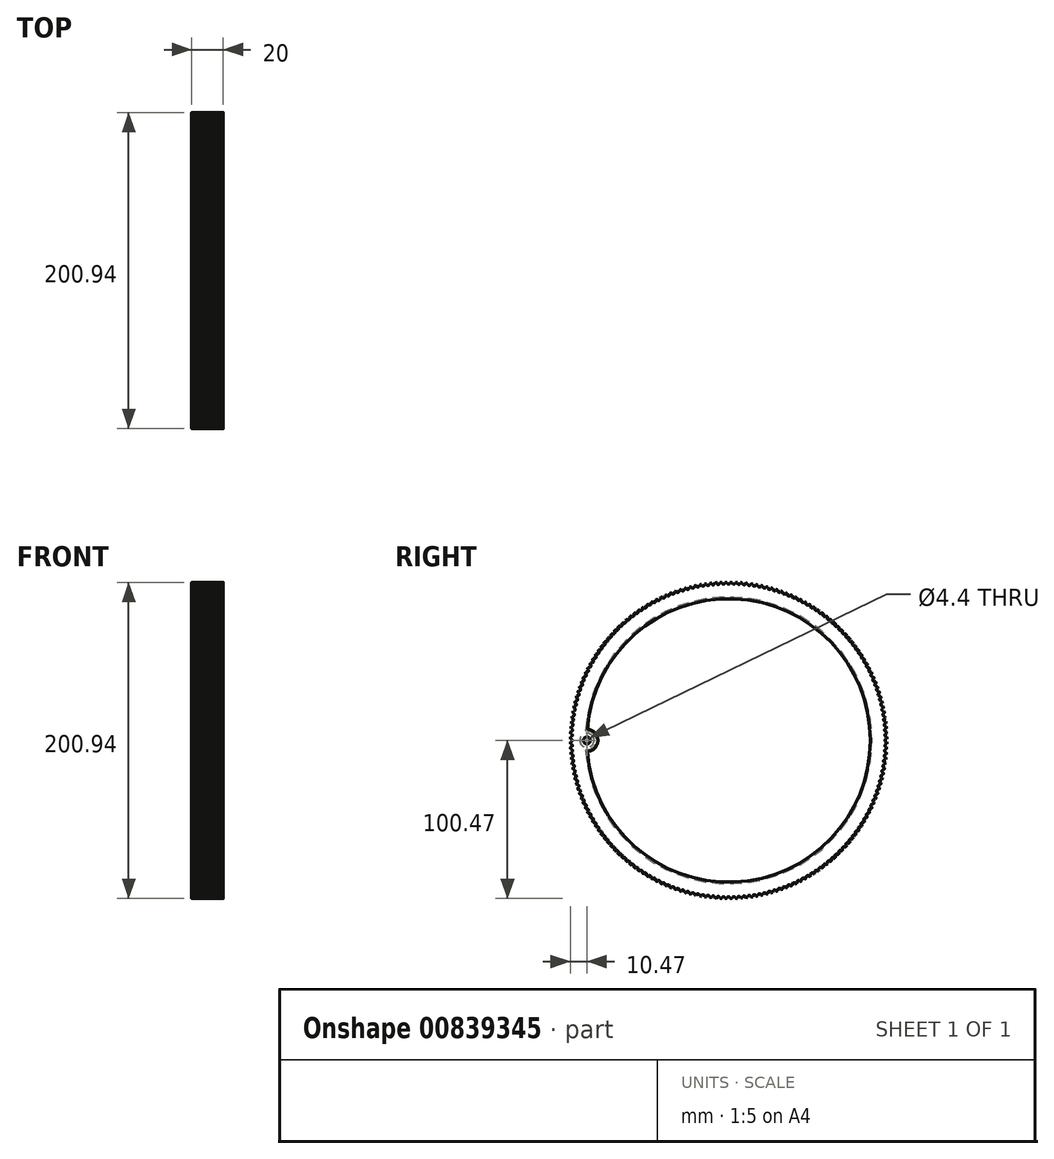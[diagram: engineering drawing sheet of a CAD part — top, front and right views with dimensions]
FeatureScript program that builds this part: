
annotation { "Feature Type Name" : "Feature", "Feature Type Description" : "" }
export const myFeature = defineFeature(function(context is Context, id is Id, definition is map)
    precondition{}
    {
        {
            var Q0;
            Q0=qCreatedBy(makeId("Right.planeOp"),FACE);
            var sketch = newSketch(context, id + "F0", { "sketchPlane" : qUnion([Q0])});
            skCircle(sketch, "E0", {"center": v(0, 0) * mm, "radius": 90 * mm});
            skLineSegment(sketch, "E1", {"start": v(0, 0) * mm, "end": v(0, 100.53) * mm, "construction": true});
            skPoint(sketch, "E2.center", {"position": v(0, 61.04) * mm});
            skLineSegment(sketch, "E2.anchor1", {"start": v(0, 61.04) * mm, "end": v(0, 81.8) * mm, "construction": true});
            skLineSegment(sketch, "E3.trimOffspring", {"start": v(0, 10.5) * mm, "end": v(0, 81.8) * mm, "construction": true});
            skLineSegment(sketch, "E4", {"start": v(-1.05, 100.47) * mm, "end": v(-1, 100.18) * mm});
            skArc(sketch, "E5", {"start": v(0.01, 99.33) * mm, "mid": v(0, 99.33) * mm, "end": v(-0.01, 99.33) * mm});
            skArc(sketch, "E6.filletArc", {"start": v(-1, 100.18) * mm, "mid": v(-0.67, 99.57) * mm, "end": v(-0.01, 99.33) * mm});
            skLineSegment(sketch, "E7.MirrorCS", {"start": v(1.05, 100.47) * mm, "end": v(1, 100.18) * mm});
            skArc(sketch, "E8.MirrorCS", {"start": v(1, 100.18) * mm, "mid": v(0.67, 99.57) * mm, "end": v(0.01, 99.33) * mm});
            skPoint(sketch, "E9.orphan", {"position": v(-12.8, 89.08) * mm});
            skPoint(sketch, "E10.orphan", {"position": v(12.8, 89.08) * mm});
            skLineSegment(sketch, "E11", {"start": v(0.02, 100.33) * mm, "end": v(1, 100.18) * mm, "construction": true});
            skLineSegment(sketch, "E12", {"start": v(-0.02, 100.33) * mm, "end": v(-1, 100.18) * mm, "construction": true});
            skLineSegment(sketch, "E13", {"start": v(-1.05, 100.47) * mm, "end": v(0, 100.53) * mm, "construction": true});
            skLineSegment(sketch, "E14", {"start": v(1.05, 100.47) * mm, "end": v(0, 100.53) * mm, "construction": true});
            skCircle(sketch, "E15", {"center": v(0, 0) * mm, "radius": 100.48 * mm});
            skArc(sketch, "E16.1.0", {"start": v(-4.28, 100.1) * mm, "mid": v(-3.93, 99.5) * mm, "end": v(-3.26, 99.27) * mm});
            skArc(sketch, "E16.1.1", {"start": v(-3.24, 99.27) * mm, "mid": v(-3.25, 99.27) * mm, "end": v(-3.26, 99.27) * mm});
            skArc(sketch, "E16.1.2", {"start": v(-2.27, 100.16) * mm, "mid": v(-2.59, 99.54) * mm, "end": v(-3.24, 99.27) * mm});
            skLineSegment(sketch, "E16.1.3", {"start": v(-2.24, 100.46) * mm, "end": v(-2.27, 100.16) * mm});
            skLineSegment(sketch, "E16.1.4", {"start": v(-4.33, 100.39) * mm, "end": v(-4.28, 100.1) * mm});
            skArc(sketch, "E16.2.0", {"start": v(-7.56, 99.9) * mm, "mid": v(-7.18, 99.31) * mm, "end": v(-6.51, 99.11) * mm});
            skArc(sketch, "E16.2.1", {"start": v(-6.48, 99.12) * mm, "mid": v(-6.5, 99.11) * mm, "end": v(-6.51, 99.11) * mm});
            skArc(sketch, "E16.2.2", {"start": v(-5.55, 100.04) * mm, "mid": v(-5.84, 99.4) * mm, "end": v(-6.48, 99.12) * mm});
            skLineSegment(sketch, "E16.2.3", {"start": v(-5.53, 100.33) * mm, "end": v(-5.55, 100.04) * mm});
            skLineSegment(sketch, "E16.2.4", {"start": v(-7.62, 100.2) * mm, "end": v(-7.56, 99.9) * mm});
            skArc(sketch, "E16.3.0", {"start": v(-10.82, 99.6) * mm, "mid": v(-10.43, 99.03) * mm, "end": v(-9.75, 98.85) * mm});
            skArc(sketch, "E16.3.1", {"start": v(-9.72, 98.85) * mm, "mid": v(-9.74, 98.85) * mm, "end": v(-9.75, 98.85) * mm});
            skArc(sketch, "E16.3.2", {"start": v(-8.82, 99.8) * mm, "mid": v(-9.1, 99.16) * mm, "end": v(-9.72, 98.85) * mm});
            skLineSegment(sketch, "E16.3.3", {"start": v(-8.8, 100.1) * mm, "end": v(-8.82, 99.8) * mm});
            skLineSegment(sketch, "E16.3.4", {"start": v(-10.9, 99.89) * mm, "end": v(-10.82, 99.6) * mm});
            skArc(sketch, "E16.4.0", {"start": v(-14.07, 99.2) * mm, "mid": v(-13.66, 98.63) * mm, "end": v(-12.98, 98.48) * mm});
            skArc(sketch, "E16.4.1", {"start": v(-12.95, 98.48) * mm, "mid": v(-12.96, 98.48) * mm, "end": v(-12.98, 98.48) * mm});
            skArc(sketch, "E16.4.2", {"start": v(-12.08, 99.46) * mm, "mid": v(-12.33, 98.8) * mm, "end": v(-12.95, 98.48) * mm});
            skLineSegment(sketch, "E16.4.3", {"start": v(-12.08, 99.75) * mm, "end": v(-12.08, 99.46) * mm});
            skLineSegment(sketch, "E16.4.4", {"start": v(-14.15, 99.48) * mm, "end": v(-14.07, 99.2) * mm});
            skArc(sketch, "E16.5.0", {"start": v(-17.31, 98.68) * mm, "mid": v(-16.88, 98.13) * mm, "end": v(-16.2, 98) * mm});
            skArc(sketch, "E16.5.1", {"start": v(-16.17, 98) * mm, "mid": v(-16.18, 98) * mm, "end": v(-16.2, 98) * mm});
            skArc(sketch, "E16.5.2", {"start": v(-15.33, 99.01) * mm, "mid": v(-15.56, 98.35) * mm, "end": v(-16.17, 98) * mm});
            skLineSegment(sketch, "E16.5.3", {"start": v(-15.33, 99.3) * mm, "end": v(-15.33, 99.01) * mm});
            skLineSegment(sketch, "E16.5.4", {"start": v(-17.4, 98.96) * mm, "end": v(-17.31, 98.68) * mm});
            skArc(sketch, "E16.6.0", {"start": v(-20.53, 98.06) * mm, "mid": v(-20.08, 97.53) * mm, "end": v(-19.4, 97.42) * mm});
            skArc(sketch, "E16.6.1", {"start": v(-19.36, 97.42) * mm, "mid": v(-19.38, 97.42) * mm, "end": v(-19.4, 97.42) * mm});
            skArc(sketch, "E16.6.2", {"start": v(-18.56, 98.46) * mm, "mid": v(-18.77, 97.79) * mm, "end": v(-19.36, 97.42) * mm});
            skLineSegment(sketch, "E16.6.3", {"start": v(-18.57, 98.75) * mm, "end": v(-18.56, 98.46) * mm});
            skLineSegment(sketch, "E16.6.4", {"start": v(-20.63, 98.34) * mm, "end": v(-20.53, 98.06) * mm});
            skArc(sketch, "E16.7.0", {"start": v(-23.73, 97.34) * mm, "mid": v(-23.26, 96.82) * mm, "end": v(-22.57, 96.73) * mm});
            skArc(sketch, "E16.7.1", {"start": v(-22.54, 96.74) * mm, "mid": v(-22.55, 96.73) * mm, "end": v(-22.57, 96.73) * mm});
            skArc(sketch, "E16.7.2", {"start": v(-21.77, 97.8) * mm, "mid": v(-21.96, 97.12) * mm, "end": v(-22.54, 96.74) * mm});
            skLineSegment(sketch, "E16.7.3", {"start": v(-21.8, 98.09) * mm, "end": v(-21.77, 97.8) * mm});
            skLineSegment(sketch, "E16.7.4", {"start": v(-23.84, 97.61) * mm, "end": v(-23.73, 97.34) * mm});
            skArc(sketch, "E16.8.0", {"start": v(-26.9, 96.51) * mm, "mid": v(-26.42, 96) * mm, "end": v(-25.72, 95.94) * mm});
            skArc(sketch, "E16.8.1", {"start": v(-25.7, 95.95) * mm, "mid": v(-25.7, 95.94) * mm, "end": v(-25.72, 95.94) * mm});
            skArc(sketch, "E16.8.2", {"start": v(-24.96, 97.03) * mm, "mid": v(-25.12, 96.35) * mm, "end": v(-25.7, 95.95) * mm});
            skLineSegment(sketch, "E16.8.3", {"start": v(-25, 97.32) * mm, "end": v(-24.96, 97.03) * mm});
            skLineSegment(sketch, "E16.8.4", {"start": v(-27.02, 96.78) * mm, "end": v(-26.9, 96.51) * mm});
            skArc(sketch, "E16.9.0", {"start": v(-30.04, 95.58) * mm, "mid": v(-29.55, 95.09) * mm, "end": v(-28.85, 95.05) * mm});
            skArc(sketch, "E16.9.1", {"start": v(-28.82, 95.05) * mm, "mid": v(-28.83, 95.05) * mm, "end": v(-28.85, 95.05) * mm});
            skArc(sketch, "E16.9.2", {"start": v(-28.12, 96.16) * mm, "mid": v(-28.26, 95.48) * mm, "end": v(-28.82, 95.05) * mm});
            skLineSegment(sketch, "E16.9.3", {"start": v(-28.16, 96.45) * mm, "end": v(-28.12, 96.16) * mm});
            skLineSegment(sketch, "E16.9.4", {"start": v(-30.17, 95.84) * mm, "end": v(-30.04, 95.58) * mm});
            skArc(sketch, "E16.10.0", {"start": v(-33.16, 94.54) * mm, "mid": v(-32.64, 94.07) * mm, "end": v(-31.94, 94.05) * mm});
            skArc(sketch, "E16.10.1", {"start": v(-31.91, 94.06) * mm, "mid": v(-31.93, 94.06) * mm, "end": v(-31.94, 94.05) * mm});
            skArc(sketch, "E16.10.2", {"start": v(-31.25, 95.2) * mm, "mid": v(-31.37, 94.5) * mm, "end": v(-31.91, 94.06) * mm});
            skLineSegment(sketch, "E16.10.3", {"start": v(-31.3, 95.48) * mm, "end": v(-31.25, 95.2) * mm});
            skLineSegment(sketch, "E16.10.4", {"start": v(-33.29, 94.8) * mm, "end": v(-33.16, 94.54) * mm});
            skArc(sketch, "E16.11.0", {"start": v(-36.23, 93.4) * mm, "mid": v(-35.7, 92.95) * mm, "end": v(-35, 92.96) * mm});
            skArc(sketch, "E16.11.1", {"start": v(-34.97, 92.97) * mm, "mid": v(-34.99, 92.96) * mm, "end": v(-35, 92.96) * mm});
            skArc(sketch, "E16.11.2", {"start": v(-34.35, 94.12) * mm, "mid": v(-34.45, 93.42) * mm, "end": v(-34.97, 92.97) * mm});
            skLineSegment(sketch, "E16.11.3", {"start": v(-34.41, 94.4) * mm, "end": v(-34.35, 94.12) * mm});
            skLineSegment(sketch, "E16.11.4", {"start": v(-36.37, 93.67) * mm, "end": v(-36.23, 93.4) * mm});
            skArc(sketch, "E16.12.0", {"start": v(-39.27, 92.17) * mm, "mid": v(-38.72, 91.73) * mm, "end": v(-38.02, 91.76) * mm});
            skArc(sketch, "E16.12.1", {"start": v(-38, 91.77) * mm, "mid": v(-38.01, 91.77) * mm, "end": v(-38.02, 91.76) * mm});
            skArc(sketch, "E16.12.2", {"start": v(-37.4, 92.94) * mm, "mid": v(-37.48, 92.25) * mm, "end": v(-38, 91.77) * mm});
            skLineSegment(sketch, "E16.12.3", {"start": v(-37.48, 93.23) * mm, "end": v(-37.4, 92.94) * mm});
            skLineSegment(sketch, "E16.12.4", {"start": v(-39.42, 92.43) * mm, "end": v(-39.27, 92.17) * mm});
            skArc(sketch, "E16.13.0", {"start": v(-42.26, 90.84) * mm, "mid": v(-41.7, 90.42) * mm, "end": v(-41, 90.47) * mm});
            skArc(sketch, "E16.13.1", {"start": v(-40.98, 90.48) * mm, "mid": v(-41, 90.47) * mm, "end": v(-41, 90.47) * mm});
            skArc(sketch, "E16.13.2", {"start": v(-40.43, 91.67) * mm, "mid": v(-40.48, 90.97) * mm, "end": v(-40.98, 90.48) * mm});
            skLineSegment(sketch, "E16.13.3", {"start": v(-40.51, 91.95) * mm, "end": v(-40.43, 91.67) * mm});
            skLineSegment(sketch, "E16.13.4", {"start": v(-42.42, 91.09) * mm, "end": v(-42.26, 90.84) * mm});
            skArc(sketch, "E16.14.0", {"start": v(-45.21, 89.4) * mm, "mid": v(-44.64, 89) * mm, "end": v(-43.94, 89.08) * mm});
            skArc(sketch, "E16.14.1", {"start": v(-43.92, 89.09) * mm, "mid": v(-43.93, 89.08) * mm, "end": v(-43.94, 89.08) * mm});
            skArc(sketch, "E16.14.2", {"start": v(-43.4, 90.3) * mm, "mid": v(-43.44, 89.6) * mm, "end": v(-43.92, 89.09) * mm});
            skLineSegment(sketch, "E16.14.3", {"start": v(-43.5, 90.58) * mm, "end": v(-43.4, 90.3) * mm});
            skLineSegment(sketch, "E16.14.4", {"start": v(-45.38, 89.65) * mm, "end": v(-45.21, 89.4) * mm});
            skArc(sketch, "E16.15.0", {"start": v(-48.11, 87.88) * mm, "mid": v(-47.53, 87.5) * mm, "end": v(-46.84, 87.6) * mm});
            skArc(sketch, "E16.15.1", {"start": v(-46.8, 87.6) * mm, "mid": v(-46.82, 87.6) * mm, "end": v(-46.84, 87.6) * mm});
            skArc(sketch, "E16.15.2", {"start": v(-46.34, 88.83) * mm, "mid": v(-46.35, 88.13) * mm, "end": v(-46.8, 87.6) * mm});
            skLineSegment(sketch, "E16.15.3", {"start": v(-46.44, 89.1) * mm, "end": v(-46.34, 88.83) * mm});
            skLineSegment(sketch, "E16.15.4", {"start": v(-48.29, 88.12) * mm, "end": v(-48.11, 87.88) * mm});
            skArc(sketch, "E16.16.0", {"start": v(-50.96, 86.26) * mm, "mid": v(-50.37, 85.9) * mm, "end": v(-49.68, 86.01) * mm});
            skArc(sketch, "E16.16.1", {"start": v(-49.65, 86.03) * mm, "mid": v(-49.66, 86.02) * mm, "end": v(-49.68, 86.01) * mm});
            skArc(sketch, "E16.16.2", {"start": v(-49.22, 87.27) * mm, "mid": v(-49.2, 86.57) * mm, "end": v(-49.65, 86.03) * mm});
            skLineSegment(sketch, "E16.16.3", {"start": v(-49.33, 87.54) * mm, "end": v(-49.22, 87.27) * mm});
            skLineSegment(sketch, "E16.16.4", {"start": v(-51.14, 86.49) * mm, "end": v(-50.96, 86.26) * mm});
            skArc(sketch, "E16.17.0", {"start": v(-53.76, 84.55) * mm, "mid": v(-53.15, 84.2) * mm, "end": v(-52.46, 84.34) * mm});
            skArc(sketch, "E16.17.1", {"start": v(-52.44, 84.36) * mm, "mid": v(-52.45, 84.35) * mm, "end": v(-52.46, 84.34) * mm});
            skArc(sketch, "E16.17.2", {"start": v(-52.05, 85.6) * mm, "mid": v(-52.01, 84.9) * mm, "end": v(-52.44, 84.36) * mm});
            skLineSegment(sketch, "E16.17.3", {"start": v(-52.17, 85.88) * mm, "end": v(-52.05, 85.6) * mm});
            skLineSegment(sketch, "E16.17.4", {"start": v(-53.95, 84.77) * mm, "end": v(-53.76, 84.55) * mm});
            skArc(sketch, "E16.18.0", {"start": v(-56.5, 82.74) * mm, "mid": v(-55.88, 82.42) * mm, "end": v(-55.2, 82.58) * mm});
            skArc(sketch, "E16.18.1", {"start": v(-55.17, 82.6) * mm, "mid": v(-55.18, 82.59) * mm, "end": v(-55.2, 82.58) * mm});
            skArc(sketch, "E16.18.2", {"start": v(-54.82, 83.86) * mm, "mid": v(-54.76, 83.16) * mm, "end": v(-55.17, 82.6) * mm});
            skLineSegment(sketch, "E16.18.3", {"start": v(-54.95, 84.12) * mm, "end": v(-54.82, 83.86) * mm});
            skLineSegment(sketch, "E16.18.4", {"start": v(-56.7, 82.96) * mm, "end": v(-56.5, 82.74) * mm});
            skArc(sketch, "E16.19.0", {"start": v(-59.17, 80.85) * mm, "mid": v(-58.54, 80.55) * mm, "end": v(-57.87, 80.73) * mm});
            skArc(sketch, "E16.19.1", {"start": v(-57.84, 80.75) * mm, "mid": v(-57.86, 80.74) * mm, "end": v(-57.87, 80.73) * mm});
            skArc(sketch, "E16.19.2", {"start": v(-57.54, 82.02) * mm, "mid": v(-57.45, 81.33) * mm, "end": v(-57.84, 80.75) * mm});
            skLineSegment(sketch, "E16.19.3", {"start": v(-57.67, 82.28) * mm, "end": v(-57.54, 82.02) * mm});
            skLineSegment(sketch, "E16.19.4", {"start": v(-59.38, 81.06) * mm, "end": v(-59.17, 80.85) * mm});
            skArc(sketch, "E16.20.0", {"start": v(-61.79, 78.87) * mm, "mid": v(-61.15, 78.59) * mm, "end": v(-60.48, 78.8) * mm});
            skArc(sketch, "E16.20.1", {"start": v(-60.45, 78.81) * mm, "mid": v(-60.47, 78.8) * mm, "end": v(-60.48, 78.8) * mm});
            skArc(sketch, "E16.20.2", {"start": v(-60.2, 80.1) * mm, "mid": v(-60.08, 79.4) * mm, "end": v(-60.45, 78.81) * mm});
            skLineSegment(sketch, "E16.20.3", {"start": v(-60.33, 80.35) * mm, "end": v(-60.2, 80.1) * mm});
            skLineSegment(sketch, "E16.20.4", {"start": v(-62, 79.07) * mm, "end": v(-61.79, 78.87) * mm});
            skArc(sketch, "E16.21.0", {"start": v(-64.33, 76.8) * mm, "mid": v(-63.69, 76.54) * mm, "end": v(-63.02, 76.77) * mm});
            skArc(sketch, "E16.21.1", {"start": v(-63, 76.79) * mm, "mid": v(-63.01, 76.78) * mm, "end": v(-63.02, 76.77) * mm});
            skArc(sketch, "E16.21.2", {"start": v(-62.78, 78.08) * mm, "mid": v(-62.65, 77.4) * mm, "end": v(-63, 76.79) * mm});
            skLineSegment(sketch, "E16.21.3", {"start": v(-62.93, 78.33) * mm, "end": v(-62.78, 78.08) * mm});
            skLineSegment(sketch, "E16.21.4", {"start": v(-64.55, 77) * mm, "end": v(-64.33, 76.8) * mm});
            skArc(sketch, "E16.22.0", {"start": v(-66.81, 74.66) * mm, "mid": v(-66.16, 74.42) * mm, "end": v(-65.5, 74.67) * mm});
            skArc(sketch, "E16.22.1", {"start": v(-65.48, 74.69) * mm, "mid": v(-65.5, 74.68) * mm, "end": v(-65.5, 74.67) * mm});
            skArc(sketch, "E16.22.2", {"start": v(-65.3, 75.99) * mm, "mid": v(-65.15, 75.3) * mm, "end": v(-65.48, 74.69) * mm});
            skLineSegment(sketch, "E16.22.3", {"start": v(-65.46, 76.23) * mm, "end": v(-65.3, 75.99) * mm});
            skLineSegment(sketch, "E16.22.4", {"start": v(-67.04, 74.85) * mm, "end": v(-66.81, 74.66) * mm});
            skArc(sketch, "E16.23.0", {"start": v(-69.22, 72.43) * mm, "mid": v(-68.55, 72.21) * mm, "end": v(-67.9, 72.49) * mm});
            skArc(sketch, "E16.23.1", {"start": v(-67.89, 72.5) * mm, "mid": v(-67.9, 72.5) * mm, "end": v(-67.9, 72.49) * mm});
            skArc(sketch, "E16.23.2", {"start": v(-67.75, 73.8) * mm, "mid": v(-67.58, 73.13) * mm, "end": v(-67.89, 72.5) * mm});
            skLineSegment(sketch, "E16.23.3", {"start": v(-67.92, 74.05) * mm, "end": v(-67.75, 73.8) * mm});
            skLineSegment(sketch, "E16.23.4", {"start": v(-69.45, 72.62) * mm, "end": v(-69.22, 72.43) * mm});
            skArc(sketch, "E16.24.0", {"start": v(-71.55, 70.13) * mm, "mid": v(-70.88, 69.93) * mm, "end": v(-70.24, 70.22) * mm});
            skArc(sketch, "E16.24.1", {"start": v(-70.22, 70.24) * mm, "mid": v(-70.23, 70.23) * mm, "end": v(-70.24, 70.22) * mm});
            skArc(sketch, "E16.24.2", {"start": v(-70.13, 71.55) * mm, "mid": v(-69.93, 70.88) * mm, "end": v(-70.22, 70.24) * mm});
            skLineSegment(sketch, "E16.24.3", {"start": v(-70.3, 71.79) * mm, "end": v(-70.13, 71.55) * mm});
            skLineSegment(sketch, "E16.24.4", {"start": v(-71.79, 70.3) * mm, "end": v(-71.55, 70.13) * mm});
            skArc(sketch, "E16.25.0", {"start": v(-73.8, 67.75) * mm, "mid": v(-73.13, 67.58) * mm, "end": v(-72.5, 67.89) * mm});
            skArc(sketch, "E16.25.1", {"start": v(-72.49, 67.9) * mm, "mid": v(-72.5, 67.9) * mm, "end": v(-72.5, 67.89) * mm});
            skArc(sketch, "E16.25.2", {"start": v(-72.43, 69.22) * mm, "mid": v(-72.21, 68.55) * mm, "end": v(-72.49, 67.9) * mm});
            skLineSegment(sketch, "E16.25.3", {"start": v(-72.62, 69.45) * mm, "end": v(-72.43, 69.22) * mm});
            skLineSegment(sketch, "E16.25.4", {"start": v(-74.05, 67.92) * mm, "end": v(-73.8, 67.75) * mm});
            skArc(sketch, "E16.26.0", {"start": v(-75.99, 65.3) * mm, "mid": v(-75.3, 65.15) * mm, "end": v(-74.69, 65.48) * mm});
            skArc(sketch, "E16.26.1", {"start": v(-74.67, 65.5) * mm, "mid": v(-74.68, 65.5) * mm, "end": v(-74.69, 65.48) * mm});
            skArc(sketch, "E16.26.2", {"start": v(-74.66, 66.81) * mm, "mid": v(-74.42, 66.16) * mm, "end": v(-74.67, 65.5) * mm});
            skLineSegment(sketch, "E16.26.3", {"start": v(-74.85, 67.04) * mm, "end": v(-74.66, 66.81) * mm});
            skLineSegment(sketch, "E16.26.4", {"start": v(-76.23, 65.46) * mm, "end": v(-75.99, 65.3) * mm});
            skArc(sketch, "E16.27.0", {"start": v(-78.08, 62.78) * mm, "mid": v(-77.4, 62.65) * mm, "end": v(-76.79, 63) * mm});
            skArc(sketch, "E16.27.1", {"start": v(-76.77, 63.02) * mm, "mid": v(-76.78, 63.01) * mm, "end": v(-76.79, 63) * mm});
            skArc(sketch, "E16.27.2", {"start": v(-76.8, 64.33) * mm, "mid": v(-76.54, 63.69) * mm, "end": v(-76.77, 63.02) * mm});
            skLineSegment(sketch, "E16.27.3", {"start": v(-77, 64.55) * mm, "end": v(-76.8, 64.33) * mm});
            skLineSegment(sketch, "E16.27.4", {"start": v(-78.33, 62.93) * mm, "end": v(-78.08, 62.78) * mm});
            skArc(sketch, "E16.28.0", {"start": v(-80.1, 60.2) * mm, "mid": v(-79.4, 60.08) * mm, "end": v(-78.81, 60.45) * mm});
            skArc(sketch, "E16.28.1", {"start": v(-78.8, 60.48) * mm, "mid": v(-78.8, 60.47) * mm, "end": v(-78.81, 60.45) * mm});
            skArc(sketch, "E16.28.2", {"start": v(-78.87, 61.79) * mm, "mid": v(-78.59, 61.15) * mm, "end": v(-78.8, 60.48) * mm});
            skLineSegment(sketch, "E16.28.3", {"start": v(-79.07, 62) * mm, "end": v(-78.87, 61.79) * mm});
            skLineSegment(sketch, "E16.28.4", {"start": v(-80.35, 60.33) * mm, "end": v(-80.1, 60.2) * mm});
            skArc(sketch, "E16.29.0", {"start": v(-82.02, 57.54) * mm, "mid": v(-81.33, 57.45) * mm, "end": v(-80.75, 57.84) * mm});
            skArc(sketch, "E16.29.1", {"start": v(-80.73, 57.87) * mm, "mid": v(-80.74, 57.86) * mm, "end": v(-80.75, 57.84) * mm});
            skArc(sketch, "E16.29.2", {"start": v(-80.85, 59.17) * mm, "mid": v(-80.55, 58.54) * mm, "end": v(-80.73, 57.87) * mm});
            skLineSegment(sketch, "E16.29.3", {"start": v(-81.06, 59.38) * mm, "end": v(-80.85, 59.17) * mm});
            skLineSegment(sketch, "E16.29.4", {"start": v(-82.28, 57.67) * mm, "end": v(-82.02, 57.54) * mm});
            skArc(sketch, "E16.30.0", {"start": v(-83.86, 54.82) * mm, "mid": v(-83.16, 54.76) * mm, "end": v(-82.6, 55.17) * mm});
            skArc(sketch, "E16.30.1", {"start": v(-82.58, 55.2) * mm, "mid": v(-82.59, 55.18) * mm, "end": v(-82.6, 55.17) * mm});
            skArc(sketch, "E16.30.2", {"start": v(-82.74, 56.5) * mm, "mid": v(-82.42, 55.88) * mm, "end": v(-82.58, 55.2) * mm});
            skLineSegment(sketch, "E16.30.3", {"start": v(-82.96, 56.7) * mm, "end": v(-82.74, 56.5) * mm});
            skLineSegment(sketch, "E16.30.4", {"start": v(-84.12, 54.95) * mm, "end": v(-83.86, 54.82) * mm});
            skArc(sketch, "E16.31.0", {"start": v(-85.6, 52.05) * mm, "mid": v(-84.9, 52.01) * mm, "end": v(-84.36, 52.44) * mm});
            skArc(sketch, "E16.31.1", {"start": v(-84.34, 52.46) * mm, "mid": v(-84.35, 52.45) * mm, "end": v(-84.36, 52.44) * mm});
            skArc(sketch, "E16.31.2", {"start": v(-84.55, 53.76) * mm, "mid": v(-84.2, 53.15) * mm, "end": v(-84.34, 52.46) * mm});
            skLineSegment(sketch, "E16.31.3", {"start": v(-84.77, 53.95) * mm, "end": v(-84.55, 53.76) * mm});
            skLineSegment(sketch, "E16.31.4", {"start": v(-85.88, 52.17) * mm, "end": v(-85.6, 52.05) * mm});
            skArc(sketch, "E16.32.0", {"start": v(-87.27, 49.22) * mm, "mid": v(-86.57, 49.2) * mm, "end": v(-86.03, 49.65) * mm});
            skArc(sketch, "E16.32.1", {"start": v(-86.01, 49.68) * mm, "mid": v(-86.02, 49.66) * mm, "end": v(-86.03, 49.65) * mm});
            skArc(sketch, "E16.32.2", {"start": v(-86.26, 50.96) * mm, "mid": v(-85.9, 50.37) * mm, "end": v(-86.01, 49.68) * mm});
            skLineSegment(sketch, "E16.32.3", {"start": v(-86.49, 51.14) * mm, "end": v(-86.26, 50.96) * mm});
            skLineSegment(sketch, "E16.32.4", {"start": v(-87.54, 49.33) * mm, "end": v(-87.27, 49.22) * mm});
            skArc(sketch, "E16.33.0", {"start": v(-88.83, 46.34) * mm, "mid": v(-88.13, 46.35) * mm, "end": v(-87.6, 46.8) * mm});
            skArc(sketch, "E16.33.1", {"start": v(-87.6, 46.84) * mm, "mid": v(-87.6, 46.82) * mm, "end": v(-87.6, 46.8) * mm});
            skArc(sketch, "E16.33.2", {"start": v(-87.88, 48.11) * mm, "mid": v(-87.5, 47.53) * mm, "end": v(-87.6, 46.84) * mm});
            skLineSegment(sketch, "E16.33.3", {"start": v(-88.12, 48.29) * mm, "end": v(-87.88, 48.11) * mm});
            skLineSegment(sketch, "E16.33.4", {"start": v(-89.1, 46.44) * mm, "end": v(-88.83, 46.34) * mm});
            skArc(sketch, "E16.34.0", {"start": v(-90.3, 43.4) * mm, "mid": v(-89.6, 43.44) * mm, "end": v(-89.09, 43.92) * mm});
            skArc(sketch, "E16.34.1", {"start": v(-89.08, 43.94) * mm, "mid": v(-89.08, 43.93) * mm, "end": v(-89.09, 43.92) * mm});
            skArc(sketch, "E16.34.2", {"start": v(-89.4, 45.21) * mm, "mid": v(-89, 44.64) * mm, "end": v(-89.08, 43.94) * mm});
            skLineSegment(sketch, "E16.34.3", {"start": v(-89.65, 45.38) * mm, "end": v(-89.4, 45.21) * mm});
            skLineSegment(sketch, "E16.34.4", {"start": v(-90.58, 43.5) * mm, "end": v(-90.3, 43.4) * mm});
            skArc(sketch, "E16.35.0", {"start": v(-91.67, 40.43) * mm, "mid": v(-90.97, 40.48) * mm, "end": v(-90.48, 40.98) * mm});
            skArc(sketch, "E16.35.1", {"start": v(-90.47, 41) * mm, "mid": v(-90.47, 41) * mm, "end": v(-90.48, 40.98) * mm});
            skArc(sketch, "E16.35.2", {"start": v(-90.84, 42.26) * mm, "mid": v(-90.42, 41.7) * mm, "end": v(-90.47, 41) * mm});
            skLineSegment(sketch, "E16.35.3", {"start": v(-91.09, 42.42) * mm, "end": v(-90.84, 42.26) * mm});
            skLineSegment(sketch, "E16.35.4", {"start": v(-91.95, 40.51) * mm, "end": v(-91.67, 40.43) * mm});
            skArc(sketch, "E16.36.0", {"start": v(-92.94, 37.4) * mm, "mid": v(-92.25, 37.48) * mm, "end": v(-91.77, 38) * mm});
            skArc(sketch, "E16.36.1", {"start": v(-91.76, 38.02) * mm, "mid": v(-91.77, 38.01) * mm, "end": v(-91.77, 38) * mm});
            skArc(sketch, "E16.36.2", {"start": v(-92.17, 39.27) * mm, "mid": v(-91.73, 38.72) * mm, "end": v(-91.76, 38.02) * mm});
            skLineSegment(sketch, "E16.36.3", {"start": v(-92.43, 39.42) * mm, "end": v(-92.17, 39.27) * mm});
            skLineSegment(sketch, "E16.36.4", {"start": v(-93.23, 37.48) * mm, "end": v(-92.94, 37.4) * mm});
            skArc(sketch, "E16.37.0", {"start": v(-94.12, 34.35) * mm, "mid": v(-93.42, 34.45) * mm, "end": v(-92.97, 34.97) * mm});
            skArc(sketch, "E16.37.1", {"start": v(-92.96, 35) * mm, "mid": v(-92.96, 34.99) * mm, "end": v(-92.97, 34.97) * mm});
            skArc(sketch, "E16.37.2", {"start": v(-93.4, 36.23) * mm, "mid": v(-92.95, 35.7) * mm, "end": v(-92.96, 35) * mm});
            skLineSegment(sketch, "E16.37.3", {"start": v(-93.67, 36.37) * mm, "end": v(-93.4, 36.23) * mm});
            skLineSegment(sketch, "E16.37.4", {"start": v(-94.4, 34.41) * mm, "end": v(-94.12, 34.35) * mm});
            skArc(sketch, "E16.38.0", {"start": v(-95.2, 31.25) * mm, "mid": v(-94.5, 31.37) * mm, "end": v(-94.06, 31.91) * mm});
            skArc(sketch, "E16.38.1", {"start": v(-94.05, 31.94) * mm, "mid": v(-94.06, 31.93) * mm, "end": v(-94.06, 31.91) * mm});
            skArc(sketch, "E16.38.2", {"start": v(-94.54, 33.16) * mm, "mid": v(-94.07, 32.64) * mm, "end": v(-94.05, 31.94) * mm});
            skLineSegment(sketch, "E16.38.3", {"start": v(-94.8, 33.29) * mm, "end": v(-94.54, 33.16) * mm});
            skLineSegment(sketch, "E16.38.4", {"start": v(-95.48, 31.3) * mm, "end": v(-95.2, 31.25) * mm});
            skArc(sketch, "E16.39.0", {"start": v(-96.16, 28.12) * mm, "mid": v(-95.48, 28.26) * mm, "end": v(-95.05, 28.82) * mm});
            skArc(sketch, "E16.39.1", {"start": v(-95.05, 28.85) * mm, "mid": v(-95.05, 28.83) * mm, "end": v(-95.05, 28.82) * mm});
            skArc(sketch, "E16.39.2", {"start": v(-95.58, 30.04) * mm, "mid": v(-95.09, 29.55) * mm, "end": v(-95.05, 28.85) * mm});
            skLineSegment(sketch, "E16.39.3", {"start": v(-95.84, 30.17) * mm, "end": v(-95.58, 30.04) * mm});
            skLineSegment(sketch, "E16.39.4", {"start": v(-96.45, 28.16) * mm, "end": v(-96.16, 28.12) * mm});
            skArc(sketch, "E16.40.0", {"start": v(-97.03, 24.96) * mm, "mid": v(-96.35, 25.12) * mm, "end": v(-95.95, 25.7) * mm});
            skArc(sketch, "E16.40.1", {"start": v(-95.94, 25.72) * mm, "mid": v(-95.94, 25.7) * mm, "end": v(-95.95, 25.7) * mm});
            skArc(sketch, "E16.40.2", {"start": v(-96.51, 26.9) * mm, "mid": v(-96, 26.42) * mm, "end": v(-95.94, 25.72) * mm});
            skLineSegment(sketch, "E16.40.3", {"start": v(-96.78, 27.02) * mm, "end": v(-96.51, 26.9) * mm});
            skLineSegment(sketch, "E16.40.4", {"start": v(-97.32, 25) * mm, "end": v(-97.03, 24.96) * mm});
            skArc(sketch, "E16.41.0", {"start": v(-97.8, 21.77) * mm, "mid": v(-97.12, 21.96) * mm, "end": v(-96.74, 22.54) * mm});
            skArc(sketch, "E16.41.1", {"start": v(-96.73, 22.57) * mm, "mid": v(-96.73, 22.55) * mm, "end": v(-96.74, 22.54) * mm});
            skArc(sketch, "E16.41.2", {"start": v(-97.34, 23.73) * mm, "mid": v(-96.82, 23.26) * mm, "end": v(-96.73, 22.57) * mm});
            skLineSegment(sketch, "E16.41.3", {"start": v(-97.61, 23.84) * mm, "end": v(-97.34, 23.73) * mm});
            skLineSegment(sketch, "E16.41.4", {"start": v(-98.09, 21.8) * mm, "end": v(-97.8, 21.77) * mm});
            skArc(sketch, "E16.42.0", {"start": v(-98.46, 18.56) * mm, "mid": v(-97.79, 18.77) * mm, "end": v(-97.42, 19.36) * mm});
            skArc(sketch, "E16.42.1", {"start": v(-97.42, 19.4) * mm, "mid": v(-97.42, 19.38) * mm, "end": v(-97.42, 19.36) * mm});
            skArc(sketch, "E16.42.2", {"start": v(-98.06, 20.53) * mm, "mid": v(-97.53, 20.08) * mm, "end": v(-97.42, 19.4) * mm});
            skLineSegment(sketch, "E16.42.3", {"start": v(-98.34, 20.63) * mm, "end": v(-98.06, 20.53) * mm});
            skLineSegment(sketch, "E16.42.4", {"start": v(-98.75, 18.57) * mm, "end": v(-98.46, 18.56) * mm});
            skArc(sketch, "E16.43.0", {"start": v(-99.01, 15.33) * mm, "mid": v(-98.35, 15.56) * mm, "end": v(-98, 16.17) * mm});
            skArc(sketch, "E16.43.1", {"start": v(-98, 16.2) * mm, "mid": v(-98, 16.18) * mm, "end": v(-98, 16.17) * mm});
            skArc(sketch, "E16.43.2", {"start": v(-98.68, 17.31) * mm, "mid": v(-98.13, 16.88) * mm, "end": v(-98, 16.2) * mm});
            skLineSegment(sketch, "E16.43.3", {"start": v(-98.96, 17.4) * mm, "end": v(-98.68, 17.31) * mm});
            skLineSegment(sketch, "E16.43.4", {"start": v(-99.3, 15.33) * mm, "end": v(-99.01, 15.33) * mm});
            skArc(sketch, "E16.44.0", {"start": v(-99.46, 12.08) * mm, "mid": v(-98.8, 12.33) * mm, "end": v(-98.48, 12.95) * mm});
            skArc(sketch, "E16.44.1", {"start": v(-98.48, 12.98) * mm, "mid": v(-98.48, 12.96) * mm, "end": v(-98.48, 12.95) * mm});
            skArc(sketch, "E16.44.2", {"start": v(-99.2, 14.07) * mm, "mid": v(-98.63, 13.66) * mm, "end": v(-98.48, 12.98) * mm});
            skLineSegment(sketch, "E16.44.3", {"start": v(-99.48, 14.15) * mm, "end": v(-99.2, 14.07) * mm});
            skLineSegment(sketch, "E16.44.4", {"start": v(-99.75, 12.08) * mm, "end": v(-99.46, 12.08) * mm});
            skArc(sketch, "E16.45.0", {"start": v(-99.8, 8.82) * mm, "mid": v(-99.16, 9.1) * mm, "end": v(-98.85, 9.72) * mm});
            skArc(sketch, "E16.45.1", {"start": v(-98.85, 9.75) * mm, "mid": v(-98.85, 9.74) * mm, "end": v(-98.85, 9.72) * mm});
            skArc(sketch, "E16.45.2", {"start": v(-99.6, 10.82) * mm, "mid": v(-99.03, 10.43) * mm, "end": v(-98.85, 9.75) * mm});
            skLineSegment(sketch, "E16.45.3", {"start": v(-99.89, 10.9) * mm, "end": v(-99.6, 10.82) * mm});
            skLineSegment(sketch, "E16.45.4", {"start": v(-100.1, 8.8) * mm, "end": v(-99.8, 8.82) * mm});
            skArc(sketch, "E16.46.0", {"start": v(-100.04, 5.55) * mm, "mid": v(-99.4, 5.84) * mm, "end": v(-99.12, 6.48) * mm});
            skArc(sketch, "E16.46.1", {"start": v(-99.11, 6.51) * mm, "mid": v(-99.11, 6.5) * mm, "end": v(-99.12, 6.48) * mm});
            skArc(sketch, "E16.46.2", {"start": v(-99.9, 7.56) * mm, "mid": v(-99.31, 7.18) * mm, "end": v(-99.11, 6.51) * mm});
            skLineSegment(sketch, "E16.46.3", {"start": v(-100.2, 7.62) * mm, "end": v(-99.9, 7.56) * mm});
            skLineSegment(sketch, "E16.46.4", {"start": v(-100.33, 5.53) * mm, "end": v(-100.04, 5.55) * mm});
            skArc(sketch, "E16.47.0", {"start": v(-100.16, 2.27) * mm, "mid": v(-99.54, 2.59) * mm, "end": v(-99.27, 3.24) * mm});
            skArc(sketch, "E16.47.1", {"start": v(-99.27, 3.26) * mm, "mid": v(-99.27, 3.25) * mm, "end": v(-99.27, 3.24) * mm});
            skArc(sketch, "E16.47.2", {"start": v(-100.1, 4.28) * mm, "mid": v(-99.5, 3.93) * mm, "end": v(-99.27, 3.26) * mm});
            skLineSegment(sketch, "E16.47.3", {"start": v(-100.39, 4.33) * mm, "end": v(-100.1, 4.28) * mm});
            skLineSegment(sketch, "E16.47.4", {"start": v(-100.46, 2.24) * mm, "end": v(-100.16, 2.27) * mm});
            skArc(sketch, "E16.48.0", {"start": v(-100.18, -1) * mm, "mid": v(-99.57, -0.67) * mm, "end": v(-99.33, -0.01) * mm});
            skArc(sketch, "E16.48.1", {"start": v(-99.33, 0.01) * mm, "mid": v(-99.33, 0) * mm, "end": v(-99.33, -0.01) * mm});
            skArc(sketch, "E16.48.2", {"start": v(-100.18, 1) * mm, "mid": v(-99.57, 0.67) * mm, "end": v(-99.33, 0.01) * mm});
            skLineSegment(sketch, "E16.48.3", {"start": v(-100.47, 1.05) * mm, "end": v(-100.18, 1) * mm});
            skLineSegment(sketch, "E16.48.4", {"start": v(-100.47, -1.05) * mm, "end": v(-100.18, -1) * mm});
            skArc(sketch, "E16.49.0", {"start": v(-100.1, -4.28) * mm, "mid": v(-99.5, -3.93) * mm, "end": v(-99.27, -3.26) * mm});
            skArc(sketch, "E16.49.1", {"start": v(-99.27, -3.24) * mm, "mid": v(-99.27, -3.25) * mm, "end": v(-99.27, -3.26) * mm});
            skArc(sketch, "E16.49.2", {"start": v(-100.16, -2.27) * mm, "mid": v(-99.54, -2.59) * mm, "end": v(-99.27, -3.24) * mm});
            skLineSegment(sketch, "E16.49.3", {"start": v(-100.46, -2.24) * mm, "end": v(-100.16, -2.27) * mm});
            skLineSegment(sketch, "E16.49.4", {"start": v(-100.39, -4.33) * mm, "end": v(-100.1, -4.28) * mm});
            skArc(sketch, "E16.50.0", {"start": v(-99.9, -7.56) * mm, "mid": v(-99.31, -7.18) * mm, "end": v(-99.11, -6.51) * mm});
            skArc(sketch, "E16.50.1", {"start": v(-99.12, -6.48) * mm, "mid": v(-99.11, -6.5) * mm, "end": v(-99.11, -6.51) * mm});
            skArc(sketch, "E16.50.2", {"start": v(-100.04, -5.55) * mm, "mid": v(-99.4, -5.84) * mm, "end": v(-99.12, -6.48) * mm});
            skLineSegment(sketch, "E16.50.3", {"start": v(-100.33, -5.53) * mm, "end": v(-100.04, -5.55) * mm});
            skLineSegment(sketch, "E16.50.4", {"start": v(-100.2, -7.62) * mm, "end": v(-99.9, -7.56) * mm});
            skArc(sketch, "E16.51.0", {"start": v(-99.6, -10.82) * mm, "mid": v(-99.03, -10.43) * mm, "end": v(-98.85, -9.75) * mm});
            skArc(sketch, "E16.51.1", {"start": v(-98.85, -9.72) * mm, "mid": v(-98.85, -9.74) * mm, "end": v(-98.85, -9.75) * mm});
            skArc(sketch, "E16.51.2", {"start": v(-99.8, -8.82) * mm, "mid": v(-99.16, -9.1) * mm, "end": v(-98.85, -9.72) * mm});
            skLineSegment(sketch, "E16.51.3", {"start": v(-100.1, -8.8) * mm, "end": v(-99.8, -8.82) * mm});
            skLineSegment(sketch, "E16.51.4", {"start": v(-99.89, -10.9) * mm, "end": v(-99.6, -10.82) * mm});
            skArc(sketch, "E16.52.0", {"start": v(-99.2, -14.07) * mm, "mid": v(-98.63, -13.66) * mm, "end": v(-98.48, -12.98) * mm});
            skArc(sketch, "E16.52.1", {"start": v(-98.48, -12.95) * mm, "mid": v(-98.48, -12.96) * mm, "end": v(-98.48, -12.98) * mm});
            skArc(sketch, "E16.52.2", {"start": v(-99.46, -12.08) * mm, "mid": v(-98.8, -12.33) * mm, "end": v(-98.48, -12.95) * mm});
            skLineSegment(sketch, "E16.52.3", {"start": v(-99.75, -12.08) * mm, "end": v(-99.46, -12.08) * mm});
            skLineSegment(sketch, "E16.52.4", {"start": v(-99.48, -14.15) * mm, "end": v(-99.2, -14.07) * mm});
            skArc(sketch, "E16.53.0", {"start": v(-98.68, -17.31) * mm, "mid": v(-98.13, -16.88) * mm, "end": v(-98, -16.2) * mm});
            skArc(sketch, "E16.53.1", {"start": v(-98, -16.17) * mm, "mid": v(-98, -16.18) * mm, "end": v(-98, -16.2) * mm});
            skArc(sketch, "E16.53.2", {"start": v(-99.01, -15.33) * mm, "mid": v(-98.35, -15.56) * mm, "end": v(-98, -16.17) * mm});
            skLineSegment(sketch, "E16.53.3", {"start": v(-99.3, -15.33) * mm, "end": v(-99.01, -15.33) * mm});
            skLineSegment(sketch, "E16.53.4", {"start": v(-98.96, -17.4) * mm, "end": v(-98.68, -17.31) * mm});
            skArc(sketch, "E16.54.0", {"start": v(-98.06, -20.53) * mm, "mid": v(-97.53, -20.08) * mm, "end": v(-97.42, -19.4) * mm});
            skArc(sketch, "E16.54.1", {"start": v(-97.42, -19.36) * mm, "mid": v(-97.42, -19.38) * mm, "end": v(-97.42, -19.4) * mm});
            skArc(sketch, "E16.54.2", {"start": v(-98.46, -18.56) * mm, "mid": v(-97.79, -18.77) * mm, "end": v(-97.42, -19.36) * mm});
            skLineSegment(sketch, "E16.54.3", {"start": v(-98.75, -18.57) * mm, "end": v(-98.46, -18.56) * mm});
            skLineSegment(sketch, "E16.54.4", {"start": v(-98.34, -20.63) * mm, "end": v(-98.06, -20.53) * mm});
            skArc(sketch, "E16.55.0", {"start": v(-97.34, -23.73) * mm, "mid": v(-96.82, -23.26) * mm, "end": v(-96.73, -22.57) * mm});
            skArc(sketch, "E16.55.1", {"start": v(-96.74, -22.54) * mm, "mid": v(-96.73, -22.55) * mm, "end": v(-96.73, -22.57) * mm});
            skArc(sketch, "E16.55.2", {"start": v(-97.8, -21.77) * mm, "mid": v(-97.12, -21.96) * mm, "end": v(-96.74, -22.54) * mm});
            skLineSegment(sketch, "E16.55.3", {"start": v(-98.09, -21.8) * mm, "end": v(-97.8, -21.77) * mm});
            skLineSegment(sketch, "E16.55.4", {"start": v(-97.61, -23.84) * mm, "end": v(-97.34, -23.73) * mm});
            skArc(sketch, "E16.56.0", {"start": v(-96.51, -26.9) * mm, "mid": v(-96, -26.42) * mm, "end": v(-95.94, -25.72) * mm});
            skArc(sketch, "E16.56.1", {"start": v(-95.95, -25.7) * mm, "mid": v(-95.94, -25.7) * mm, "end": v(-95.94, -25.72) * mm});
            skArc(sketch, "E16.56.2", {"start": v(-97.03, -24.96) * mm, "mid": v(-96.35, -25.12) * mm, "end": v(-95.95, -25.7) * mm});
            skLineSegment(sketch, "E16.56.3", {"start": v(-97.32, -25) * mm, "end": v(-97.03, -24.96) * mm});
            skLineSegment(sketch, "E16.56.4", {"start": v(-96.78, -27.02) * mm, "end": v(-96.51, -26.9) * mm});
            skArc(sketch, "E16.57.0", {"start": v(-95.58, -30.04) * mm, "mid": v(-95.09, -29.55) * mm, "end": v(-95.05, -28.85) * mm});
            skArc(sketch, "E16.57.1", {"start": v(-95.05, -28.82) * mm, "mid": v(-95.05, -28.83) * mm, "end": v(-95.05, -28.85) * mm});
            skArc(sketch, "E16.57.2", {"start": v(-96.16, -28.12) * mm, "mid": v(-95.48, -28.26) * mm, "end": v(-95.05, -28.82) * mm});
            skLineSegment(sketch, "E16.57.3", {"start": v(-96.45, -28.16) * mm, "end": v(-96.16, -28.12) * mm});
            skLineSegment(sketch, "E16.57.4", {"start": v(-95.84, -30.17) * mm, "end": v(-95.58, -30.04) * mm});
            skArc(sketch, "E16.58.0", {"start": v(-94.54, -33.16) * mm, "mid": v(-94.07, -32.64) * mm, "end": v(-94.05, -31.94) * mm});
            skArc(sketch, "E16.58.1", {"start": v(-94.06, -31.91) * mm, "mid": v(-94.06, -31.93) * mm, "end": v(-94.05, -31.94) * mm});
            skArc(sketch, "E16.58.2", {"start": v(-95.2, -31.25) * mm, "mid": v(-94.5, -31.37) * mm, "end": v(-94.06, -31.91) * mm});
            skLineSegment(sketch, "E16.58.3", {"start": v(-95.48, -31.3) * mm, "end": v(-95.2, -31.25) * mm});
            skLineSegment(sketch, "E16.58.4", {"start": v(-94.8, -33.29) * mm, "end": v(-94.54, -33.16) * mm});
            skArc(sketch, "E16.59.0", {"start": v(-93.4, -36.23) * mm, "mid": v(-92.95, -35.7) * mm, "end": v(-92.96, -35) * mm});
            skArc(sketch, "E16.59.1", {"start": v(-92.97, -34.97) * mm, "mid": v(-92.96, -34.99) * mm, "end": v(-92.96, -35) * mm});
            skArc(sketch, "E16.59.2", {"start": v(-94.12, -34.35) * mm, "mid": v(-93.42, -34.45) * mm, "end": v(-92.97, -34.97) * mm});
            skLineSegment(sketch, "E16.59.3", {"start": v(-94.4, -34.41) * mm, "end": v(-94.12, -34.35) * mm});
            skLineSegment(sketch, "E16.59.4", {"start": v(-93.67, -36.37) * mm, "end": v(-93.4, -36.23) * mm});
            skArc(sketch, "E16.60.0", {"start": v(-92.17, -39.27) * mm, "mid": v(-91.73, -38.72) * mm, "end": v(-91.76, -38.02) * mm});
            skArc(sketch, "E16.60.1", {"start": v(-91.77, -38) * mm, "mid": v(-91.77, -38.01) * mm, "end": v(-91.76, -38.02) * mm});
            skArc(sketch, "E16.60.2", {"start": v(-92.94, -37.4) * mm, "mid": v(-92.25, -37.48) * mm, "end": v(-91.77, -38) * mm});
            skLineSegment(sketch, "E16.60.3", {"start": v(-93.23, -37.48) * mm, "end": v(-92.94, -37.4) * mm});
            skLineSegment(sketch, "E16.60.4", {"start": v(-92.43, -39.42) * mm, "end": v(-92.17, -39.27) * mm});
            skArc(sketch, "E16.61.0", {"start": v(-90.84, -42.26) * mm, "mid": v(-90.42, -41.7) * mm, "end": v(-90.47, -41) * mm});
            skArc(sketch, "E16.61.1", {"start": v(-90.48, -40.98) * mm, "mid": v(-90.47, -41) * mm, "end": v(-90.47, -41) * mm});
            skArc(sketch, "E16.61.2", {"start": v(-91.67, -40.43) * mm, "mid": v(-90.97, -40.48) * mm, "end": v(-90.48, -40.98) * mm});
            skLineSegment(sketch, "E16.61.3", {"start": v(-91.95, -40.51) * mm, "end": v(-91.67, -40.43) * mm});
            skLineSegment(sketch, "E16.61.4", {"start": v(-91.09, -42.42) * mm, "end": v(-90.84, -42.26) * mm});
            skArc(sketch, "E16.62.0", {"start": v(-89.4, -45.21) * mm, "mid": v(-89, -44.64) * mm, "end": v(-89.08, -43.94) * mm});
            skArc(sketch, "E16.62.1", {"start": v(-89.09, -43.92) * mm, "mid": v(-89.08, -43.93) * mm, "end": v(-89.08, -43.94) * mm});
            skArc(sketch, "E16.62.2", {"start": v(-90.3, -43.4) * mm, "mid": v(-89.6, -43.44) * mm, "end": v(-89.09, -43.92) * mm});
            skLineSegment(sketch, "E16.62.3", {"start": v(-90.58, -43.5) * mm, "end": v(-90.3, -43.4) * mm});
            skLineSegment(sketch, "E16.62.4", {"start": v(-89.65, -45.38) * mm, "end": v(-89.4, -45.21) * mm});
            skArc(sketch, "E16.63.0", {"start": v(-87.88, -48.11) * mm, "mid": v(-87.5, -47.53) * mm, "end": v(-87.6, -46.84) * mm});
            skArc(sketch, "E16.63.1", {"start": v(-87.6, -46.8) * mm, "mid": v(-87.6, -46.82) * mm, "end": v(-87.6, -46.84) * mm});
            skArc(sketch, "E16.63.2", {"start": v(-88.83, -46.34) * mm, "mid": v(-88.13, -46.35) * mm, "end": v(-87.6, -46.8) * mm});
            skLineSegment(sketch, "E16.63.3", {"start": v(-89.1, -46.44) * mm, "end": v(-88.83, -46.34) * mm});
            skLineSegment(sketch, "E16.63.4", {"start": v(-88.12, -48.29) * mm, "end": v(-87.88, -48.11) * mm});
            skArc(sketch, "E16.64.0", {"start": v(-86.26, -50.96) * mm, "mid": v(-85.9, -50.37) * mm, "end": v(-86.01, -49.68) * mm});
            skArc(sketch, "E16.64.1", {"start": v(-86.03, -49.65) * mm, "mid": v(-86.02, -49.66) * mm, "end": v(-86.01, -49.68) * mm});
            skArc(sketch, "E16.64.2", {"start": v(-87.27, -49.22) * mm, "mid": v(-86.57, -49.2) * mm, "end": v(-86.03, -49.65) * mm});
            skLineSegment(sketch, "E16.64.3", {"start": v(-87.54, -49.33) * mm, "end": v(-87.27, -49.22) * mm});
            skLineSegment(sketch, "E16.64.4", {"start": v(-86.49, -51.14) * mm, "end": v(-86.26, -50.96) * mm});
            skArc(sketch, "E16.65.0", {"start": v(-84.55, -53.76) * mm, "mid": v(-84.2, -53.15) * mm, "end": v(-84.34, -52.46) * mm});
            skArc(sketch, "E16.65.1", {"start": v(-84.36, -52.44) * mm, "mid": v(-84.35, -52.45) * mm, "end": v(-84.34, -52.46) * mm});
            skArc(sketch, "E16.65.2", {"start": v(-85.6, -52.05) * mm, "mid": v(-84.9, -52.01) * mm, "end": v(-84.36, -52.44) * mm});
            skLineSegment(sketch, "E16.65.3", {"start": v(-85.88, -52.17) * mm, "end": v(-85.6, -52.05) * mm});
            skLineSegment(sketch, "E16.65.4", {"start": v(-84.77, -53.95) * mm, "end": v(-84.55, -53.76) * mm});
            skArc(sketch, "E16.66.0", {"start": v(-82.74, -56.5) * mm, "mid": v(-82.42, -55.88) * mm, "end": v(-82.58, -55.2) * mm});
            skArc(sketch, "E16.66.1", {"start": v(-82.6, -55.17) * mm, "mid": v(-82.59, -55.18) * mm, "end": v(-82.58, -55.2) * mm});
            skArc(sketch, "E16.66.2", {"start": v(-83.86, -54.82) * mm, "mid": v(-83.16, -54.76) * mm, "end": v(-82.6, -55.17) * mm});
            skLineSegment(sketch, "E16.66.3", {"start": v(-84.12, -54.95) * mm, "end": v(-83.86, -54.82) * mm});
            skLineSegment(sketch, "E16.66.4", {"start": v(-82.96, -56.7) * mm, "end": v(-82.74, -56.5) * mm});
            skArc(sketch, "E16.67.0", {"start": v(-80.85, -59.17) * mm, "mid": v(-80.55, -58.54) * mm, "end": v(-80.73, -57.87) * mm});
            skArc(sketch, "E16.67.1", {"start": v(-80.75, -57.84) * mm, "mid": v(-80.74, -57.86) * mm, "end": v(-80.73, -57.87) * mm});
            skArc(sketch, "E16.67.2", {"start": v(-82.02, -57.54) * mm, "mid": v(-81.33, -57.45) * mm, "end": v(-80.75, -57.84) * mm});
            skLineSegment(sketch, "E16.67.3", {"start": v(-82.28, -57.67) * mm, "end": v(-82.02, -57.54) * mm});
            skLineSegment(sketch, "E16.67.4", {"start": v(-81.06, -59.38) * mm, "end": v(-80.85, -59.17) * mm});
            skArc(sketch, "E16.68.0", {"start": v(-78.87, -61.79) * mm, "mid": v(-78.59, -61.15) * mm, "end": v(-78.8, -60.48) * mm});
            skArc(sketch, "E16.68.1", {"start": v(-78.81, -60.45) * mm, "mid": v(-78.8, -60.47) * mm, "end": v(-78.8, -60.48) * mm});
            skArc(sketch, "E16.68.2", {"start": v(-80.1, -60.2) * mm, "mid": v(-79.4, -60.08) * mm, "end": v(-78.81, -60.45) * mm});
            skLineSegment(sketch, "E16.68.3", {"start": v(-80.35, -60.33) * mm, "end": v(-80.1, -60.2) * mm});
            skLineSegment(sketch, "E16.68.4", {"start": v(-79.07, -62) * mm, "end": v(-78.87, -61.79) * mm});
            skArc(sketch, "E16.69.0", {"start": v(-76.8, -64.33) * mm, "mid": v(-76.54, -63.69) * mm, "end": v(-76.77, -63.02) * mm});
            skArc(sketch, "E16.69.1", {"start": v(-76.79, -63) * mm, "mid": v(-76.78, -63.01) * mm, "end": v(-76.77, -63.02) * mm});
            skArc(sketch, "E16.69.2", {"start": v(-78.08, -62.78) * mm, "mid": v(-77.4, -62.65) * mm, "end": v(-76.79, -63) * mm});
            skLineSegment(sketch, "E16.69.3", {"start": v(-78.33, -62.93) * mm, "end": v(-78.08, -62.78) * mm});
            skLineSegment(sketch, "E16.69.4", {"start": v(-77, -64.55) * mm, "end": v(-76.8, -64.33) * mm});
            skArc(sketch, "E16.70.0", {"start": v(-74.66, -66.81) * mm, "mid": v(-74.42, -66.16) * mm, "end": v(-74.67, -65.5) * mm});
            skArc(sketch, "E16.70.1", {"start": v(-74.69, -65.48) * mm, "mid": v(-74.68, -65.5) * mm, "end": v(-74.67, -65.5) * mm});
            skArc(sketch, "E16.70.2", {"start": v(-75.99, -65.3) * mm, "mid": v(-75.3, -65.15) * mm, "end": v(-74.69, -65.48) * mm});
            skLineSegment(sketch, "E16.70.3", {"start": v(-76.23, -65.46) * mm, "end": v(-75.99, -65.3) * mm});
            skLineSegment(sketch, "E16.70.4", {"start": v(-74.85, -67.04) * mm, "end": v(-74.66, -66.81) * mm});
            skArc(sketch, "E16.71.0", {"start": v(-72.43, -69.22) * mm, "mid": v(-72.21, -68.55) * mm, "end": v(-72.49, -67.9) * mm});
            skArc(sketch, "E16.71.1", {"start": v(-72.5, -67.89) * mm, "mid": v(-72.5, -67.9) * mm, "end": v(-72.49, -67.9) * mm});
            skArc(sketch, "E16.71.2", {"start": v(-73.8, -67.75) * mm, "mid": v(-73.13, -67.58) * mm, "end": v(-72.5, -67.89) * mm});
            skLineSegment(sketch, "E16.71.3", {"start": v(-74.05, -67.92) * mm, "end": v(-73.8, -67.75) * mm});
            skLineSegment(sketch, "E16.71.4", {"start": v(-72.62, -69.45) * mm, "end": v(-72.43, -69.22) * mm});
            skArc(sketch, "E16.72.0", {"start": v(-70.13, -71.55) * mm, "mid": v(-69.93, -70.88) * mm, "end": v(-70.22, -70.24) * mm});
            skArc(sketch, "E16.72.1", {"start": v(-70.24, -70.22) * mm, "mid": v(-70.23, -70.23) * mm, "end": v(-70.22, -70.24) * mm});
            skArc(sketch, "E16.72.2", {"start": v(-71.55, -70.13) * mm, "mid": v(-70.88, -69.93) * mm, "end": v(-70.24, -70.22) * mm});
            skLineSegment(sketch, "E16.72.3", {"start": v(-71.79, -70.3) * mm, "end": v(-71.55, -70.13) * mm});
            skLineSegment(sketch, "E16.72.4", {"start": v(-70.3, -71.79) * mm, "end": v(-70.13, -71.55) * mm});
            skArc(sketch, "E16.73.0", {"start": v(-67.75, -73.8) * mm, "mid": v(-67.58, -73.13) * mm, "end": v(-67.89, -72.5) * mm});
            skArc(sketch, "E16.73.1", {"start": v(-67.9, -72.49) * mm, "mid": v(-67.9, -72.5) * mm, "end": v(-67.89, -72.5) * mm});
            skArc(sketch, "E16.73.2", {"start": v(-69.22, -72.43) * mm, "mid": v(-68.55, -72.21) * mm, "end": v(-67.9, -72.49) * mm});
            skLineSegment(sketch, "E16.73.3", {"start": v(-69.45, -72.62) * mm, "end": v(-69.22, -72.43) * mm});
            skLineSegment(sketch, "E16.73.4", {"start": v(-67.92, -74.05) * mm, "end": v(-67.75, -73.8) * mm});
            skArc(sketch, "E16.74.0", {"start": v(-65.3, -75.99) * mm, "mid": v(-65.15, -75.3) * mm, "end": v(-65.48, -74.69) * mm});
            skArc(sketch, "E16.74.1", {"start": v(-65.5, -74.67) * mm, "mid": v(-65.5, -74.68) * mm, "end": v(-65.48, -74.69) * mm});
            skArc(sketch, "E16.74.2", {"start": v(-66.81, -74.66) * mm, "mid": v(-66.16, -74.42) * mm, "end": v(-65.5, -74.67) * mm});
            skLineSegment(sketch, "E16.74.3", {"start": v(-67.04, -74.85) * mm, "end": v(-66.81, -74.66) * mm});
            skLineSegment(sketch, "E16.74.4", {"start": v(-65.46, -76.23) * mm, "end": v(-65.3, -75.99) * mm});
            skArc(sketch, "E16.75.0", {"start": v(-62.78, -78.08) * mm, "mid": v(-62.65, -77.4) * mm, "end": v(-63, -76.79) * mm});
            skArc(sketch, "E16.75.1", {"start": v(-63.02, -76.77) * mm, "mid": v(-63.01, -76.78) * mm, "end": v(-63, -76.79) * mm});
            skArc(sketch, "E16.75.2", {"start": v(-64.33, -76.8) * mm, "mid": v(-63.69, -76.54) * mm, "end": v(-63.02, -76.77) * mm});
            skLineSegment(sketch, "E16.75.3", {"start": v(-64.55, -77) * mm, "end": v(-64.33, -76.8) * mm});
            skLineSegment(sketch, "E16.75.4", {"start": v(-62.93, -78.33) * mm, "end": v(-62.78, -78.08) * mm});
            skArc(sketch, "E16.76.0", {"start": v(-60.2, -80.1) * mm, "mid": v(-60.08, -79.4) * mm, "end": v(-60.45, -78.81) * mm});
            skArc(sketch, "E16.76.1", {"start": v(-60.48, -78.8) * mm, "mid": v(-60.47, -78.8) * mm, "end": v(-60.45, -78.81) * mm});
            skArc(sketch, "E16.76.2", {"start": v(-61.79, -78.87) * mm, "mid": v(-61.15, -78.59) * mm, "end": v(-60.48, -78.8) * mm});
            skLineSegment(sketch, "E16.76.3", {"start": v(-62, -79.07) * mm, "end": v(-61.79, -78.87) * mm});
            skLineSegment(sketch, "E16.76.4", {"start": v(-60.33, -80.35) * mm, "end": v(-60.2, -80.1) * mm});
            skArc(sketch, "E16.77.0", {"start": v(-57.54, -82.02) * mm, "mid": v(-57.45, -81.33) * mm, "end": v(-57.84, -80.75) * mm});
            skArc(sketch, "E16.77.1", {"start": v(-57.87, -80.73) * mm, "mid": v(-57.86, -80.74) * mm, "end": v(-57.84, -80.75) * mm});
            skArc(sketch, "E16.77.2", {"start": v(-59.17, -80.85) * mm, "mid": v(-58.54, -80.55) * mm, "end": v(-57.87, -80.73) * mm});
            skLineSegment(sketch, "E16.77.3", {"start": v(-59.38, -81.06) * mm, "end": v(-59.17, -80.85) * mm});
            skLineSegment(sketch, "E16.77.4", {"start": v(-57.67, -82.28) * mm, "end": v(-57.54, -82.02) * mm});
            skArc(sketch, "E16.78.0", {"start": v(-54.82, -83.86) * mm, "mid": v(-54.76, -83.16) * mm, "end": v(-55.17, -82.6) * mm});
            skArc(sketch, "E16.78.1", {"start": v(-55.2, -82.58) * mm, "mid": v(-55.18, -82.59) * mm, "end": v(-55.17, -82.6) * mm});
            skArc(sketch, "E16.78.2", {"start": v(-56.5, -82.74) * mm, "mid": v(-55.88, -82.42) * mm, "end": v(-55.2, -82.58) * mm});
            skLineSegment(sketch, "E16.78.3", {"start": v(-56.7, -82.96) * mm, "end": v(-56.5, -82.74) * mm});
            skLineSegment(sketch, "E16.78.4", {"start": v(-54.95, -84.12) * mm, "end": v(-54.82, -83.86) * mm});
            skArc(sketch, "E16.79.0", {"start": v(-52.05, -85.6) * mm, "mid": v(-52.01, -84.9) * mm, "end": v(-52.44, -84.36) * mm});
            skArc(sketch, "E16.79.1", {"start": v(-52.46, -84.34) * mm, "mid": v(-52.45, -84.35) * mm, "end": v(-52.44, -84.36) * mm});
            skArc(sketch, "E16.79.2", {"start": v(-53.76, -84.55) * mm, "mid": v(-53.15, -84.2) * mm, "end": v(-52.46, -84.34) * mm});
            skLineSegment(sketch, "E16.79.3", {"start": v(-53.95, -84.77) * mm, "end": v(-53.76, -84.55) * mm});
            skLineSegment(sketch, "E16.79.4", {"start": v(-52.17, -85.88) * mm, "end": v(-52.05, -85.6) * mm});
            skArc(sketch, "E16.80.0", {"start": v(-49.22, -87.27) * mm, "mid": v(-49.2, -86.57) * mm, "end": v(-49.65, -86.03) * mm});
            skArc(sketch, "E16.80.1", {"start": v(-49.68, -86.01) * mm, "mid": v(-49.66, -86.02) * mm, "end": v(-49.65, -86.03) * mm});
            skArc(sketch, "E16.80.2", {"start": v(-50.96, -86.26) * mm, "mid": v(-50.37, -85.9) * mm, "end": v(-49.68, -86.01) * mm});
            skLineSegment(sketch, "E16.80.3", {"start": v(-51.14, -86.49) * mm, "end": v(-50.96, -86.26) * mm});
            skLineSegment(sketch, "E16.80.4", {"start": v(-49.33, -87.54) * mm, "end": v(-49.22, -87.27) * mm});
            skArc(sketch, "E16.81.0", {"start": v(-46.34, -88.83) * mm, "mid": v(-46.35, -88.13) * mm, "end": v(-46.8, -87.6) * mm});
            skArc(sketch, "E16.81.1", {"start": v(-46.84, -87.6) * mm, "mid": v(-46.82, -87.6) * mm, "end": v(-46.8, -87.6) * mm});
            skArc(sketch, "E16.81.2", {"start": v(-48.11, -87.88) * mm, "mid": v(-47.53, -87.5) * mm, "end": v(-46.84, -87.6) * mm});
            skLineSegment(sketch, "E16.81.3", {"start": v(-48.29, -88.12) * mm, "end": v(-48.11, -87.88) * mm});
            skLineSegment(sketch, "E16.81.4", {"start": v(-46.44, -89.1) * mm, "end": v(-46.34, -88.83) * mm});
            skArc(sketch, "E16.82.0", {"start": v(-43.4, -90.3) * mm, "mid": v(-43.44, -89.6) * mm, "end": v(-43.92, -89.09) * mm});
            skArc(sketch, "E16.82.1", {"start": v(-43.94, -89.08) * mm, "mid": v(-43.93, -89.08) * mm, "end": v(-43.92, -89.09) * mm});
            skArc(sketch, "E16.82.2", {"start": v(-45.21, -89.4) * mm, "mid": v(-44.64, -89) * mm, "end": v(-43.94, -89.08) * mm});
            skLineSegment(sketch, "E16.82.3", {"start": v(-45.38, -89.65) * mm, "end": v(-45.21, -89.4) * mm});
            skLineSegment(sketch, "E16.82.4", {"start": v(-43.5, -90.58) * mm, "end": v(-43.4, -90.3) * mm});
            skArc(sketch, "E16.83.0", {"start": v(-40.43, -91.67) * mm, "mid": v(-40.48, -90.97) * mm, "end": v(-40.98, -90.48) * mm});
            skArc(sketch, "E16.83.1", {"start": v(-41, -90.47) * mm, "mid": v(-41, -90.47) * mm, "end": v(-40.98, -90.48) * mm});
            skArc(sketch, "E16.83.2", {"start": v(-42.26, -90.84) * mm, "mid": v(-41.7, -90.42) * mm, "end": v(-41, -90.47) * mm});
            skLineSegment(sketch, "E16.83.3", {"start": v(-42.42, -91.09) * mm, "end": v(-42.26, -90.84) * mm});
            skLineSegment(sketch, "E16.83.4", {"start": v(-40.51, -91.95) * mm, "end": v(-40.43, -91.67) * mm});
            skArc(sketch, "E16.84.0", {"start": v(-37.4, -92.94) * mm, "mid": v(-37.48, -92.25) * mm, "end": v(-38, -91.77) * mm});
            skArc(sketch, "E16.84.1", {"start": v(-38.02, -91.76) * mm, "mid": v(-38.01, -91.77) * mm, "end": v(-38, -91.77) * mm});
            skArc(sketch, "E16.84.2", {"start": v(-39.27, -92.17) * mm, "mid": v(-38.72, -91.73) * mm, "end": v(-38.02, -91.76) * mm});
            skLineSegment(sketch, "E16.84.3", {"start": v(-39.42, -92.43) * mm, "end": v(-39.27, -92.17) * mm});
            skLineSegment(sketch, "E16.84.4", {"start": v(-37.48, -93.23) * mm, "end": v(-37.4, -92.94) * mm});
            skArc(sketch, "E16.85.0", {"start": v(-34.35, -94.12) * mm, "mid": v(-34.45, -93.42) * mm, "end": v(-34.97, -92.97) * mm});
            skArc(sketch, "E16.85.1", {"start": v(-35, -92.96) * mm, "mid": v(-34.99, -92.96) * mm, "end": v(-34.97, -92.97) * mm});
            skArc(sketch, "E16.85.2", {"start": v(-36.23, -93.4) * mm, "mid": v(-35.7, -92.95) * mm, "end": v(-35, -92.96) * mm});
            skLineSegment(sketch, "E16.85.3", {"start": v(-36.37, -93.67) * mm, "end": v(-36.23, -93.4) * mm});
            skLineSegment(sketch, "E16.85.4", {"start": v(-34.41, -94.4) * mm, "end": v(-34.35, -94.12) * mm});
            skArc(sketch, "E16.86.0", {"start": v(-31.25, -95.2) * mm, "mid": v(-31.37, -94.5) * mm, "end": v(-31.91, -94.06) * mm});
            skArc(sketch, "E16.86.1", {"start": v(-31.94, -94.05) * mm, "mid": v(-31.93, -94.06) * mm, "end": v(-31.91, -94.06) * mm});
            skArc(sketch, "E16.86.2", {"start": v(-33.16, -94.54) * mm, "mid": v(-32.64, -94.07) * mm, "end": v(-31.94, -94.05) * mm});
            skLineSegment(sketch, "E16.86.3", {"start": v(-33.29, -94.8) * mm, "end": v(-33.16, -94.54) * mm});
            skLineSegment(sketch, "E16.86.4", {"start": v(-31.3, -95.48) * mm, "end": v(-31.25, -95.2) * mm});
            skArc(sketch, "E16.87.0", {"start": v(-28.12, -96.16) * mm, "mid": v(-28.26, -95.48) * mm, "end": v(-28.82, -95.05) * mm});
            skArc(sketch, "E16.87.1", {"start": v(-28.85, -95.05) * mm, "mid": v(-28.83, -95.05) * mm, "end": v(-28.82, -95.05) * mm});
            skArc(sketch, "E16.87.2", {"start": v(-30.04, -95.58) * mm, "mid": v(-29.55, -95.09) * mm, "end": v(-28.85, -95.05) * mm});
            skLineSegment(sketch, "E16.87.3", {"start": v(-30.17, -95.84) * mm, "end": v(-30.04, -95.58) * mm});
            skLineSegment(sketch, "E16.87.4", {"start": v(-28.16, -96.45) * mm, "end": v(-28.12, -96.16) * mm});
            skArc(sketch, "E16.88.0", {"start": v(-24.96, -97.03) * mm, "mid": v(-25.12, -96.35) * mm, "end": v(-25.7, -95.95) * mm});
            skArc(sketch, "E16.88.1", {"start": v(-25.72, -95.94) * mm, "mid": v(-25.7, -95.94) * mm, "end": v(-25.7, -95.95) * mm});
            skArc(sketch, "E16.88.2", {"start": v(-26.9, -96.51) * mm, "mid": v(-26.42, -96) * mm, "end": v(-25.72, -95.94) * mm});
            skLineSegment(sketch, "E16.88.3", {"start": v(-27.02, -96.78) * mm, "end": v(-26.9, -96.51) * mm});
            skLineSegment(sketch, "E16.88.4", {"start": v(-25, -97.32) * mm, "end": v(-24.96, -97.03) * mm});
            skArc(sketch, "E16.89.0", {"start": v(-21.77, -97.8) * mm, "mid": v(-21.96, -97.12) * mm, "end": v(-22.54, -96.74) * mm});
            skArc(sketch, "E16.89.1", {"start": v(-22.57, -96.73) * mm, "mid": v(-22.55, -96.73) * mm, "end": v(-22.54, -96.74) * mm});
            skArc(sketch, "E16.89.2", {"start": v(-23.73, -97.34) * mm, "mid": v(-23.26, -96.82) * mm, "end": v(-22.57, -96.73) * mm});
            skLineSegment(sketch, "E16.89.3", {"start": v(-23.84, -97.61) * mm, "end": v(-23.73, -97.34) * mm});
            skLineSegment(sketch, "E16.89.4", {"start": v(-21.8, -98.09) * mm, "end": v(-21.77, -97.8) * mm});
            skArc(sketch, "E16.90.0", {"start": v(-18.56, -98.46) * mm, "mid": v(-18.77, -97.79) * mm, "end": v(-19.36, -97.42) * mm});
            skArc(sketch, "E16.90.1", {"start": v(-19.4, -97.42) * mm, "mid": v(-19.38, -97.42) * mm, "end": v(-19.36, -97.42) * mm});
            skArc(sketch, "E16.90.2", {"start": v(-20.53, -98.06) * mm, "mid": v(-20.08, -97.53) * mm, "end": v(-19.4, -97.42) * mm});
            skLineSegment(sketch, "E16.90.3", {"start": v(-20.63, -98.34) * mm, "end": v(-20.53, -98.06) * mm});
            skLineSegment(sketch, "E16.90.4", {"start": v(-18.57, -98.75) * mm, "end": v(-18.56, -98.46) * mm});
            skArc(sketch, "E16.91.0", {"start": v(-15.33, -99.01) * mm, "mid": v(-15.56, -98.35) * mm, "end": v(-16.17, -98) * mm});
            skArc(sketch, "E16.91.1", {"start": v(-16.2, -98) * mm, "mid": v(-16.18, -98) * mm, "end": v(-16.17, -98) * mm});
            skArc(sketch, "E16.91.2", {"start": v(-17.31, -98.68) * mm, "mid": v(-16.88, -98.13) * mm, "end": v(-16.2, -98) * mm});
            skLineSegment(sketch, "E16.91.3", {"start": v(-17.4, -98.96) * mm, "end": v(-17.31, -98.68) * mm});
            skLineSegment(sketch, "E16.91.4", {"start": v(-15.33, -99.3) * mm, "end": v(-15.33, -99.01) * mm});
            skArc(sketch, "E16.92.0", {"start": v(-12.08, -99.46) * mm, "mid": v(-12.33, -98.8) * mm, "end": v(-12.95, -98.48) * mm});
            skArc(sketch, "E16.92.1", {"start": v(-12.98, -98.48) * mm, "mid": v(-12.96, -98.48) * mm, "end": v(-12.95, -98.48) * mm});
            skArc(sketch, "E16.92.2", {"start": v(-14.07, -99.2) * mm, "mid": v(-13.66, -98.63) * mm, "end": v(-12.98, -98.48) * mm});
            skLineSegment(sketch, "E16.92.3", {"start": v(-14.15, -99.48) * mm, "end": v(-14.07, -99.2) * mm});
            skLineSegment(sketch, "E16.92.4", {"start": v(-12.08, -99.75) * mm, "end": v(-12.08, -99.46) * mm});
            skArc(sketch, "E16.93.0", {"start": v(-8.82, -99.8) * mm, "mid": v(-9.1, -99.16) * mm, "end": v(-9.72, -98.85) * mm});
            skArc(sketch, "E16.93.1", {"start": v(-9.75, -98.85) * mm, "mid": v(-9.74, -98.85) * mm, "end": v(-9.72, -98.85) * mm});
            skArc(sketch, "E16.93.2", {"start": v(-10.82, -99.6) * mm, "mid": v(-10.43, -99.03) * mm, "end": v(-9.75, -98.85) * mm});
            skLineSegment(sketch, "E16.93.3", {"start": v(-10.9, -99.89) * mm, "end": v(-10.82, -99.6) * mm});
            skLineSegment(sketch, "E16.93.4", {"start": v(-8.8, -100.1) * mm, "end": v(-8.82, -99.8) * mm});
            skArc(sketch, "E16.94.0", {"start": v(-5.55, -100.04) * mm, "mid": v(-5.84, -99.4) * mm, "end": v(-6.48, -99.12) * mm});
            skArc(sketch, "E16.94.1", {"start": v(-6.51, -99.11) * mm, "mid": v(-6.5, -99.11) * mm, "end": v(-6.48, -99.12) * mm});
            skArc(sketch, "E16.94.2", {"start": v(-7.56, -99.9) * mm, "mid": v(-7.18, -99.31) * mm, "end": v(-6.51, -99.11) * mm});
            skLineSegment(sketch, "E16.94.3", {"start": v(-7.62, -100.2) * mm, "end": v(-7.56, -99.9) * mm});
            skLineSegment(sketch, "E16.94.4", {"start": v(-5.53, -100.33) * mm, "end": v(-5.55, -100.04) * mm});
            skArc(sketch, "E16.95.0", {"start": v(-2.27, -100.16) * mm, "mid": v(-2.59, -99.54) * mm, "end": v(-3.24, -99.27) * mm});
            skArc(sketch, "E16.95.1", {"start": v(-3.26, -99.27) * mm, "mid": v(-3.25, -99.27) * mm, "end": v(-3.24, -99.27) * mm});
            skArc(sketch, "E16.95.2", {"start": v(-4.28, -100.1) * mm, "mid": v(-3.93, -99.5) * mm, "end": v(-3.26, -99.27) * mm});
            skLineSegment(sketch, "E16.95.3", {"start": v(-4.33, -100.39) * mm, "end": v(-4.28, -100.1) * mm});
            skLineSegment(sketch, "E16.95.4", {"start": v(-2.24, -100.46) * mm, "end": v(-2.27, -100.16) * mm});
            skArc(sketch, "E16.96.0", {"start": v(1, -100.18) * mm, "mid": v(0.67, -99.57) * mm, "end": v(0.01, -99.33) * mm});
            skArc(sketch, "E16.96.1", {"start": v(-0.01, -99.33) * mm, "mid": v(0, -99.33) * mm, "end": v(0.01, -99.33) * mm});
            skArc(sketch, "E16.96.2", {"start": v(-1, -100.18) * mm, "mid": v(-0.67, -99.57) * mm, "end": v(-0.01, -99.33) * mm});
            skLineSegment(sketch, "E16.96.3", {"start": v(-1.05, -100.47) * mm, "end": v(-1, -100.18) * mm});
            skLineSegment(sketch, "E16.96.4", {"start": v(1.05, -100.47) * mm, "end": v(1, -100.18) * mm});
            skArc(sketch, "E16.97.0", {"start": v(4.28, -100.1) * mm, "mid": v(3.93, -99.5) * mm, "end": v(3.26, -99.27) * mm});
            skArc(sketch, "E16.97.1", {"start": v(3.24, -99.27) * mm, "mid": v(3.25, -99.27) * mm, "end": v(3.26, -99.27) * mm});
            skArc(sketch, "E16.97.2", {"start": v(2.27, -100.16) * mm, "mid": v(2.59, -99.54) * mm, "end": v(3.24, -99.27) * mm});
            skLineSegment(sketch, "E16.97.3", {"start": v(2.24, -100.46) * mm, "end": v(2.27, -100.16) * mm});
            skLineSegment(sketch, "E16.97.4", {"start": v(4.33, -100.39) * mm, "end": v(4.28, -100.1) * mm});
            skArc(sketch, "E16.98.0", {"start": v(7.56, -99.9) * mm, "mid": v(7.18, -99.31) * mm, "end": v(6.51, -99.11) * mm});
            skArc(sketch, "E16.98.1", {"start": v(6.48, -99.12) * mm, "mid": v(6.5, -99.11) * mm, "end": v(6.51, -99.11) * mm});
            skArc(sketch, "E16.98.2", {"start": v(5.55, -100.04) * mm, "mid": v(5.84, -99.4) * mm, "end": v(6.48, -99.12) * mm});
            skLineSegment(sketch, "E16.98.3", {"start": v(5.53, -100.33) * mm, "end": v(5.55, -100.04) * mm});
            skLineSegment(sketch, "E16.98.4", {"start": v(7.62, -100.2) * mm, "end": v(7.56, -99.9) * mm});
            skArc(sketch, "E16.99.0", {"start": v(10.82, -99.6) * mm, "mid": v(10.43, -99.03) * mm, "end": v(9.75, -98.85) * mm});
            skArc(sketch, "E16.99.1", {"start": v(9.72, -98.85) * mm, "mid": v(9.74, -98.85) * mm, "end": v(9.75, -98.85) * mm});
            skArc(sketch, "E16.99.2", {"start": v(8.82, -99.8) * mm, "mid": v(9.1, -99.16) * mm, "end": v(9.72, -98.85) * mm});
            skLineSegment(sketch, "E16.99.3", {"start": v(8.8, -100.1) * mm, "end": v(8.82, -99.8) * mm});
            skLineSegment(sketch, "E16.99.4", {"start": v(10.9, -99.89) * mm, "end": v(10.82, -99.6) * mm});
            skArc(sketch, "E16.100.0", {"start": v(14.07, -99.2) * mm, "mid": v(13.66, -98.63) * mm, "end": v(12.98, -98.48) * mm});
            skArc(sketch, "E16.100.1", {"start": v(12.95, -98.48) * mm, "mid": v(12.96, -98.48) * mm, "end": v(12.98, -98.48) * mm});
            skArc(sketch, "E16.100.2", {"start": v(12.08, -99.46) * mm, "mid": v(12.33, -98.8) * mm, "end": v(12.95, -98.48) * mm});
            skLineSegment(sketch, "E16.100.3", {"start": v(12.08, -99.75) * mm, "end": v(12.08, -99.46) * mm});
            skLineSegment(sketch, "E16.100.4", {"start": v(14.15, -99.48) * mm, "end": v(14.07, -99.2) * mm});
            skArc(sketch, "E16.101.0", {"start": v(17.31, -98.68) * mm, "mid": v(16.88, -98.13) * mm, "end": v(16.2, -98) * mm});
            skArc(sketch, "E16.101.1", {"start": v(16.17, -98) * mm, "mid": v(16.18, -98) * mm, "end": v(16.2, -98) * mm});
            skArc(sketch, "E16.101.2", {"start": v(15.33, -99.01) * mm, "mid": v(15.56, -98.35) * mm, "end": v(16.17, -98) * mm});
            skLineSegment(sketch, "E16.101.3", {"start": v(15.33, -99.3) * mm, "end": v(15.33, -99.01) * mm});
            skLineSegment(sketch, "E16.101.4", {"start": v(17.4, -98.96) * mm, "end": v(17.31, -98.68) * mm});
            skArc(sketch, "E16.102.0", {"start": v(20.53, -98.06) * mm, "mid": v(20.08, -97.53) * mm, "end": v(19.4, -97.42) * mm});
            skArc(sketch, "E16.102.1", {"start": v(19.36, -97.42) * mm, "mid": v(19.38, -97.42) * mm, "end": v(19.4, -97.42) * mm});
            skArc(sketch, "E16.102.2", {"start": v(18.56, -98.46) * mm, "mid": v(18.77, -97.79) * mm, "end": v(19.36, -97.42) * mm});
            skLineSegment(sketch, "E16.102.3", {"start": v(18.57, -98.75) * mm, "end": v(18.56, -98.46) * mm});
            skLineSegment(sketch, "E16.102.4", {"start": v(20.63, -98.34) * mm, "end": v(20.53, -98.06) * mm});
            skArc(sketch, "E16.103.0", {"start": v(23.73, -97.34) * mm, "mid": v(23.26, -96.82) * mm, "end": v(22.57, -96.73) * mm});
            skArc(sketch, "E16.103.1", {"start": v(22.54, -96.74) * mm, "mid": v(22.55, -96.73) * mm, "end": v(22.57, -96.73) * mm});
            skArc(sketch, "E16.103.2", {"start": v(21.77, -97.8) * mm, "mid": v(21.96, -97.12) * mm, "end": v(22.54, -96.74) * mm});
            skLineSegment(sketch, "E16.103.3", {"start": v(21.8, -98.09) * mm, "end": v(21.77, -97.8) * mm});
            skLineSegment(sketch, "E16.103.4", {"start": v(23.84, -97.61) * mm, "end": v(23.73, -97.34) * mm});
            skArc(sketch, "E16.104.0", {"start": v(26.9, -96.51) * mm, "mid": v(26.42, -96) * mm, "end": v(25.72, -95.94) * mm});
            skArc(sketch, "E16.104.1", {"start": v(25.7, -95.95) * mm, "mid": v(25.7, -95.94) * mm, "end": v(25.72, -95.94) * mm});
            skArc(sketch, "E16.104.2", {"start": v(24.96, -97.03) * mm, "mid": v(25.12, -96.35) * mm, "end": v(25.7, -95.95) * mm});
            skLineSegment(sketch, "E16.104.3", {"start": v(25, -97.32) * mm, "end": v(24.96, -97.03) * mm});
            skLineSegment(sketch, "E16.104.4", {"start": v(27.02, -96.78) * mm, "end": v(26.9, -96.51) * mm});
            skArc(sketch, "E16.105.0", {"start": v(30.04, -95.58) * mm, "mid": v(29.55, -95.09) * mm, "end": v(28.85, -95.05) * mm});
            skArc(sketch, "E16.105.1", {"start": v(28.82, -95.05) * mm, "mid": v(28.83, -95.05) * mm, "end": v(28.85, -95.05) * mm});
            skArc(sketch, "E16.105.2", {"start": v(28.12, -96.16) * mm, "mid": v(28.26, -95.48) * mm, "end": v(28.82, -95.05) * mm});
            skLineSegment(sketch, "E16.105.3", {"start": v(28.16, -96.45) * mm, "end": v(28.12, -96.16) * mm});
            skLineSegment(sketch, "E16.105.4", {"start": v(30.17, -95.84) * mm, "end": v(30.04, -95.58) * mm});
            skArc(sketch, "E16.106.0", {"start": v(33.16, -94.54) * mm, "mid": v(32.64, -94.07) * mm, "end": v(31.94, -94.05) * mm});
            skArc(sketch, "E16.106.1", {"start": v(31.91, -94.06) * mm, "mid": v(31.93, -94.06) * mm, "end": v(31.94, -94.05) * mm});
            skArc(sketch, "E16.106.2", {"start": v(31.25, -95.2) * mm, "mid": v(31.37, -94.5) * mm, "end": v(31.91, -94.06) * mm});
            skLineSegment(sketch, "E16.106.3", {"start": v(31.3, -95.48) * mm, "end": v(31.25, -95.2) * mm});
            skLineSegment(sketch, "E16.106.4", {"start": v(33.29, -94.8) * mm, "end": v(33.16, -94.54) * mm});
            skArc(sketch, "E16.107.0", {"start": v(36.23, -93.4) * mm, "mid": v(35.7, -92.95) * mm, "end": v(35, -92.96) * mm});
            skArc(sketch, "E16.107.1", {"start": v(34.97, -92.97) * mm, "mid": v(34.99, -92.96) * mm, "end": v(35, -92.96) * mm});
            skArc(sketch, "E16.107.2", {"start": v(34.35, -94.12) * mm, "mid": v(34.45, -93.42) * mm, "end": v(34.97, -92.97) * mm});
            skLineSegment(sketch, "E16.107.3", {"start": v(34.41, -94.4) * mm, "end": v(34.35, -94.12) * mm});
            skLineSegment(sketch, "E16.107.4", {"start": v(36.37, -93.67) * mm, "end": v(36.23, -93.4) * mm});
            skArc(sketch, "E16.108.0", {"start": v(39.27, -92.17) * mm, "mid": v(38.72, -91.73) * mm, "end": v(38.02, -91.76) * mm});
            skArc(sketch, "E16.108.1", {"start": v(38, -91.77) * mm, "mid": v(38.01, -91.77) * mm, "end": v(38.02, -91.76) * mm});
            skArc(sketch, "E16.108.2", {"start": v(37.4, -92.94) * mm, "mid": v(37.48, -92.25) * mm, "end": v(38, -91.77) * mm});
            skLineSegment(sketch, "E16.108.3", {"start": v(37.48, -93.23) * mm, "end": v(37.4, -92.94) * mm});
            skLineSegment(sketch, "E16.108.4", {"start": v(39.42, -92.43) * mm, "end": v(39.27, -92.17) * mm});
            skArc(sketch, "E16.109.0", {"start": v(42.26, -90.84) * mm, "mid": v(41.7, -90.42) * mm, "end": v(41, -90.47) * mm});
            skArc(sketch, "E16.109.1", {"start": v(40.98, -90.48) * mm, "mid": v(41, -90.47) * mm, "end": v(41, -90.47) * mm});
            skArc(sketch, "E16.109.2", {"start": v(40.43, -91.67) * mm, "mid": v(40.48, -90.97) * mm, "end": v(40.98, -90.48) * mm});
            skLineSegment(sketch, "E16.109.3", {"start": v(40.51, -91.95) * mm, "end": v(40.43, -91.67) * mm});
            skLineSegment(sketch, "E16.109.4", {"start": v(42.42, -91.09) * mm, "end": v(42.26, -90.84) * mm});
            skArc(sketch, "E16.110.0", {"start": v(45.21, -89.4) * mm, "mid": v(44.64, -89) * mm, "end": v(43.94, -89.08) * mm});
            skArc(sketch, "E16.110.1", {"start": v(43.92, -89.09) * mm, "mid": v(43.93, -89.08) * mm, "end": v(43.94, -89.08) * mm});
            skArc(sketch, "E16.110.2", {"start": v(43.4, -90.3) * mm, "mid": v(43.44, -89.6) * mm, "end": v(43.92, -89.09) * mm});
            skLineSegment(sketch, "E16.110.3", {"start": v(43.5, -90.58) * mm, "end": v(43.4, -90.3) * mm});
            skLineSegment(sketch, "E16.110.4", {"start": v(45.38, -89.65) * mm, "end": v(45.21, -89.4) * mm});
            skArc(sketch, "E16.111.0", {"start": v(48.11, -87.88) * mm, "mid": v(47.53, -87.5) * mm, "end": v(46.84, -87.6) * mm});
            skArc(sketch, "E16.111.1", {"start": v(46.8, -87.6) * mm, "mid": v(46.82, -87.6) * mm, "end": v(46.84, -87.6) * mm});
            skArc(sketch, "E16.111.2", {"start": v(46.34, -88.83) * mm, "mid": v(46.35, -88.13) * mm, "end": v(46.8, -87.6) * mm});
            skLineSegment(sketch, "E16.111.3", {"start": v(46.44, -89.1) * mm, "end": v(46.34, -88.83) * mm});
            skLineSegment(sketch, "E16.111.4", {"start": v(48.29, -88.12) * mm, "end": v(48.11, -87.88) * mm});
            skArc(sketch, "E16.112.0", {"start": v(50.96, -86.26) * mm, "mid": v(50.37, -85.9) * mm, "end": v(49.68, -86.01) * mm});
            skArc(sketch, "E16.112.1", {"start": v(49.65, -86.03) * mm, "mid": v(49.66, -86.02) * mm, "end": v(49.68, -86.01) * mm});
            skArc(sketch, "E16.112.2", {"start": v(49.22, -87.27) * mm, "mid": v(49.2, -86.57) * mm, "end": v(49.65, -86.03) * mm});
            skLineSegment(sketch, "E16.112.3", {"start": v(49.33, -87.54) * mm, "end": v(49.22, -87.27) * mm});
            skLineSegment(sketch, "E16.112.4", {"start": v(51.14, -86.49) * mm, "end": v(50.96, -86.26) * mm});
            skArc(sketch, "E16.113.0", {"start": v(53.76, -84.55) * mm, "mid": v(53.15, -84.2) * mm, "end": v(52.46, -84.34) * mm});
            skArc(sketch, "E16.113.1", {"start": v(52.44, -84.36) * mm, "mid": v(52.45, -84.35) * mm, "end": v(52.46, -84.34) * mm});
            skArc(sketch, "E16.113.2", {"start": v(52.05, -85.6) * mm, "mid": v(52.01, -84.9) * mm, "end": v(52.44, -84.36) * mm});
            skLineSegment(sketch, "E16.113.3", {"start": v(52.17, -85.88) * mm, "end": v(52.05, -85.6) * mm});
            skLineSegment(sketch, "E16.113.4", {"start": v(53.95, -84.77) * mm, "end": v(53.76, -84.55) * mm});
            skArc(sketch, "E16.114.0", {"start": v(56.5, -82.74) * mm, "mid": v(55.88, -82.42) * mm, "end": v(55.2, -82.58) * mm});
            skArc(sketch, "E16.114.1", {"start": v(55.17, -82.6) * mm, "mid": v(55.18, -82.59) * mm, "end": v(55.2, -82.58) * mm});
            skArc(sketch, "E16.114.2", {"start": v(54.82, -83.86) * mm, "mid": v(54.76, -83.16) * mm, "end": v(55.17, -82.6) * mm});
            skLineSegment(sketch, "E16.114.3", {"start": v(54.95, -84.12) * mm, "end": v(54.82, -83.86) * mm});
            skLineSegment(sketch, "E16.114.4", {"start": v(56.7, -82.96) * mm, "end": v(56.5, -82.74) * mm});
            skArc(sketch, "E16.115.0", {"start": v(59.17, -80.85) * mm, "mid": v(58.54, -80.55) * mm, "end": v(57.87, -80.73) * mm});
            skArc(sketch, "E16.115.1", {"start": v(57.84, -80.75) * mm, "mid": v(57.86, -80.74) * mm, "end": v(57.87, -80.73) * mm});
            skArc(sketch, "E16.115.2", {"start": v(57.54, -82.02) * mm, "mid": v(57.45, -81.33) * mm, "end": v(57.84, -80.75) * mm});
            skLineSegment(sketch, "E16.115.3", {"start": v(57.67, -82.28) * mm, "end": v(57.54, -82.02) * mm});
            skLineSegment(sketch, "E16.115.4", {"start": v(59.38, -81.06) * mm, "end": v(59.17, -80.85) * mm});
            skArc(sketch, "E16.116.0", {"start": v(61.79, -78.87) * mm, "mid": v(61.15, -78.59) * mm, "end": v(60.48, -78.8) * mm});
            skArc(sketch, "E16.116.1", {"start": v(60.45, -78.81) * mm, "mid": v(60.47, -78.8) * mm, "end": v(60.48, -78.8) * mm});
            skArc(sketch, "E16.116.2", {"start": v(60.2, -80.1) * mm, "mid": v(60.08, -79.4) * mm, "end": v(60.45, -78.81) * mm});
            skLineSegment(sketch, "E16.116.3", {"start": v(60.33, -80.35) * mm, "end": v(60.2, -80.1) * mm});
            skLineSegment(sketch, "E16.116.4", {"start": v(62, -79.07) * mm, "end": v(61.79, -78.87) * mm});
            skArc(sketch, "E16.117.0", {"start": v(64.33, -76.8) * mm, "mid": v(63.69, -76.54) * mm, "end": v(63.02, -76.77) * mm});
            skArc(sketch, "E16.117.1", {"start": v(63, -76.79) * mm, "mid": v(63.01, -76.78) * mm, "end": v(63.02, -76.77) * mm});
            skArc(sketch, "E16.117.2", {"start": v(62.78, -78.08) * mm, "mid": v(62.65, -77.4) * mm, "end": v(63, -76.79) * mm});
            skLineSegment(sketch, "E16.117.3", {"start": v(62.93, -78.33) * mm, "end": v(62.78, -78.08) * mm});
            skLineSegment(sketch, "E16.117.4", {"start": v(64.55, -77) * mm, "end": v(64.33, -76.8) * mm});
            skArc(sketch, "E16.118.0", {"start": v(66.81, -74.66) * mm, "mid": v(66.16, -74.42) * mm, "end": v(65.5, -74.67) * mm});
            skArc(sketch, "E16.118.1", {"start": v(65.48, -74.69) * mm, "mid": v(65.5, -74.68) * mm, "end": v(65.5, -74.67) * mm});
            skArc(sketch, "E16.118.2", {"start": v(65.3, -75.99) * mm, "mid": v(65.15, -75.3) * mm, "end": v(65.48, -74.69) * mm});
            skLineSegment(sketch, "E16.118.3", {"start": v(65.46, -76.23) * mm, "end": v(65.3, -75.99) * mm});
            skLineSegment(sketch, "E16.118.4", {"start": v(67.04, -74.85) * mm, "end": v(66.81, -74.66) * mm});
            skArc(sketch, "E16.119.0", {"start": v(69.22, -72.43) * mm, "mid": v(68.55, -72.21) * mm, "end": v(67.9, -72.49) * mm});
            skArc(sketch, "E16.119.1", {"start": v(67.89, -72.5) * mm, "mid": v(67.9, -72.5) * mm, "end": v(67.9, -72.49) * mm});
            skArc(sketch, "E16.119.2", {"start": v(67.75, -73.8) * mm, "mid": v(67.58, -73.13) * mm, "end": v(67.89, -72.5) * mm});
            skLineSegment(sketch, "E16.119.3", {"start": v(67.92, -74.05) * mm, "end": v(67.75, -73.8) * mm});
            skLineSegment(sketch, "E16.119.4", {"start": v(69.45, -72.62) * mm, "end": v(69.22, -72.43) * mm});
            skArc(sketch, "E16.120.0", {"start": v(71.55, -70.13) * mm, "mid": v(70.88, -69.93) * mm, "end": v(70.24, -70.22) * mm});
            skArc(sketch, "E16.120.1", {"start": v(70.22, -70.24) * mm, "mid": v(70.23, -70.23) * mm, "end": v(70.24, -70.22) * mm});
            skArc(sketch, "E16.120.2", {"start": v(70.13, -71.55) * mm, "mid": v(69.93, -70.88) * mm, "end": v(70.22, -70.24) * mm});
            skLineSegment(sketch, "E16.120.3", {"start": v(70.3, -71.79) * mm, "end": v(70.13, -71.55) * mm});
            skLineSegment(sketch, "E16.120.4", {"start": v(71.79, -70.3) * mm, "end": v(71.55, -70.13) * mm});
            skArc(sketch, "E16.121.0", {"start": v(73.8, -67.75) * mm, "mid": v(73.13, -67.58) * mm, "end": v(72.5, -67.89) * mm});
            skArc(sketch, "E16.121.1", {"start": v(72.49, -67.9) * mm, "mid": v(72.5, -67.9) * mm, "end": v(72.5, -67.89) * mm});
            skArc(sketch, "E16.121.2", {"start": v(72.43, -69.22) * mm, "mid": v(72.21, -68.55) * mm, "end": v(72.49, -67.9) * mm});
            skLineSegment(sketch, "E16.121.3", {"start": v(72.62, -69.45) * mm, "end": v(72.43, -69.22) * mm});
            skLineSegment(sketch, "E16.121.4", {"start": v(74.05, -67.92) * mm, "end": v(73.8, -67.75) * mm});
            skArc(sketch, "E16.122.0", {"start": v(75.99, -65.3) * mm, "mid": v(75.3, -65.15) * mm, "end": v(74.69, -65.48) * mm});
            skArc(sketch, "E16.122.1", {"start": v(74.67, -65.5) * mm, "mid": v(74.68, -65.5) * mm, "end": v(74.69, -65.48) * mm});
            skArc(sketch, "E16.122.2", {"start": v(74.66, -66.81) * mm, "mid": v(74.42, -66.16) * mm, "end": v(74.67, -65.5) * mm});
            skLineSegment(sketch, "E16.122.3", {"start": v(74.85, -67.04) * mm, "end": v(74.66, -66.81) * mm});
            skLineSegment(sketch, "E16.122.4", {"start": v(76.23, -65.46) * mm, "end": v(75.99, -65.3) * mm});
            skArc(sketch, "E16.123.0", {"start": v(78.08, -62.78) * mm, "mid": v(77.4, -62.65) * mm, "end": v(76.79, -63) * mm});
            skArc(sketch, "E16.123.1", {"start": v(76.77, -63.02) * mm, "mid": v(76.78, -63.01) * mm, "end": v(76.79, -63) * mm});
            skArc(sketch, "E16.123.2", {"start": v(76.8, -64.33) * mm, "mid": v(76.54, -63.69) * mm, "end": v(76.77, -63.02) * mm});
            skLineSegment(sketch, "E16.123.3", {"start": v(77, -64.55) * mm, "end": v(76.8, -64.33) * mm});
            skLineSegment(sketch, "E16.123.4", {"start": v(78.33, -62.93) * mm, "end": v(78.08, -62.78) * mm});
            skArc(sketch, "E16.124.0", {"start": v(80.1, -60.2) * mm, "mid": v(79.4, -60.08) * mm, "end": v(78.81, -60.45) * mm});
            skArc(sketch, "E16.124.1", {"start": v(78.8, -60.48) * mm, "mid": v(78.8, -60.47) * mm, "end": v(78.81, -60.45) * mm});
            skArc(sketch, "E16.124.2", {"start": v(78.87, -61.79) * mm, "mid": v(78.59, -61.15) * mm, "end": v(78.8, -60.48) * mm});
            skLineSegment(sketch, "E16.124.3", {"start": v(79.07, -62) * mm, "end": v(78.87, -61.79) * mm});
            skLineSegment(sketch, "E16.124.4", {"start": v(80.35, -60.33) * mm, "end": v(80.1, -60.2) * mm});
            skArc(sketch, "E16.125.0", {"start": v(82.02, -57.54) * mm, "mid": v(81.33, -57.45) * mm, "end": v(80.75, -57.84) * mm});
            skArc(sketch, "E16.125.1", {"start": v(80.73, -57.87) * mm, "mid": v(80.74, -57.86) * mm, "end": v(80.75, -57.84) * mm});
            skArc(sketch, "E16.125.2", {"start": v(80.85, -59.17) * mm, "mid": v(80.55, -58.54) * mm, "end": v(80.73, -57.87) * mm});
            skLineSegment(sketch, "E16.125.3", {"start": v(81.06, -59.38) * mm, "end": v(80.85, -59.17) * mm});
            skLineSegment(sketch, "E16.125.4", {"start": v(82.28, -57.67) * mm, "end": v(82.02, -57.54) * mm});
            skArc(sketch, "E16.126.0", {"start": v(83.86, -54.82) * mm, "mid": v(83.16, -54.76) * mm, "end": v(82.6, -55.17) * mm});
            skArc(sketch, "E16.126.1", {"start": v(82.58, -55.2) * mm, "mid": v(82.59, -55.18) * mm, "end": v(82.6, -55.17) * mm});
            skArc(sketch, "E16.126.2", {"start": v(82.74, -56.5) * mm, "mid": v(82.42, -55.88) * mm, "end": v(82.58, -55.2) * mm});
            skLineSegment(sketch, "E16.126.3", {"start": v(82.96, -56.7) * mm, "end": v(82.74, -56.5) * mm});
            skLineSegment(sketch, "E16.126.4", {"start": v(84.12, -54.95) * mm, "end": v(83.86, -54.82) * mm});
            skArc(sketch, "E16.127.0", {"start": v(85.6, -52.05) * mm, "mid": v(84.9, -52.01) * mm, "end": v(84.36, -52.44) * mm});
            skArc(sketch, "E16.127.1", {"start": v(84.34, -52.46) * mm, "mid": v(84.35, -52.45) * mm, "end": v(84.36, -52.44) * mm});
            skArc(sketch, "E16.127.2", {"start": v(84.55, -53.76) * mm, "mid": v(84.2, -53.15) * mm, "end": v(84.34, -52.46) * mm});
            skLineSegment(sketch, "E16.127.3", {"start": v(84.77, -53.95) * mm, "end": v(84.55, -53.76) * mm});
            skLineSegment(sketch, "E16.127.4", {"start": v(85.88, -52.17) * mm, "end": v(85.6, -52.05) * mm});
            skArc(sketch, "E16.128.0", {"start": v(87.27, -49.22) * mm, "mid": v(86.57, -49.2) * mm, "end": v(86.03, -49.65) * mm});
            skArc(sketch, "E16.128.1", {"start": v(86.01, -49.68) * mm, "mid": v(86.02, -49.66) * mm, "end": v(86.03, -49.65) * mm});
            skArc(sketch, "E16.128.2", {"start": v(86.26, -50.96) * mm, "mid": v(85.9, -50.37) * mm, "end": v(86.01, -49.68) * mm});
            skLineSegment(sketch, "E16.128.3", {"start": v(86.49, -51.14) * mm, "end": v(86.26, -50.96) * mm});
            skLineSegment(sketch, "E16.128.4", {"start": v(87.54, -49.33) * mm, "end": v(87.27, -49.22) * mm});
            skArc(sketch, "E16.129.0", {"start": v(88.83, -46.34) * mm, "mid": v(88.13, -46.35) * mm, "end": v(87.6, -46.8) * mm});
            skArc(sketch, "E16.129.1", {"start": v(87.6, -46.84) * mm, "mid": v(87.6, -46.82) * mm, "end": v(87.6, -46.8) * mm});
            skArc(sketch, "E16.129.2", {"start": v(87.88, -48.11) * mm, "mid": v(87.5, -47.53) * mm, "end": v(87.6, -46.84) * mm});
            skLineSegment(sketch, "E16.129.3", {"start": v(88.12, -48.29) * mm, "end": v(87.88, -48.11) * mm});
            skLineSegment(sketch, "E16.129.4", {"start": v(89.1, -46.44) * mm, "end": v(88.83, -46.34) * mm});
            skArc(sketch, "E16.130.0", {"start": v(90.3, -43.4) * mm, "mid": v(89.6, -43.44) * mm, "end": v(89.09, -43.92) * mm});
            skArc(sketch, "E16.130.1", {"start": v(89.08, -43.94) * mm, "mid": v(89.08, -43.93) * mm, "end": v(89.09, -43.92) * mm});
            skArc(sketch, "E16.130.2", {"start": v(89.4, -45.21) * mm, "mid": v(89, -44.64) * mm, "end": v(89.08, -43.94) * mm});
            skLineSegment(sketch, "E16.130.3", {"start": v(89.65, -45.38) * mm, "end": v(89.4, -45.21) * mm});
            skLineSegment(sketch, "E16.130.4", {"start": v(90.58, -43.5) * mm, "end": v(90.3, -43.4) * mm});
            skArc(sketch, "E16.131.0", {"start": v(91.67, -40.43) * mm, "mid": v(90.97, -40.48) * mm, "end": v(90.48, -40.98) * mm});
            skArc(sketch, "E16.131.1", {"start": v(90.47, -41) * mm, "mid": v(90.47, -41) * mm, "end": v(90.48, -40.98) * mm});
            skArc(sketch, "E16.131.2", {"start": v(90.84, -42.26) * mm, "mid": v(90.42, -41.7) * mm, "end": v(90.47, -41) * mm});
            skLineSegment(sketch, "E16.131.3", {"start": v(91.09, -42.42) * mm, "end": v(90.84, -42.26) * mm});
            skLineSegment(sketch, "E16.131.4", {"start": v(91.95, -40.51) * mm, "end": v(91.67, -40.43) * mm});
            skArc(sketch, "E16.132.0", {"start": v(92.94, -37.4) * mm, "mid": v(92.25, -37.48) * mm, "end": v(91.77, -38) * mm});
            skArc(sketch, "E16.132.1", {"start": v(91.76, -38.02) * mm, "mid": v(91.77, -38.01) * mm, "end": v(91.77, -38) * mm});
            skArc(sketch, "E16.132.2", {"start": v(92.17, -39.27) * mm, "mid": v(91.73, -38.72) * mm, "end": v(91.76, -38.02) * mm});
            skLineSegment(sketch, "E16.132.3", {"start": v(92.43, -39.42) * mm, "end": v(92.17, -39.27) * mm});
            skLineSegment(sketch, "E16.132.4", {"start": v(93.23, -37.48) * mm, "end": v(92.94, -37.4) * mm});
            skArc(sketch, "E16.133.0", {"start": v(94.12, -34.35) * mm, "mid": v(93.42, -34.45) * mm, "end": v(92.97, -34.97) * mm});
            skArc(sketch, "E16.133.1", {"start": v(92.96, -35) * mm, "mid": v(92.96, -34.99) * mm, "end": v(92.97, -34.97) * mm});
            skArc(sketch, "E16.133.2", {"start": v(93.4, -36.23) * mm, "mid": v(92.95, -35.7) * mm, "end": v(92.96, -35) * mm});
            skLineSegment(sketch, "E16.133.3", {"start": v(93.67, -36.37) * mm, "end": v(93.4, -36.23) * mm});
            skLineSegment(sketch, "E16.133.4", {"start": v(94.4, -34.41) * mm, "end": v(94.12, -34.35) * mm});
            skArc(sketch, "E16.134.0", {"start": v(95.2, -31.25) * mm, "mid": v(94.5, -31.37) * mm, "end": v(94.06, -31.91) * mm});
            skArc(sketch, "E16.134.1", {"start": v(94.05, -31.94) * mm, "mid": v(94.06, -31.93) * mm, "end": v(94.06, -31.91) * mm});
            skArc(sketch, "E16.134.2", {"start": v(94.54, -33.16) * mm, "mid": v(94.07, -32.64) * mm, "end": v(94.05, -31.94) * mm});
            skLineSegment(sketch, "E16.134.3", {"start": v(94.8, -33.29) * mm, "end": v(94.54, -33.16) * mm});
            skLineSegment(sketch, "E16.134.4", {"start": v(95.48, -31.3) * mm, "end": v(95.2, -31.25) * mm});
            skArc(sketch, "E16.135.0", {"start": v(96.16, -28.12) * mm, "mid": v(95.48, -28.26) * mm, "end": v(95.05, -28.82) * mm});
            skArc(sketch, "E16.135.1", {"start": v(95.05, -28.85) * mm, "mid": v(95.05, -28.83) * mm, "end": v(95.05, -28.82) * mm});
            skArc(sketch, "E16.135.2", {"start": v(95.58, -30.04) * mm, "mid": v(95.09, -29.55) * mm, "end": v(95.05, -28.85) * mm});
            skLineSegment(sketch, "E16.135.3", {"start": v(95.84, -30.17) * mm, "end": v(95.58, -30.04) * mm});
            skLineSegment(sketch, "E16.135.4", {"start": v(96.45, -28.16) * mm, "end": v(96.16, -28.12) * mm});
            skArc(sketch, "E16.136.0", {"start": v(97.03, -24.96) * mm, "mid": v(96.35, -25.12) * mm, "end": v(95.95, -25.7) * mm});
            skArc(sketch, "E16.136.1", {"start": v(95.94, -25.72) * mm, "mid": v(95.94, -25.7) * mm, "end": v(95.95, -25.7) * mm});
            skArc(sketch, "E16.136.2", {"start": v(96.51, -26.9) * mm, "mid": v(96, -26.42) * mm, "end": v(95.94, -25.72) * mm});
            skLineSegment(sketch, "E16.136.3", {"start": v(96.78, -27.02) * mm, "end": v(96.51, -26.9) * mm});
            skLineSegment(sketch, "E16.136.4", {"start": v(97.32, -25) * mm, "end": v(97.03, -24.96) * mm});
            skArc(sketch, "E16.137.0", {"start": v(97.8, -21.77) * mm, "mid": v(97.12, -21.96) * mm, "end": v(96.74, -22.54) * mm});
            skArc(sketch, "E16.137.1", {"start": v(96.73, -22.57) * mm, "mid": v(96.73, -22.55) * mm, "end": v(96.74, -22.54) * mm});
            skArc(sketch, "E16.137.2", {"start": v(97.34, -23.73) * mm, "mid": v(96.82, -23.26) * mm, "end": v(96.73, -22.57) * mm});
            skLineSegment(sketch, "E16.137.3", {"start": v(97.61, -23.84) * mm, "end": v(97.34, -23.73) * mm});
            skLineSegment(sketch, "E16.137.4", {"start": v(98.09, -21.8) * mm, "end": v(97.8, -21.77) * mm});
            skArc(sketch, "E16.138.0", {"start": v(98.46, -18.56) * mm, "mid": v(97.79, -18.77) * mm, "end": v(97.42, -19.36) * mm});
            skArc(sketch, "E16.138.1", {"start": v(97.42, -19.4) * mm, "mid": v(97.42, -19.38) * mm, "end": v(97.42, -19.36) * mm});
            skArc(sketch, "E16.138.2", {"start": v(98.06, -20.53) * mm, "mid": v(97.53, -20.08) * mm, "end": v(97.42, -19.4) * mm});
            skLineSegment(sketch, "E16.138.3", {"start": v(98.34, -20.63) * mm, "end": v(98.06, -20.53) * mm});
            skLineSegment(sketch, "E16.138.4", {"start": v(98.75, -18.57) * mm, "end": v(98.46, -18.56) * mm});
            skArc(sketch, "E16.139.0", {"start": v(99.01, -15.33) * mm, "mid": v(98.35, -15.56) * mm, "end": v(98, -16.17) * mm});
            skArc(sketch, "E16.139.1", {"start": v(98, -16.2) * mm, "mid": v(98, -16.18) * mm, "end": v(98, -16.17) * mm});
            skArc(sketch, "E16.139.2", {"start": v(98.68, -17.31) * mm, "mid": v(98.13, -16.88) * mm, "end": v(98, -16.2) * mm});
            skLineSegment(sketch, "E16.139.3", {"start": v(98.96, -17.4) * mm, "end": v(98.68, -17.31) * mm});
            skLineSegment(sketch, "E16.139.4", {"start": v(99.3, -15.33) * mm, "end": v(99.01, -15.33) * mm});
            skArc(sketch, "E16.140.0", {"start": v(99.46, -12.08) * mm, "mid": v(98.8, -12.33) * mm, "end": v(98.48, -12.95) * mm});
            skArc(sketch, "E16.140.1", {"start": v(98.48, -12.98) * mm, "mid": v(98.48, -12.96) * mm, "end": v(98.48, -12.95) * mm});
            skArc(sketch, "E16.140.2", {"start": v(99.2, -14.07) * mm, "mid": v(98.63, -13.66) * mm, "end": v(98.48, -12.98) * mm});
            skLineSegment(sketch, "E16.140.3", {"start": v(99.48, -14.15) * mm, "end": v(99.2, -14.07) * mm});
            skLineSegment(sketch, "E16.140.4", {"start": v(99.75, -12.08) * mm, "end": v(99.46, -12.08) * mm});
            skArc(sketch, "E16.141.0", {"start": v(99.8, -8.82) * mm, "mid": v(99.16, -9.1) * mm, "end": v(98.85, -9.72) * mm});
            skArc(sketch, "E16.141.1", {"start": v(98.85, -9.75) * mm, "mid": v(98.85, -9.74) * mm, "end": v(98.85, -9.72) * mm});
            skArc(sketch, "E16.141.2", {"start": v(99.6, -10.82) * mm, "mid": v(99.03, -10.43) * mm, "end": v(98.85, -9.75) * mm});
            skLineSegment(sketch, "E16.141.3", {"start": v(99.89, -10.9) * mm, "end": v(99.6, -10.82) * mm});
            skLineSegment(sketch, "E16.141.4", {"start": v(100.1, -8.8) * mm, "end": v(99.8, -8.82) * mm});
            skArc(sketch, "E16.142.0", {"start": v(100.04, -5.55) * mm, "mid": v(99.4, -5.84) * mm, "end": v(99.12, -6.48) * mm});
            skArc(sketch, "E16.142.1", {"start": v(99.11, -6.51) * mm, "mid": v(99.11, -6.5) * mm, "end": v(99.12, -6.48) * mm});
            skArc(sketch, "E16.142.2", {"start": v(99.9, -7.56) * mm, "mid": v(99.31, -7.18) * mm, "end": v(99.11, -6.51) * mm});
            skLineSegment(sketch, "E16.142.3", {"start": v(100.2, -7.62) * mm, "end": v(99.9, -7.56) * mm});
            skLineSegment(sketch, "E16.142.4", {"start": v(100.33, -5.53) * mm, "end": v(100.04, -5.55) * mm});
            skArc(sketch, "E16.143.0", {"start": v(100.16, -2.27) * mm, "mid": v(99.54, -2.59) * mm, "end": v(99.27, -3.24) * mm});
            skArc(sketch, "E16.143.1", {"start": v(99.27, -3.26) * mm, "mid": v(99.27, -3.25) * mm, "end": v(99.27, -3.24) * mm});
            skArc(sketch, "E16.143.2", {"start": v(100.1, -4.28) * mm, "mid": v(99.5, -3.93) * mm, "end": v(99.27, -3.26) * mm});
            skLineSegment(sketch, "E16.143.3", {"start": v(100.39, -4.33) * mm, "end": v(100.1, -4.28) * mm});
            skLineSegment(sketch, "E16.143.4", {"start": v(100.46, -2.24) * mm, "end": v(100.16, -2.27) * mm});
            skArc(sketch, "E16.144.0", {"start": v(100.18, 1) * mm, "mid": v(99.57, 0.67) * mm, "end": v(99.33, 0.01) * mm});
            skArc(sketch, "E16.144.1", {"start": v(99.33, -0.01) * mm, "mid": v(99.33, 0) * mm, "end": v(99.33, 0.01) * mm});
            skArc(sketch, "E16.144.2", {"start": v(100.18, -1) * mm, "mid": v(99.57, -0.67) * mm, "end": v(99.33, -0.01) * mm});
            skLineSegment(sketch, "E16.144.3", {"start": v(100.47, -1.05) * mm, "end": v(100.18, -1) * mm});
            skLineSegment(sketch, "E16.144.4", {"start": v(100.47, 1.05) * mm, "end": v(100.18, 1) * mm});
            skArc(sketch, "E16.145.0", {"start": v(100.1, 4.28) * mm, "mid": v(99.5, 3.93) * mm, "end": v(99.27, 3.26) * mm});
            skArc(sketch, "E16.145.1", {"start": v(99.27, 3.24) * mm, "mid": v(99.27, 3.25) * mm, "end": v(99.27, 3.26) * mm});
            skArc(sketch, "E16.145.2", {"start": v(100.16, 2.27) * mm, "mid": v(99.54, 2.59) * mm, "end": v(99.27, 3.24) * mm});
            skLineSegment(sketch, "E16.145.3", {"start": v(100.46, 2.24) * mm, "end": v(100.16, 2.27) * mm});
            skLineSegment(sketch, "E16.145.4", {"start": v(100.39, 4.33) * mm, "end": v(100.1, 4.28) * mm});
            skArc(sketch, "E16.146.0", {"start": v(99.9, 7.56) * mm, "mid": v(99.31, 7.18) * mm, "end": v(99.11, 6.51) * mm});
            skArc(sketch, "E16.146.1", {"start": v(99.12, 6.48) * mm, "mid": v(99.11, 6.5) * mm, "end": v(99.11, 6.51) * mm});
            skArc(sketch, "E16.146.2", {"start": v(100.04, 5.55) * mm, "mid": v(99.4, 5.84) * mm, "end": v(99.12, 6.48) * mm});
            skLineSegment(sketch, "E16.146.3", {"start": v(100.33, 5.53) * mm, "end": v(100.04, 5.55) * mm});
            skLineSegment(sketch, "E16.146.4", {"start": v(100.2, 7.62) * mm, "end": v(99.9, 7.56) * mm});
            skArc(sketch, "E16.147.0", {"start": v(99.6, 10.82) * mm, "mid": v(99.03, 10.43) * mm, "end": v(98.85, 9.75) * mm});
            skArc(sketch, "E16.147.1", {"start": v(98.85, 9.72) * mm, "mid": v(98.85, 9.74) * mm, "end": v(98.85, 9.75) * mm});
            skArc(sketch, "E16.147.2", {"start": v(99.8, 8.82) * mm, "mid": v(99.16, 9.1) * mm, "end": v(98.85, 9.72) * mm});
            skLineSegment(sketch, "E16.147.3", {"start": v(100.1, 8.8) * mm, "end": v(99.8, 8.82) * mm});
            skLineSegment(sketch, "E16.147.4", {"start": v(99.89, 10.9) * mm, "end": v(99.6, 10.82) * mm});
            skArc(sketch, "E16.148.0", {"start": v(99.2, 14.07) * mm, "mid": v(98.63, 13.66) * mm, "end": v(98.48, 12.98) * mm});
            skArc(sketch, "E16.148.1", {"start": v(98.48, 12.95) * mm, "mid": v(98.48, 12.96) * mm, "end": v(98.48, 12.98) * mm});
            skArc(sketch, "E16.148.2", {"start": v(99.46, 12.08) * mm, "mid": v(98.8, 12.33) * mm, "end": v(98.48, 12.95) * mm});
            skLineSegment(sketch, "E16.148.3", {"start": v(99.75, 12.08) * mm, "end": v(99.46, 12.08) * mm});
            skLineSegment(sketch, "E16.148.4", {"start": v(99.48, 14.15) * mm, "end": v(99.2, 14.07) * mm});
            skArc(sketch, "E16.149.0", {"start": v(98.68, 17.31) * mm, "mid": v(98.13, 16.88) * mm, "end": v(98, 16.2) * mm});
            skArc(sketch, "E16.149.1", {"start": v(98, 16.17) * mm, "mid": v(98, 16.18) * mm, "end": v(98, 16.2) * mm});
            skArc(sketch, "E16.149.2", {"start": v(99.01, 15.33) * mm, "mid": v(98.35, 15.56) * mm, "end": v(98, 16.17) * mm});
            skLineSegment(sketch, "E16.149.3", {"start": v(99.3, 15.33) * mm, "end": v(99.01, 15.33) * mm});
            skLineSegment(sketch, "E16.149.4", {"start": v(98.96, 17.4) * mm, "end": v(98.68, 17.31) * mm});
            skArc(sketch, "E16.150.0", {"start": v(98.06, 20.53) * mm, "mid": v(97.53, 20.08) * mm, "end": v(97.42, 19.4) * mm});
            skArc(sketch, "E16.150.1", {"start": v(97.42, 19.36) * mm, "mid": v(97.42, 19.38) * mm, "end": v(97.42, 19.4) * mm});
            skArc(sketch, "E16.150.2", {"start": v(98.46, 18.56) * mm, "mid": v(97.79, 18.77) * mm, "end": v(97.42, 19.36) * mm});
            skLineSegment(sketch, "E16.150.3", {"start": v(98.75, 18.57) * mm, "end": v(98.46, 18.56) * mm});
            skLineSegment(sketch, "E16.150.4", {"start": v(98.34, 20.63) * mm, "end": v(98.06, 20.53) * mm});
            skArc(sketch, "E16.151.0", {"start": v(97.34, 23.73) * mm, "mid": v(96.82, 23.26) * mm, "end": v(96.73, 22.57) * mm});
            skArc(sketch, "E16.151.1", {"start": v(96.74, 22.54) * mm, "mid": v(96.73, 22.55) * mm, "end": v(96.73, 22.57) * mm});
            skArc(sketch, "E16.151.2", {"start": v(97.8, 21.77) * mm, "mid": v(97.12, 21.96) * mm, "end": v(96.74, 22.54) * mm});
            skLineSegment(sketch, "E16.151.3", {"start": v(98.09, 21.8) * mm, "end": v(97.8, 21.77) * mm});
            skLineSegment(sketch, "E16.151.4", {"start": v(97.61, 23.84) * mm, "end": v(97.34, 23.73) * mm});
            skArc(sketch, "E16.152.0", {"start": v(96.51, 26.9) * mm, "mid": v(96, 26.42) * mm, "end": v(95.94, 25.72) * mm});
            skArc(sketch, "E16.152.1", {"start": v(95.95, 25.7) * mm, "mid": v(95.94, 25.7) * mm, "end": v(95.94, 25.72) * mm});
            skArc(sketch, "E16.152.2", {"start": v(97.03, 24.96) * mm, "mid": v(96.35, 25.12) * mm, "end": v(95.95, 25.7) * mm});
            skLineSegment(sketch, "E16.152.3", {"start": v(97.32, 25) * mm, "end": v(97.03, 24.96) * mm});
            skLineSegment(sketch, "E16.152.4", {"start": v(96.78, 27.02) * mm, "end": v(96.51, 26.9) * mm});
            skArc(sketch, "E16.153.0", {"start": v(95.58, 30.04) * mm, "mid": v(95.09, 29.55) * mm, "end": v(95.05, 28.85) * mm});
            skArc(sketch, "E16.153.1", {"start": v(95.05, 28.82) * mm, "mid": v(95.05, 28.83) * mm, "end": v(95.05, 28.85) * mm});
            skArc(sketch, "E16.153.2", {"start": v(96.16, 28.12) * mm, "mid": v(95.48, 28.26) * mm, "end": v(95.05, 28.82) * mm});
            skLineSegment(sketch, "E16.153.3", {"start": v(96.45, 28.16) * mm, "end": v(96.16, 28.12) * mm});
            skLineSegment(sketch, "E16.153.4", {"start": v(95.84, 30.17) * mm, "end": v(95.58, 30.04) * mm});
            skArc(sketch, "E16.154.0", {"start": v(94.54, 33.16) * mm, "mid": v(94.07, 32.64) * mm, "end": v(94.05, 31.94) * mm});
            skArc(sketch, "E16.154.1", {"start": v(94.06, 31.91) * mm, "mid": v(94.06, 31.93) * mm, "end": v(94.05, 31.94) * mm});
            skArc(sketch, "E16.154.2", {"start": v(95.2, 31.25) * mm, "mid": v(94.5, 31.37) * mm, "end": v(94.06, 31.91) * mm});
            skLineSegment(sketch, "E16.154.3", {"start": v(95.48, 31.3) * mm, "end": v(95.2, 31.25) * mm});
            skLineSegment(sketch, "E16.154.4", {"start": v(94.8, 33.29) * mm, "end": v(94.54, 33.16) * mm});
            skArc(sketch, "E16.155.0", {"start": v(93.4, 36.23) * mm, "mid": v(92.95, 35.7) * mm, "end": v(92.96, 35) * mm});
            skArc(sketch, "E16.155.1", {"start": v(92.97, 34.97) * mm, "mid": v(92.96, 34.99) * mm, "end": v(92.96, 35) * mm});
            skArc(sketch, "E16.155.2", {"start": v(94.12, 34.35) * mm, "mid": v(93.42, 34.45) * mm, "end": v(92.97, 34.97) * mm});
            skLineSegment(sketch, "E16.155.3", {"start": v(94.4, 34.41) * mm, "end": v(94.12, 34.35) * mm});
            skLineSegment(sketch, "E16.155.4", {"start": v(93.67, 36.37) * mm, "end": v(93.4, 36.23) * mm});
            skArc(sketch, "E16.156.0", {"start": v(92.17, 39.27) * mm, "mid": v(91.73, 38.72) * mm, "end": v(91.76, 38.02) * mm});
            skArc(sketch, "E16.156.1", {"start": v(91.77, 38) * mm, "mid": v(91.77, 38.01) * mm, "end": v(91.76, 38.02) * mm});
            skArc(sketch, "E16.156.2", {"start": v(92.94, 37.4) * mm, "mid": v(92.25, 37.48) * mm, "end": v(91.77, 38) * mm});
            skLineSegment(sketch, "E16.156.3", {"start": v(93.23, 37.48) * mm, "end": v(92.94, 37.4) * mm});
            skLineSegment(sketch, "E16.156.4", {"start": v(92.43, 39.42) * mm, "end": v(92.17, 39.27) * mm});
            skArc(sketch, "E16.157.0", {"start": v(90.84, 42.26) * mm, "mid": v(90.42, 41.7) * mm, "end": v(90.47, 41) * mm});
            skArc(sketch, "E16.157.1", {"start": v(90.48, 40.98) * mm, "mid": v(90.47, 41) * mm, "end": v(90.47, 41) * mm});
            skArc(sketch, "E16.157.2", {"start": v(91.67, 40.43) * mm, "mid": v(90.97, 40.48) * mm, "end": v(90.48, 40.98) * mm});
            skLineSegment(sketch, "E16.157.3", {"start": v(91.95, 40.51) * mm, "end": v(91.67, 40.43) * mm});
            skLineSegment(sketch, "E16.157.4", {"start": v(91.09, 42.42) * mm, "end": v(90.84, 42.26) * mm});
            skArc(sketch, "E16.158.0", {"start": v(89.4, 45.21) * mm, "mid": v(89, 44.64) * mm, "end": v(89.08, 43.94) * mm});
            skArc(sketch, "E16.158.1", {"start": v(89.09, 43.92) * mm, "mid": v(89.08, 43.93) * mm, "end": v(89.08, 43.94) * mm});
            skArc(sketch, "E16.158.2", {"start": v(90.3, 43.4) * mm, "mid": v(89.6, 43.44) * mm, "end": v(89.09, 43.92) * mm});
            skLineSegment(sketch, "E16.158.3", {"start": v(90.58, 43.5) * mm, "end": v(90.3, 43.4) * mm});
            skLineSegment(sketch, "E16.158.4", {"start": v(89.65, 45.38) * mm, "end": v(89.4, 45.21) * mm});
            skArc(sketch, "E16.159.0", {"start": v(87.88, 48.11) * mm, "mid": v(87.5, 47.53) * mm, "end": v(87.6, 46.84) * mm});
            skArc(sketch, "E16.159.1", {"start": v(87.6, 46.8) * mm, "mid": v(87.6, 46.82) * mm, "end": v(87.6, 46.84) * mm});
            skArc(sketch, "E16.159.2", {"start": v(88.83, 46.34) * mm, "mid": v(88.13, 46.35) * mm, "end": v(87.6, 46.8) * mm});
            skLineSegment(sketch, "E16.159.3", {"start": v(89.1, 46.44) * mm, "end": v(88.83, 46.34) * mm});
            skLineSegment(sketch, "E16.159.4", {"start": v(88.12, 48.29) * mm, "end": v(87.88, 48.11) * mm});
            skArc(sketch, "E16.160.0", {"start": v(86.26, 50.96) * mm, "mid": v(85.9, 50.37) * mm, "end": v(86.01, 49.68) * mm});
            skArc(sketch, "E16.160.1", {"start": v(86.03, 49.65) * mm, "mid": v(86.02, 49.66) * mm, "end": v(86.01, 49.68) * mm});
            skArc(sketch, "E16.160.2", {"start": v(87.27, 49.22) * mm, "mid": v(86.57, 49.2) * mm, "end": v(86.03, 49.65) * mm});
            skLineSegment(sketch, "E16.160.3", {"start": v(87.54, 49.33) * mm, "end": v(87.27, 49.22) * mm});
            skLineSegment(sketch, "E16.160.4", {"start": v(86.49, 51.14) * mm, "end": v(86.26, 50.96) * mm});
            skArc(sketch, "E16.161.0", {"start": v(84.55, 53.76) * mm, "mid": v(84.2, 53.15) * mm, "end": v(84.34, 52.46) * mm});
            skArc(sketch, "E16.161.1", {"start": v(84.36, 52.44) * mm, "mid": v(84.35, 52.45) * mm, "end": v(84.34, 52.46) * mm});
            skArc(sketch, "E16.161.2", {"start": v(85.6, 52.05) * mm, "mid": v(84.9, 52.01) * mm, "end": v(84.36, 52.44) * mm});
            skLineSegment(sketch, "E16.161.3", {"start": v(85.88, 52.17) * mm, "end": v(85.6, 52.05) * mm});
            skLineSegment(sketch, "E16.161.4", {"start": v(84.77, 53.95) * mm, "end": v(84.55, 53.76) * mm});
            skArc(sketch, "E16.162.0", {"start": v(82.74, 56.5) * mm, "mid": v(82.42, 55.88) * mm, "end": v(82.58, 55.2) * mm});
            skArc(sketch, "E16.162.1", {"start": v(82.6, 55.17) * mm, "mid": v(82.59, 55.18) * mm, "end": v(82.58, 55.2) * mm});
            skArc(sketch, "E16.162.2", {"start": v(83.86, 54.82) * mm, "mid": v(83.16, 54.76) * mm, "end": v(82.6, 55.17) * mm});
            skLineSegment(sketch, "E16.162.3", {"start": v(84.12, 54.95) * mm, "end": v(83.86, 54.82) * mm});
            skLineSegment(sketch, "E16.162.4", {"start": v(82.96, 56.7) * mm, "end": v(82.74, 56.5) * mm});
            skArc(sketch, "E16.163.0", {"start": v(80.85, 59.17) * mm, "mid": v(80.55, 58.54) * mm, "end": v(80.73, 57.87) * mm});
            skArc(sketch, "E16.163.1", {"start": v(80.75, 57.84) * mm, "mid": v(80.74, 57.86) * mm, "end": v(80.73, 57.87) * mm});
            skArc(sketch, "E16.163.2", {"start": v(82.02, 57.54) * mm, "mid": v(81.33, 57.45) * mm, "end": v(80.75, 57.84) * mm});
            skLineSegment(sketch, "E16.163.3", {"start": v(82.28, 57.67) * mm, "end": v(82.02, 57.54) * mm});
            skLineSegment(sketch, "E16.163.4", {"start": v(81.06, 59.38) * mm, "end": v(80.85, 59.17) * mm});
            skArc(sketch, "E16.164.0", {"start": v(78.87, 61.79) * mm, "mid": v(78.59, 61.15) * mm, "end": v(78.8, 60.48) * mm});
            skArc(sketch, "E16.164.1", {"start": v(78.81, 60.45) * mm, "mid": v(78.8, 60.47) * mm, "end": v(78.8, 60.48) * mm});
            skArc(sketch, "E16.164.2", {"start": v(80.1, 60.2) * mm, "mid": v(79.4, 60.08) * mm, "end": v(78.81, 60.45) * mm});
            skLineSegment(sketch, "E16.164.3", {"start": v(80.35, 60.33) * mm, "end": v(80.1, 60.2) * mm});
            skLineSegment(sketch, "E16.164.4", {"start": v(79.07, 62) * mm, "end": v(78.87, 61.79) * mm});
            skArc(sketch, "E16.165.0", {"start": v(76.8, 64.33) * mm, "mid": v(76.54, 63.69) * mm, "end": v(76.77, 63.02) * mm});
            skArc(sketch, "E16.165.1", {"start": v(76.79, 63) * mm, "mid": v(76.78, 63.01) * mm, "end": v(76.77, 63.02) * mm});
            skArc(sketch, "E16.165.2", {"start": v(78.08, 62.78) * mm, "mid": v(77.4, 62.65) * mm, "end": v(76.79, 63) * mm});
            skLineSegment(sketch, "E16.165.3", {"start": v(78.33, 62.93) * mm, "end": v(78.08, 62.78) * mm});
            skLineSegment(sketch, "E16.165.4", {"start": v(77, 64.55) * mm, "end": v(76.8, 64.33) * mm});
            skArc(sketch, "E16.166.0", {"start": v(74.66, 66.81) * mm, "mid": v(74.42, 66.16) * mm, "end": v(74.67, 65.5) * mm});
            skArc(sketch, "E16.166.1", {"start": v(74.69, 65.48) * mm, "mid": v(74.68, 65.5) * mm, "end": v(74.67, 65.5) * mm});
            skArc(sketch, "E16.166.2", {"start": v(75.99, 65.3) * mm, "mid": v(75.3, 65.15) * mm, "end": v(74.69, 65.48) * mm});
            skLineSegment(sketch, "E16.166.3", {"start": v(76.23, 65.46) * mm, "end": v(75.99, 65.3) * mm});
            skLineSegment(sketch, "E16.166.4", {"start": v(74.85, 67.04) * mm, "end": v(74.66, 66.81) * mm});
            skArc(sketch, "E16.167.0", {"start": v(72.43, 69.22) * mm, "mid": v(72.21, 68.55) * mm, "end": v(72.49, 67.9) * mm});
            skArc(sketch, "E16.167.1", {"start": v(72.5, 67.89) * mm, "mid": v(72.5, 67.9) * mm, "end": v(72.49, 67.9) * mm});
            skArc(sketch, "E16.167.2", {"start": v(73.8, 67.75) * mm, "mid": v(73.13, 67.58) * mm, "end": v(72.5, 67.89) * mm});
            skLineSegment(sketch, "E16.167.3", {"start": v(74.05, 67.92) * mm, "end": v(73.8, 67.75) * mm});
            skLineSegment(sketch, "E16.167.4", {"start": v(72.62, 69.45) * mm, "end": v(72.43, 69.22) * mm});
            skArc(sketch, "E16.168.0", {"start": v(70.13, 71.55) * mm, "mid": v(69.93, 70.88) * mm, "end": v(70.22, 70.24) * mm});
            skArc(sketch, "E16.168.1", {"start": v(70.24, 70.22) * mm, "mid": v(70.23, 70.23) * mm, "end": v(70.22, 70.24) * mm});
            skArc(sketch, "E16.168.2", {"start": v(71.55, 70.13) * mm, "mid": v(70.88, 69.93) * mm, "end": v(70.24, 70.22) * mm});
            skLineSegment(sketch, "E16.168.3", {"start": v(71.79, 70.3) * mm, "end": v(71.55, 70.13) * mm});
            skLineSegment(sketch, "E16.168.4", {"start": v(70.3, 71.79) * mm, "end": v(70.13, 71.55) * mm});
            skArc(sketch, "E16.169.0", {"start": v(67.75, 73.8) * mm, "mid": v(67.58, 73.13) * mm, "end": v(67.89, 72.5) * mm});
            skArc(sketch, "E16.169.1", {"start": v(67.9, 72.49) * mm, "mid": v(67.9, 72.5) * mm, "end": v(67.89, 72.5) * mm});
            skArc(sketch, "E16.169.2", {"start": v(69.22, 72.43) * mm, "mid": v(68.55, 72.21) * mm, "end": v(67.9, 72.49) * mm});
            skLineSegment(sketch, "E16.169.3", {"start": v(69.45, 72.62) * mm, "end": v(69.22, 72.43) * mm});
            skLineSegment(sketch, "E16.169.4", {"start": v(67.92, 74.05) * mm, "end": v(67.75, 73.8) * mm});
            skArc(sketch, "E16.170.0", {"start": v(65.3, 75.99) * mm, "mid": v(65.15, 75.3) * mm, "end": v(65.48, 74.69) * mm});
            skArc(sketch, "E16.170.1", {"start": v(65.5, 74.67) * mm, "mid": v(65.5, 74.68) * mm, "end": v(65.48, 74.69) * mm});
            skArc(sketch, "E16.170.2", {"start": v(66.81, 74.66) * mm, "mid": v(66.16, 74.42) * mm, "end": v(65.5, 74.67) * mm});
            skLineSegment(sketch, "E16.170.3", {"start": v(67.04, 74.85) * mm, "end": v(66.81, 74.66) * mm});
            skLineSegment(sketch, "E16.170.4", {"start": v(65.46, 76.23) * mm, "end": v(65.3, 75.99) * mm});
            skArc(sketch, "E16.171.0", {"start": v(62.78, 78.08) * mm, "mid": v(62.65, 77.4) * mm, "end": v(63, 76.79) * mm});
            skArc(sketch, "E16.171.1", {"start": v(63.02, 76.77) * mm, "mid": v(63.01, 76.78) * mm, "end": v(63, 76.79) * mm});
            skArc(sketch, "E16.171.2", {"start": v(64.33, 76.8) * mm, "mid": v(63.69, 76.54) * mm, "end": v(63.02, 76.77) * mm});
            skLineSegment(sketch, "E16.171.3", {"start": v(64.55, 77) * mm, "end": v(64.33, 76.8) * mm});
            skLineSegment(sketch, "E16.171.4", {"start": v(62.93, 78.33) * mm, "end": v(62.78, 78.08) * mm});
            skArc(sketch, "E16.172.0", {"start": v(60.2, 80.1) * mm, "mid": v(60.08, 79.4) * mm, "end": v(60.45, 78.81) * mm});
            skArc(sketch, "E16.172.1", {"start": v(60.48, 78.8) * mm, "mid": v(60.47, 78.8) * mm, "end": v(60.45, 78.81) * mm});
            skArc(sketch, "E16.172.2", {"start": v(61.79, 78.87) * mm, "mid": v(61.15, 78.59) * mm, "end": v(60.48, 78.8) * mm});
            skLineSegment(sketch, "E16.172.3", {"start": v(62, 79.07) * mm, "end": v(61.79, 78.87) * mm});
            skLineSegment(sketch, "E16.172.4", {"start": v(60.33, 80.35) * mm, "end": v(60.2, 80.1) * mm});
            skArc(sketch, "E16.173.0", {"start": v(57.54, 82.02) * mm, "mid": v(57.45, 81.33) * mm, "end": v(57.84, 80.75) * mm});
            skArc(sketch, "E16.173.1", {"start": v(57.87, 80.73) * mm, "mid": v(57.86, 80.74) * mm, "end": v(57.84, 80.75) * mm});
            skArc(sketch, "E16.173.2", {"start": v(59.17, 80.85) * mm, "mid": v(58.54, 80.55) * mm, "end": v(57.87, 80.73) * mm});
            skLineSegment(sketch, "E16.173.3", {"start": v(59.38, 81.06) * mm, "end": v(59.17, 80.85) * mm});
            skLineSegment(sketch, "E16.173.4", {"start": v(57.67, 82.28) * mm, "end": v(57.54, 82.02) * mm});
            skArc(sketch, "E16.174.0", {"start": v(54.82, 83.86) * mm, "mid": v(54.76, 83.16) * mm, "end": v(55.17, 82.6) * mm});
            skArc(sketch, "E16.174.1", {"start": v(55.2, 82.58) * mm, "mid": v(55.18, 82.59) * mm, "end": v(55.17, 82.6) * mm});
            skArc(sketch, "E16.174.2", {"start": v(56.5, 82.74) * mm, "mid": v(55.88, 82.42) * mm, "end": v(55.2, 82.58) * mm});
            skLineSegment(sketch, "E16.174.3", {"start": v(56.7, 82.96) * mm, "end": v(56.5, 82.74) * mm});
            skLineSegment(sketch, "E16.174.4", {"start": v(54.95, 84.12) * mm, "end": v(54.82, 83.86) * mm});
            skArc(sketch, "E16.175.0", {"start": v(52.05, 85.6) * mm, "mid": v(52.01, 84.9) * mm, "end": v(52.44, 84.36) * mm});
            skArc(sketch, "E16.175.1", {"start": v(52.46, 84.34) * mm, "mid": v(52.45, 84.35) * mm, "end": v(52.44, 84.36) * mm});
            skArc(sketch, "E16.175.2", {"start": v(53.76, 84.55) * mm, "mid": v(53.15, 84.2) * mm, "end": v(52.46, 84.34) * mm});
            skLineSegment(sketch, "E16.175.3", {"start": v(53.95, 84.77) * mm, "end": v(53.76, 84.55) * mm});
            skLineSegment(sketch, "E16.175.4", {"start": v(52.17, 85.88) * mm, "end": v(52.05, 85.6) * mm});
            skArc(sketch, "E16.176.0", {"start": v(49.22, 87.27) * mm, "mid": v(49.2, 86.57) * mm, "end": v(49.65, 86.03) * mm});
            skArc(sketch, "E16.176.1", {"start": v(49.68, 86.01) * mm, "mid": v(49.66, 86.02) * mm, "end": v(49.65, 86.03) * mm});
            skArc(sketch, "E16.176.2", {"start": v(50.96, 86.26) * mm, "mid": v(50.37, 85.9) * mm, "end": v(49.68, 86.01) * mm});
            skLineSegment(sketch, "E16.176.3", {"start": v(51.14, 86.49) * mm, "end": v(50.96, 86.26) * mm});
            skLineSegment(sketch, "E16.176.4", {"start": v(49.33, 87.54) * mm, "end": v(49.22, 87.27) * mm});
            skArc(sketch, "E16.177.0", {"start": v(46.34, 88.83) * mm, "mid": v(46.35, 88.13) * mm, "end": v(46.8, 87.6) * mm});
            skArc(sketch, "E16.177.1", {"start": v(46.84, 87.6) * mm, "mid": v(46.82, 87.6) * mm, "end": v(46.8, 87.6) * mm});
            skArc(sketch, "E16.177.2", {"start": v(48.11, 87.88) * mm, "mid": v(47.53, 87.5) * mm, "end": v(46.84, 87.6) * mm});
            skLineSegment(sketch, "E16.177.3", {"start": v(48.29, 88.12) * mm, "end": v(48.11, 87.88) * mm});
            skLineSegment(sketch, "E16.177.4", {"start": v(46.44, 89.1) * mm, "end": v(46.34, 88.83) * mm});
            skArc(sketch, "E16.178.0", {"start": v(43.4, 90.3) * mm, "mid": v(43.44, 89.6) * mm, "end": v(43.92, 89.09) * mm});
            skArc(sketch, "E16.178.1", {"start": v(43.94, 89.08) * mm, "mid": v(43.93, 89.08) * mm, "end": v(43.92, 89.09) * mm});
            skArc(sketch, "E16.178.2", {"start": v(45.21, 89.4) * mm, "mid": v(44.64, 89) * mm, "end": v(43.94, 89.08) * mm});
            skLineSegment(sketch, "E16.178.3", {"start": v(45.38, 89.65) * mm, "end": v(45.21, 89.4) * mm});
            skLineSegment(sketch, "E16.178.4", {"start": v(43.5, 90.58) * mm, "end": v(43.4, 90.3) * mm});
            skArc(sketch, "E16.179.0", {"start": v(40.43, 91.67) * mm, "mid": v(40.48, 90.97) * mm, "end": v(40.98, 90.48) * mm});
            skArc(sketch, "E16.179.1", {"start": v(41, 90.47) * mm, "mid": v(41, 90.47) * mm, "end": v(40.98, 90.48) * mm});
            skArc(sketch, "E16.179.2", {"start": v(42.26, 90.84) * mm, "mid": v(41.7, 90.42) * mm, "end": v(41, 90.47) * mm});
            skLineSegment(sketch, "E16.179.3", {"start": v(42.42, 91.09) * mm, "end": v(42.26, 90.84) * mm});
            skLineSegment(sketch, "E16.179.4", {"start": v(40.51, 91.95) * mm, "end": v(40.43, 91.67) * mm});
            skArc(sketch, "E16.180.0", {"start": v(37.4, 92.94) * mm, "mid": v(37.48, 92.25) * mm, "end": v(38, 91.77) * mm});
            skArc(sketch, "E16.180.1", {"start": v(38.02, 91.76) * mm, "mid": v(38.01, 91.77) * mm, "end": v(38, 91.77) * mm});
            skArc(sketch, "E16.180.2", {"start": v(39.27, 92.17) * mm, "mid": v(38.72, 91.73) * mm, "end": v(38.02, 91.76) * mm});
            skLineSegment(sketch, "E16.180.3", {"start": v(39.42, 92.43) * mm, "end": v(39.27, 92.17) * mm});
            skLineSegment(sketch, "E16.180.4", {"start": v(37.48, 93.23) * mm, "end": v(37.4, 92.94) * mm});
            skArc(sketch, "E16.181.0", {"start": v(34.35, 94.12) * mm, "mid": v(34.45, 93.42) * mm, "end": v(34.97, 92.97) * mm});
            skArc(sketch, "E16.181.1", {"start": v(35, 92.96) * mm, "mid": v(34.99, 92.96) * mm, "end": v(34.97, 92.97) * mm});
            skArc(sketch, "E16.181.2", {"start": v(36.23, 93.4) * mm, "mid": v(35.7, 92.95) * mm, "end": v(35, 92.96) * mm});
            skLineSegment(sketch, "E16.181.3", {"start": v(36.37, 93.67) * mm, "end": v(36.23, 93.4) * mm});
            skLineSegment(sketch, "E16.181.4", {"start": v(34.41, 94.4) * mm, "end": v(34.35, 94.12) * mm});
            skArc(sketch, "E16.182.0", {"start": v(31.25, 95.2) * mm, "mid": v(31.37, 94.5) * mm, "end": v(31.91, 94.06) * mm});
            skArc(sketch, "E16.182.1", {"start": v(31.94, 94.05) * mm, "mid": v(31.93, 94.06) * mm, "end": v(31.91, 94.06) * mm});
            skArc(sketch, "E16.182.2", {"start": v(33.16, 94.54) * mm, "mid": v(32.64, 94.07) * mm, "end": v(31.94, 94.05) * mm});
            skLineSegment(sketch, "E16.182.3", {"start": v(33.29, 94.8) * mm, "end": v(33.16, 94.54) * mm});
            skLineSegment(sketch, "E16.182.4", {"start": v(31.3, 95.48) * mm, "end": v(31.25, 95.2) * mm});
            skArc(sketch, "E16.183.0", {"start": v(28.12, 96.16) * mm, "mid": v(28.26, 95.48) * mm, "end": v(28.82, 95.05) * mm});
            skArc(sketch, "E16.183.1", {"start": v(28.85, 95.05) * mm, "mid": v(28.83, 95.05) * mm, "end": v(28.82, 95.05) * mm});
            skArc(sketch, "E16.183.2", {"start": v(30.04, 95.58) * mm, "mid": v(29.55, 95.09) * mm, "end": v(28.85, 95.05) * mm});
            skLineSegment(sketch, "E16.183.3", {"start": v(30.17, 95.84) * mm, "end": v(30.04, 95.58) * mm});
            skLineSegment(sketch, "E16.183.4", {"start": v(28.16, 96.45) * mm, "end": v(28.12, 96.16) * mm});
            skArc(sketch, "E16.184.0", {"start": v(24.96, 97.03) * mm, "mid": v(25.12, 96.35) * mm, "end": v(25.7, 95.95) * mm});
            skArc(sketch, "E16.184.1", {"start": v(25.72, 95.94) * mm, "mid": v(25.7, 95.94) * mm, "end": v(25.7, 95.95) * mm});
            skArc(sketch, "E16.184.2", {"start": v(26.9, 96.51) * mm, "mid": v(26.42, 96) * mm, "end": v(25.72, 95.94) * mm});
            skLineSegment(sketch, "E16.184.3", {"start": v(27.02, 96.78) * mm, "end": v(26.9, 96.51) * mm});
            skLineSegment(sketch, "E16.184.4", {"start": v(25, 97.32) * mm, "end": v(24.96, 97.03) * mm});
            skArc(sketch, "E16.185.0", {"start": v(21.77, 97.8) * mm, "mid": v(21.96, 97.12) * mm, "end": v(22.54, 96.74) * mm});
            skArc(sketch, "E16.185.1", {"start": v(22.57, 96.73) * mm, "mid": v(22.55, 96.73) * mm, "end": v(22.54, 96.74) * mm});
            skArc(sketch, "E16.185.2", {"start": v(23.73, 97.34) * mm, "mid": v(23.26, 96.82) * mm, "end": v(22.57, 96.73) * mm});
            skLineSegment(sketch, "E16.185.3", {"start": v(23.84, 97.61) * mm, "end": v(23.73, 97.34) * mm});
            skLineSegment(sketch, "E16.185.4", {"start": v(21.8, 98.09) * mm, "end": v(21.77, 97.8) * mm});
            skArc(sketch, "E16.186.0", {"start": v(18.56, 98.46) * mm, "mid": v(18.77, 97.79) * mm, "end": v(19.36, 97.42) * mm});
            skArc(sketch, "E16.186.1", {"start": v(19.4, 97.42) * mm, "mid": v(19.38, 97.42) * mm, "end": v(19.36, 97.42) * mm});
            skArc(sketch, "E16.186.2", {"start": v(20.53, 98.06) * mm, "mid": v(20.08, 97.53) * mm, "end": v(19.4, 97.42) * mm});
            skLineSegment(sketch, "E16.186.3", {"start": v(20.63, 98.34) * mm, "end": v(20.53, 98.06) * mm});
            skLineSegment(sketch, "E16.186.4", {"start": v(18.57, 98.75) * mm, "end": v(18.56, 98.46) * mm});
            skArc(sketch, "E16.187.0", {"start": v(15.33, 99.01) * mm, "mid": v(15.56, 98.35) * mm, "end": v(16.17, 98) * mm});
            skArc(sketch, "E16.187.1", {"start": v(16.2, 98) * mm, "mid": v(16.18, 98) * mm, "end": v(16.17, 98) * mm});
            skArc(sketch, "E16.187.2", {"start": v(17.31, 98.68) * mm, "mid": v(16.88, 98.13) * mm, "end": v(16.2, 98) * mm});
            skLineSegment(sketch, "E16.187.3", {"start": v(17.4, 98.96) * mm, "end": v(17.31, 98.68) * mm});
            skLineSegment(sketch, "E16.187.4", {"start": v(15.33, 99.3) * mm, "end": v(15.33, 99.01) * mm});
            skArc(sketch, "E16.188.0", {"start": v(12.08, 99.46) * mm, "mid": v(12.33, 98.8) * mm, "end": v(12.95, 98.48) * mm});
            skArc(sketch, "E16.188.1", {"start": v(12.98, 98.48) * mm, "mid": v(12.96, 98.48) * mm, "end": v(12.95, 98.48) * mm});
            skArc(sketch, "E16.188.2", {"start": v(14.07, 99.2) * mm, "mid": v(13.66, 98.63) * mm, "end": v(12.98, 98.48) * mm});
            skLineSegment(sketch, "E16.188.3", {"start": v(14.15, 99.48) * mm, "end": v(14.07, 99.2) * mm});
            skLineSegment(sketch, "E16.188.4", {"start": v(12.08, 99.75) * mm, "end": v(12.08, 99.46) * mm});
            skArc(sketch, "E16.189.0", {"start": v(8.82, 99.8) * mm, "mid": v(9.1, 99.16) * mm, "end": v(9.72, 98.85) * mm});
            skArc(sketch, "E16.189.1", {"start": v(9.75, 98.85) * mm, "mid": v(9.74, 98.85) * mm, "end": v(9.72, 98.85) * mm});
            skArc(sketch, "E16.189.2", {"start": v(10.82, 99.6) * mm, "mid": v(10.43, 99.03) * mm, "end": v(9.75, 98.85) * mm});
            skLineSegment(sketch, "E16.189.3", {"start": v(10.9, 99.89) * mm, "end": v(10.82, 99.6) * mm});
            skLineSegment(sketch, "E16.189.4", {"start": v(8.8, 100.1) * mm, "end": v(8.82, 99.8) * mm});
            skArc(sketch, "E16.190.0", {"start": v(5.55, 100.04) * mm, "mid": v(5.84, 99.4) * mm, "end": v(6.48, 99.12) * mm});
            skArc(sketch, "E16.190.1", {"start": v(6.51, 99.11) * mm, "mid": v(6.5, 99.11) * mm, "end": v(6.48, 99.12) * mm});
            skArc(sketch, "E16.190.2", {"start": v(7.56, 99.9) * mm, "mid": v(7.18, 99.31) * mm, "end": v(6.51, 99.11) * mm});
            skLineSegment(sketch, "E16.190.3", {"start": v(7.62, 100.2) * mm, "end": v(7.56, 99.9) * mm});
            skLineSegment(sketch, "E16.190.4", {"start": v(5.53, 100.33) * mm, "end": v(5.55, 100.04) * mm});
            skArc(sketch, "E16.191.0", {"start": v(2.27, 100.16) * mm, "mid": v(2.59, 99.54) * mm, "end": v(3.24, 99.27) * mm});
            skArc(sketch, "E16.191.1", {"start": v(3.26, 99.27) * mm, "mid": v(3.25, 99.27) * mm, "end": v(3.24, 99.27) * mm});
            skArc(sketch, "E16.191.2", {"start": v(4.28, 100.1) * mm, "mid": v(3.93, 99.5) * mm, "end": v(3.26, 99.27) * mm});
            skLineSegment(sketch, "E16.191.3", {"start": v(4.33, 100.39) * mm, "end": v(4.28, 100.1) * mm});
            skLineSegment(sketch, "E16.191.4", {"start": v(2.24, 100.46) * mm, "end": v(2.27, 100.16) * mm});
            skSolve(sketch);
        }
        {
            var Q0;
            Q0=makeQuery(id+"F0.imprint","IMPRINT",FACE,{"disambiguationData":[TD([[makeQuery(id+"F0.imprint","IMPRINT",EDGE,{"derivedFrom":sQuery(id+"F0.wireOp",EDGE,"0MEXwoFq-VW0W-JoZZ-MDqj-tHZCOfQ7mCeB")}),1.0]])]});
            var Q1;
            Q1=makeQuery(id+"F0.imprint","IMPRINT",FACE,{"disambiguationData":[TD([[makeQuery(id+"F0.imprint","IMPRINT",EDGE,{"derivedFrom":sQuery(id+"F0.wireOp",EDGE,"E0")}),-1.0]])]});
            extrude(context, id + "F1", {"entities" : qUnion([Q0, Q1]), "depth" : 20 * mm, "offsetDistance" : 25 * mm});
        }
        {
            var Q0;
            Q0=makeQuery(id+"F1.opExtrude","CAP_FACE",FACE,{"disambiguationData":[OSD([sQuery(id+"F0.wireOp",EDGE,"E0"),sQuery(id+"F0.wireOp",EDGE,"E4"),sQuery(id+"F0.wireOp",EDGE,"E5"),sQuery(id+"F0.wireOp",EDGE,"E6.filletArc"),sQuery(id+"F0.wireOp",EDGE,"E7.MirrorCS"),sQuery(id+"F0.wireOp",EDGE,"E8.MirrorCS"),sQuery(id+"F0.wireOp",EDGE,"E15"),sQuery(id+"F0.wireOp",EDGE,"E16.1.0"),sQuery(id+"F0.wireOp",EDGE,"E16.1.1"),sQuery(id+"F0.wireOp",EDGE,"E16.1.2"),sQuery(id+"F0.wireOp",EDGE,"E16.1.3"),sQuery(id+"F0.wireOp",EDGE,"E16.1.4"),sQuery(id+"F0.wireOp",EDGE,"E16.2.0"),sQuery(id+"F0.wireOp",EDGE,"E16.2.1"),sQuery(id+"F0.wireOp",EDGE,"E16.2.2"),sQuery(id+"F0.wireOp",EDGE,"E16.2.3"),sQuery(id+"F0.wireOp",EDGE,"E16.2.4"),sQuery(id+"F0.wireOp",EDGE,"E16.3.0"),sQuery(id+"F0.wireOp",EDGE,"E16.3.1"),sQuery(id+"F0.wireOp",EDGE,"E16.3.2"),sQuery(id+"F0.wireOp",EDGE,"E16.3.3"),sQuery(id+"F0.wireOp",EDGE,"E16.3.4"),sQuery(id+"F0.wireOp",EDGE,"E16.4.0"),sQuery(id+"F0.wireOp",EDGE,"E16.4.1"),sQuery(id+"F0.wireOp",EDGE,"E16.4.2"),sQuery(id+"F0.wireOp",EDGE,"E16.4.3"),sQuery(id+"F0.wireOp",EDGE,"E16.4.4"),sQuery(id+"F0.wireOp",EDGE,"E16.5.0"),sQuery(id+"F0.wireOp",EDGE,"E16.5.1"),sQuery(id+"F0.wireOp",EDGE,"E16.5.2"),sQuery(id+"F0.wireOp",EDGE,"E16.5.3"),sQuery(id+"F0.wireOp",EDGE,"E16.5.4"),sQuery(id+"F0.wireOp",EDGE,"E16.6.0"),sQuery(id+"F0.wireOp",EDGE,"E16.6.1"),sQuery(id+"F0.wireOp",EDGE,"E16.6.2"),sQuery(id+"F0.wireOp",EDGE,"E16.6.3"),sQuery(id+"F0.wireOp",EDGE,"E16.6.4"),sQuery(id+"F0.wireOp",EDGE,"E16.7.0"),sQuery(id+"F0.wireOp",EDGE,"E16.7.1"),sQuery(id+"F0.wireOp",EDGE,"E16.7.2"),sQuery(id+"F0.wireOp",EDGE,"E16.7.3"),sQuery(id+"F0.wireOp",EDGE,"E16.7.4"),sQuery(id+"F0.wireOp",EDGE,"E16.8.0"),sQuery(id+"F0.wireOp",EDGE,"E16.8.1"),sQuery(id+"F0.wireOp",EDGE,"E16.8.2"),sQuery(id+"F0.wireOp",EDGE,"E16.8.3"),sQuery(id+"F0.wireOp",EDGE,"E16.8.4"),sQuery(id+"F0.wireOp",EDGE,"E16.9.0"),sQuery(id+"F0.wireOp",EDGE,"E16.9.1"),sQuery(id+"F0.wireOp",EDGE,"E16.9.2"),sQuery(id+"F0.wireOp",EDGE,"E16.9.3"),sQuery(id+"F0.wireOp",EDGE,"E16.9.4"),sQuery(id+"F0.wireOp",EDGE,"E16.10.0"),sQuery(id+"F0.wireOp",EDGE,"E16.10.1"),sQuery(id+"F0.wireOp",EDGE,"E16.10.2"),sQuery(id+"F0.wireOp",EDGE,"E16.10.3"),sQuery(id+"F0.wireOp",EDGE,"E16.10.4"),sQuery(id+"F0.wireOp",EDGE,"E16.11.0"),sQuery(id+"F0.wireOp",EDGE,"E16.11.1"),sQuery(id+"F0.wireOp",EDGE,"E16.11.2"),sQuery(id+"F0.wireOp",EDGE,"E16.11.3"),sQuery(id+"F0.wireOp",EDGE,"E16.11.4"),sQuery(id+"F0.wireOp",EDGE,"E16.12.0"),sQuery(id+"F0.wireOp",EDGE,"E16.12.1"),sQuery(id+"F0.wireOp",EDGE,"E16.12.2"),sQuery(id+"F0.wireOp",EDGE,"E16.12.3"),sQuery(id+"F0.wireOp",EDGE,"E16.12.4"),sQuery(id+"F0.wireOp",EDGE,"E16.13.0"),sQuery(id+"F0.wireOp",EDGE,"E16.13.1"),sQuery(id+"F0.wireOp",EDGE,"E16.13.2"),sQuery(id+"F0.wireOp",EDGE,"E16.13.3"),sQuery(id+"F0.wireOp",EDGE,"E16.13.4"),sQuery(id+"F0.wireOp",EDGE,"E16.14.0"),sQuery(id+"F0.wireOp",EDGE,"E16.14.1"),sQuery(id+"F0.wireOp",EDGE,"E16.14.2"),sQuery(id+"F0.wireOp",EDGE,"E16.14.3"),sQuery(id+"F0.wireOp",EDGE,"E16.14.4"),sQuery(id+"F0.wireOp",EDGE,"E16.15.0"),sQuery(id+"F0.wireOp",EDGE,"E16.15.1"),sQuery(id+"F0.wireOp",EDGE,"E16.15.2"),sQuery(id+"F0.wireOp",EDGE,"E16.15.3"),sQuery(id+"F0.wireOp",EDGE,"E16.15.4"),sQuery(id+"F0.wireOp",EDGE,"E16.16.0"),sQuery(id+"F0.wireOp",EDGE,"E16.16.1"),sQuery(id+"F0.wireOp",EDGE,"E16.16.2"),sQuery(id+"F0.wireOp",EDGE,"E16.16.3"),sQuery(id+"F0.wireOp",EDGE,"E16.16.4"),sQuery(id+"F0.wireOp",EDGE,"E16.17.0"),sQuery(id+"F0.wireOp",EDGE,"E16.17.1"),sQuery(id+"F0.wireOp",EDGE,"E16.17.2"),sQuery(id+"F0.wireOp",EDGE,"E16.17.3"),sQuery(id+"F0.wireOp",EDGE,"E16.17.4"),sQuery(id+"F0.wireOp",EDGE,"E16.18.0"),sQuery(id+"F0.wireOp",EDGE,"E16.18.1"),sQuery(id+"F0.wireOp",EDGE,"E16.18.2"),sQuery(id+"F0.wireOp",EDGE,"E16.18.3"),sQuery(id+"F0.wireOp",EDGE,"E16.18.4"),sQuery(id+"F0.wireOp",EDGE,"E16.19.0"),sQuery(id+"F0.wireOp",EDGE,"E16.19.1"),sQuery(id+"F0.wireOp",EDGE,"E16.19.2"),sQuery(id+"F0.wireOp",EDGE,"E16.19.3"),sQuery(id+"F0.wireOp",EDGE,"E16.19.4"),sQuery(id+"F0.wireOp",EDGE,"E16.20.0"),sQuery(id+"F0.wireOp",EDGE,"E16.20.1"),sQuery(id+"F0.wireOp",EDGE,"E16.20.2"),sQuery(id+"F0.wireOp",EDGE,"E16.20.3"),sQuery(id+"F0.wireOp",EDGE,"E16.20.4"),sQuery(id+"F0.wireOp",EDGE,"E16.21.0"),sQuery(id+"F0.wireOp",EDGE,"E16.21.1"),sQuery(id+"F0.wireOp",EDGE,"E16.21.2"),sQuery(id+"F0.wireOp",EDGE,"E16.21.3"),sQuery(id+"F0.wireOp",EDGE,"E16.21.4"),sQuery(id+"F0.wireOp",EDGE,"E16.22.0"),sQuery(id+"F0.wireOp",EDGE,"E16.22.1"),sQuery(id+"F0.wireOp",EDGE,"E16.22.2"),sQuery(id+"F0.wireOp",EDGE,"E16.22.3"),sQuery(id+"F0.wireOp",EDGE,"E16.22.4"),sQuery(id+"F0.wireOp",EDGE,"E16.23.0"),sQuery(id+"F0.wireOp",EDGE,"E16.23.1"),sQuery(id+"F0.wireOp",EDGE,"E16.23.2"),sQuery(id+"F0.wireOp",EDGE,"E16.23.3"),sQuery(id+"F0.wireOp",EDGE,"E16.23.4"),sQuery(id+"F0.wireOp",EDGE,"E16.24.0"),sQuery(id+"F0.wireOp",EDGE,"E16.24.1"),sQuery(id+"F0.wireOp",EDGE,"E16.24.2"),sQuery(id+"F0.wireOp",EDGE,"E16.24.3"),sQuery(id+"F0.wireOp",EDGE,"E16.24.4"),sQuery(id+"F0.wireOp",EDGE,"E16.25.0"),sQuery(id+"F0.wireOp",EDGE,"E16.25.1"),sQuery(id+"F0.wireOp",EDGE,"E16.25.2"),sQuery(id+"F0.wireOp",EDGE,"E16.25.3"),sQuery(id+"F0.wireOp",EDGE,"E16.25.4"),sQuery(id+"F0.wireOp",EDGE,"E16.26.0"),sQuery(id+"F0.wireOp",EDGE,"E16.26.1"),sQuery(id+"F0.wireOp",EDGE,"E16.26.2"),sQuery(id+"F0.wireOp",EDGE,"E16.26.3"),sQuery(id+"F0.wireOp",EDGE,"E16.26.4"),sQuery(id+"F0.wireOp",EDGE,"E16.27.0"),sQuery(id+"F0.wireOp",EDGE,"E16.27.1"),sQuery(id+"F0.wireOp",EDGE,"E16.27.2"),sQuery(id+"F0.wireOp",EDGE,"E16.27.3"),sQuery(id+"F0.wireOp",EDGE,"E16.27.4"),sQuery(id+"F0.wireOp",EDGE,"E16.28.0"),sQuery(id+"F0.wireOp",EDGE,"E16.28.1"),sQuery(id+"F0.wireOp",EDGE,"E16.28.2"),sQuery(id+"F0.wireOp",EDGE,"E16.28.3"),sQuery(id+"F0.wireOp",EDGE,"E16.28.4"),sQuery(id+"F0.wireOp",EDGE,"E16.29.0"),sQuery(id+"F0.wireOp",EDGE,"E16.29.1"),sQuery(id+"F0.wireOp",EDGE,"E16.29.2"),sQuery(id+"F0.wireOp",EDGE,"E16.29.3"),sQuery(id+"F0.wireOp",EDGE,"E16.29.4"),sQuery(id+"F0.wireOp",EDGE,"E16.30.0"),sQuery(id+"F0.wireOp",EDGE,"E16.30.1"),sQuery(id+"F0.wireOp",EDGE,"E16.30.2"),sQuery(id+"F0.wireOp",EDGE,"E16.30.3"),sQuery(id+"F0.wireOp",EDGE,"E16.30.4"),sQuery(id+"F0.wireOp",EDGE,"E16.31.0"),sQuery(id+"F0.wireOp",EDGE,"E16.31.1"),sQuery(id+"F0.wireOp",EDGE,"E16.31.2"),sQuery(id+"F0.wireOp",EDGE,"E16.31.3"),sQuery(id+"F0.wireOp",EDGE,"E16.31.4"),sQuery(id+"F0.wireOp",EDGE,"E16.32.0"),sQuery(id+"F0.wireOp",EDGE,"E16.32.1"),sQuery(id+"F0.wireOp",EDGE,"E16.32.2"),sQuery(id+"F0.wireOp",EDGE,"E16.32.3"),sQuery(id+"F0.wireOp",EDGE,"E16.32.4"),sQuery(id+"F0.wireOp",EDGE,"E16.33.0"),sQuery(id+"F0.wireOp",EDGE,"E16.33.1"),sQuery(id+"F0.wireOp",EDGE,"E16.33.2"),sQuery(id+"F0.wireOp",EDGE,"E16.33.3"),sQuery(id+"F0.wireOp",EDGE,"E16.33.4"),sQuery(id+"F0.wireOp",EDGE,"E16.34.0"),sQuery(id+"F0.wireOp",EDGE,"E16.34.1"),sQuery(id+"F0.wireOp",EDGE,"E16.34.2"),sQuery(id+"F0.wireOp",EDGE,"E16.34.3"),sQuery(id+"F0.wireOp",EDGE,"E16.34.4"),sQuery(id+"F0.wireOp",EDGE,"E16.35.0"),sQuery(id+"F0.wireOp",EDGE,"E16.35.1"),sQuery(id+"F0.wireOp",EDGE,"E16.35.2"),sQuery(id+"F0.wireOp",EDGE,"E16.35.3"),sQuery(id+"F0.wireOp",EDGE,"E16.35.4"),sQuery(id+"F0.wireOp",EDGE,"E16.36.0"),sQuery(id+"F0.wireOp",EDGE,"E16.36.1"),sQuery(id+"F0.wireOp",EDGE,"E16.36.2"),sQuery(id+"F0.wireOp",EDGE,"E16.36.3"),sQuery(id+"F0.wireOp",EDGE,"E16.36.4"),sQuery(id+"F0.wireOp",EDGE,"E16.37.0"),sQuery(id+"F0.wireOp",EDGE,"E16.37.1"),sQuery(id+"F0.wireOp",EDGE,"E16.37.2"),sQuery(id+"F0.wireOp",EDGE,"E16.37.3"),sQuery(id+"F0.wireOp",EDGE,"E16.37.4"),sQuery(id+"F0.wireOp",EDGE,"E16.38.0"),sQuery(id+"F0.wireOp",EDGE,"E16.38.1"),sQuery(id+"F0.wireOp",EDGE,"E16.38.2"),sQuery(id+"F0.wireOp",EDGE,"E16.38.3"),sQuery(id+"F0.wireOp",EDGE,"E16.38.4"),sQuery(id+"F0.wireOp",EDGE,"E16.39.0"),sQuery(id+"F0.wireOp",EDGE,"E16.39.1"),sQuery(id+"F0.wireOp",EDGE,"E16.39.2"),sQuery(id+"F0.wireOp",EDGE,"E16.39.3"),sQuery(id+"F0.wireOp",EDGE,"E16.39.4"),sQuery(id+"F0.wireOp",EDGE,"E16.40.0"),sQuery(id+"F0.wireOp",EDGE,"E16.40.1"),sQuery(id+"F0.wireOp",EDGE,"E16.40.2"),sQuery(id+"F0.wireOp",EDGE,"E16.40.3"),sQuery(id+"F0.wireOp",EDGE,"E16.40.4"),sQuery(id+"F0.wireOp",EDGE,"E16.41.0"),sQuery(id+"F0.wireOp",EDGE,"E16.41.1"),sQuery(id+"F0.wireOp",EDGE,"E16.41.2"),sQuery(id+"F0.wireOp",EDGE,"E16.41.3"),sQuery(id+"F0.wireOp",EDGE,"E16.41.4"),sQuery(id+"F0.wireOp",EDGE,"E16.42.0"),sQuery(id+"F0.wireOp",EDGE,"E16.42.1"),sQuery(id+"F0.wireOp",EDGE,"E16.42.2"),sQuery(id+"F0.wireOp",EDGE,"E16.42.3"),sQuery(id+"F0.wireOp",EDGE,"E16.42.4"),sQuery(id+"F0.wireOp",EDGE,"E16.43.0"),sQuery(id+"F0.wireOp",EDGE,"E16.43.1"),sQuery(id+"F0.wireOp",EDGE,"E16.43.2"),sQuery(id+"F0.wireOp",EDGE,"E16.43.3"),sQuery(id+"F0.wireOp",EDGE,"E16.43.4"),sQuery(id+"F0.wireOp",EDGE,"E16.44.0"),sQuery(id+"F0.wireOp",EDGE,"E16.44.1"),sQuery(id+"F0.wireOp",EDGE,"E16.44.2"),sQuery(id+"F0.wireOp",EDGE,"E16.44.3"),sQuery(id+"F0.wireOp",EDGE,"E16.44.4"),sQuery(id+"F0.wireOp",EDGE,"E16.45.0"),sQuery(id+"F0.wireOp",EDGE,"E16.45.1"),sQuery(id+"F0.wireOp",EDGE,"E16.45.2"),sQuery(id+"F0.wireOp",EDGE,"E16.45.3"),sQuery(id+"F0.wireOp",EDGE,"E16.45.4"),sQuery(id+"F0.wireOp",EDGE,"E16.46.0"),sQuery(id+"F0.wireOp",EDGE,"E16.46.1"),sQuery(id+"F0.wireOp",EDGE,"E16.46.2"),sQuery(id+"F0.wireOp",EDGE,"E16.46.3"),sQuery(id+"F0.wireOp",EDGE,"E16.46.4"),sQuery(id+"F0.wireOp",EDGE,"E16.47.0"),sQuery(id+"F0.wireOp",EDGE,"E16.47.1"),sQuery(id+"F0.wireOp",EDGE,"E16.47.2"),sQuery(id+"F0.wireOp",EDGE,"E16.47.3"),sQuery(id+"F0.wireOp",EDGE,"E16.47.4"),sQuery(id+"F0.wireOp",EDGE,"E16.48.0"),sQuery(id+"F0.wireOp",EDGE,"E16.48.1"),sQuery(id+"F0.wireOp",EDGE,"E16.48.2"),sQuery(id+"F0.wireOp",EDGE,"E16.48.3"),sQuery(id+"F0.wireOp",EDGE,"E16.48.4"),sQuery(id+"F0.wireOp",EDGE,"E16.49.0"),sQuery(id+"F0.wireOp",EDGE,"E16.49.1"),sQuery(id+"F0.wireOp",EDGE,"E16.49.2"),sQuery(id+"F0.wireOp",EDGE,"E16.49.3"),sQuery(id+"F0.wireOp",EDGE,"E16.49.4"),sQuery(id+"F0.wireOp",EDGE,"E16.50.0"),sQuery(id+"F0.wireOp",EDGE,"E16.50.1"),sQuery(id+"F0.wireOp",EDGE,"E16.50.2"),sQuery(id+"F0.wireOp",EDGE,"E16.50.3"),sQuery(id+"F0.wireOp",EDGE,"E16.50.4"),sQuery(id+"F0.wireOp",EDGE,"E16.51.0"),sQuery(id+"F0.wireOp",EDGE,"E16.51.1"),sQuery(id+"F0.wireOp",EDGE,"E16.51.2"),sQuery(id+"F0.wireOp",EDGE,"E16.51.3"),sQuery(id+"F0.wireOp",EDGE,"E16.51.4"),sQuery(id+"F0.wireOp",EDGE,"E16.52.0"),sQuery(id+"F0.wireOp",EDGE,"E16.52.1"),sQuery(id+"F0.wireOp",EDGE,"E16.52.2"),sQuery(id+"F0.wireOp",EDGE,"E16.52.3"),sQuery(id+"F0.wireOp",EDGE,"E16.52.4"),sQuery(id+"F0.wireOp",EDGE,"E16.53.0"),sQuery(id+"F0.wireOp",EDGE,"E16.53.1"),sQuery(id+"F0.wireOp",EDGE,"E16.53.2"),sQuery(id+"F0.wireOp",EDGE,"E16.53.3"),sQuery(id+"F0.wireOp",EDGE,"E16.53.4"),sQuery(id+"F0.wireOp",EDGE,"E16.54.0"),sQuery(id+"F0.wireOp",EDGE,"E16.54.1"),sQuery(id+"F0.wireOp",EDGE,"E16.54.2"),sQuery(id+"F0.wireOp",EDGE,"E16.54.3"),sQuery(id+"F0.wireOp",EDGE,"E16.54.4"),sQuery(id+"F0.wireOp",EDGE,"E16.55.0"),sQuery(id+"F0.wireOp",EDGE,"E16.55.1"),sQuery(id+"F0.wireOp",EDGE,"E16.55.2"),sQuery(id+"F0.wireOp",EDGE,"E16.55.3"),sQuery(id+"F0.wireOp",EDGE,"E16.55.4"),sQuery(id+"F0.wireOp",EDGE,"E16.56.0"),sQuery(id+"F0.wireOp",EDGE,"E16.56.1"),sQuery(id+"F0.wireOp",EDGE,"E16.56.2"),sQuery(id+"F0.wireOp",EDGE,"E16.56.3"),sQuery(id+"F0.wireOp",EDGE,"E16.56.4"),sQuery(id+"F0.wireOp",EDGE,"E16.57.0"),sQuery(id+"F0.wireOp",EDGE,"E16.57.1"),sQuery(id+"F0.wireOp",EDGE,"E16.57.2"),sQuery(id+"F0.wireOp",EDGE,"E16.57.3"),sQuery(id+"F0.wireOp",EDGE,"E16.57.4"),sQuery(id+"F0.wireOp",EDGE,"E16.58.0"),sQuery(id+"F0.wireOp",EDGE,"E16.58.1"),sQuery(id+"F0.wireOp",EDGE,"E16.58.2"),sQuery(id+"F0.wireOp",EDGE,"E16.58.3"),sQuery(id+"F0.wireOp",EDGE,"E16.58.4"),sQuery(id+"F0.wireOp",EDGE,"E16.59.0"),sQuery(id+"F0.wireOp",EDGE,"E16.59.1"),sQuery(id+"F0.wireOp",EDGE,"E16.59.2"),sQuery(id+"F0.wireOp",EDGE,"E16.59.3"),sQuery(id+"F0.wireOp",EDGE,"E16.59.4"),sQuery(id+"F0.wireOp",EDGE,"E16.60.0"),sQuery(id+"F0.wireOp",EDGE,"E16.60.1"),sQuery(id+"F0.wireOp",EDGE,"E16.60.2"),sQuery(id+"F0.wireOp",EDGE,"E16.60.3"),sQuery(id+"F0.wireOp",EDGE,"E16.60.4"),sQuery(id+"F0.wireOp",EDGE,"E16.61.0"),sQuery(id+"F0.wireOp",EDGE,"E16.61.1"),sQuery(id+"F0.wireOp",EDGE,"E16.61.2"),sQuery(id+"F0.wireOp",EDGE,"E16.61.3"),sQuery(id+"F0.wireOp",EDGE,"E16.61.4"),sQuery(id+"F0.wireOp",EDGE,"E16.62.0"),sQuery(id+"F0.wireOp",EDGE,"E16.62.1"),sQuery(id+"F0.wireOp",EDGE,"E16.62.2"),sQuery(id+"F0.wireOp",EDGE,"E16.62.3"),sQuery(id+"F0.wireOp",EDGE,"E16.62.4"),sQuery(id+"F0.wireOp",EDGE,"E16.63.0"),sQuery(id+"F0.wireOp",EDGE,"E16.63.1"),sQuery(id+"F0.wireOp",EDGE,"E16.63.2"),sQuery(id+"F0.wireOp",EDGE,"E16.63.3"),sQuery(id+"F0.wireOp",EDGE,"E16.63.4"),sQuery(id+"F0.wireOp",EDGE,"E16.64.0"),sQuery(id+"F0.wireOp",EDGE,"E16.64.1"),sQuery(id+"F0.wireOp",EDGE,"E16.64.2"),sQuery(id+"F0.wireOp",EDGE,"E16.64.3"),sQuery(id+"F0.wireOp",EDGE,"E16.64.4"),sQuery(id+"F0.wireOp",EDGE,"E16.65.0"),sQuery(id+"F0.wireOp",EDGE,"E16.65.1"),sQuery(id+"F0.wireOp",EDGE,"E16.65.2"),sQuery(id+"F0.wireOp",EDGE,"E16.65.3"),sQuery(id+"F0.wireOp",EDGE,"E16.65.4"),sQuery(id+"F0.wireOp",EDGE,"E16.66.0"),sQuery(id+"F0.wireOp",EDGE,"E16.66.1"),sQuery(id+"F0.wireOp",EDGE,"E16.66.2"),sQuery(id+"F0.wireOp",EDGE,"E16.66.3"),sQuery(id+"F0.wireOp",EDGE,"E16.66.4"),sQuery(id+"F0.wireOp",EDGE,"E16.67.0"),sQuery(id+"F0.wireOp",EDGE,"E16.67.1"),sQuery(id+"F0.wireOp",EDGE,"E16.67.2"),sQuery(id+"F0.wireOp",EDGE,"E16.67.3"),sQuery(id+"F0.wireOp",EDGE,"E16.67.4"),sQuery(id+"F0.wireOp",EDGE,"E16.68.0"),sQuery(id+"F0.wireOp",EDGE,"E16.68.1"),sQuery(id+"F0.wireOp",EDGE,"E16.68.2"),sQuery(id+"F0.wireOp",EDGE,"E16.68.3"),sQuery(id+"F0.wireOp",EDGE,"E16.68.4"),sQuery(id+"F0.wireOp",EDGE,"E16.69.0"),sQuery(id+"F0.wireOp",EDGE,"E16.69.1"),sQuery(id+"F0.wireOp",EDGE,"E16.69.2"),sQuery(id+"F0.wireOp",EDGE,"E16.69.3"),sQuery(id+"F0.wireOp",EDGE,"E16.69.4"),sQuery(id+"F0.wireOp",EDGE,"E16.70.0"),sQuery(id+"F0.wireOp",EDGE,"E16.70.1"),sQuery(id+"F0.wireOp",EDGE,"E16.70.2"),sQuery(id+"F0.wireOp",EDGE,"E16.70.3"),sQuery(id+"F0.wireOp",EDGE,"E16.70.4"),sQuery(id+"F0.wireOp",EDGE,"E16.71.0"),sQuery(id+"F0.wireOp",EDGE,"E16.71.1"),sQuery(id+"F0.wireOp",EDGE,"E16.71.2"),sQuery(id+"F0.wireOp",EDGE,"E16.71.3"),sQuery(id+"F0.wireOp",EDGE,"E16.71.4"),sQuery(id+"F0.wireOp",EDGE,"E16.72.0"),sQuery(id+"F0.wireOp",EDGE,"E16.72.1"),sQuery(id+"F0.wireOp",EDGE,"E16.72.2"),sQuery(id+"F0.wireOp",EDGE,"E16.72.3"),sQuery(id+"F0.wireOp",EDGE,"E16.72.4"),sQuery(id+"F0.wireOp",EDGE,"E16.73.0"),sQuery(id+"F0.wireOp",EDGE,"E16.73.1"),sQuery(id+"F0.wireOp",EDGE,"E16.73.2"),sQuery(id+"F0.wireOp",EDGE,"E16.73.3"),sQuery(id+"F0.wireOp",EDGE,"E16.73.4"),sQuery(id+"F0.wireOp",EDGE,"E16.74.0"),sQuery(id+"F0.wireOp",EDGE,"E16.74.1"),sQuery(id+"F0.wireOp",EDGE,"E16.74.2"),sQuery(id+"F0.wireOp",EDGE,"E16.74.3"),sQuery(id+"F0.wireOp",EDGE,"E16.74.4"),sQuery(id+"F0.wireOp",EDGE,"E16.75.0"),sQuery(id+"F0.wireOp",EDGE,"E16.75.1"),sQuery(id+"F0.wireOp",EDGE,"E16.75.2"),sQuery(id+"F0.wireOp",EDGE,"E16.75.3"),sQuery(id+"F0.wireOp",EDGE,"E16.75.4"),sQuery(id+"F0.wireOp",EDGE,"E16.76.0"),sQuery(id+"F0.wireOp",EDGE,"E16.76.1"),sQuery(id+"F0.wireOp",EDGE,"E16.76.2"),sQuery(id+"F0.wireOp",EDGE,"E16.76.3"),sQuery(id+"F0.wireOp",EDGE,"E16.76.4"),sQuery(id+"F0.wireOp",EDGE,"E16.77.0"),sQuery(id+"F0.wireOp",EDGE,"E16.77.1"),sQuery(id+"F0.wireOp",EDGE,"E16.77.2"),sQuery(id+"F0.wireOp",EDGE,"E16.77.3"),sQuery(id+"F0.wireOp",EDGE,"E16.77.4"),sQuery(id+"F0.wireOp",EDGE,"E16.78.0"),sQuery(id+"F0.wireOp",EDGE,"E16.78.1"),sQuery(id+"F0.wireOp",EDGE,"E16.78.2"),sQuery(id+"F0.wireOp",EDGE,"E16.78.3"),sQuery(id+"F0.wireOp",EDGE,"E16.78.4"),sQuery(id+"F0.wireOp",EDGE,"E16.79.0"),sQuery(id+"F0.wireOp",EDGE,"E16.79.1"),sQuery(id+"F0.wireOp",EDGE,"E16.79.2"),sQuery(id+"F0.wireOp",EDGE,"E16.79.3"),sQuery(id+"F0.wireOp",EDGE,"E16.79.4"),sQuery(id+"F0.wireOp",EDGE,"E16.80.0"),sQuery(id+"F0.wireOp",EDGE,"E16.80.1"),sQuery(id+"F0.wireOp",EDGE,"E16.80.2"),sQuery(id+"F0.wireOp",EDGE,"E16.80.3"),sQuery(id+"F0.wireOp",EDGE,"E16.80.4"),sQuery(id+"F0.wireOp",EDGE,"E16.81.0"),sQuery(id+"F0.wireOp",EDGE,"E16.81.1"),sQuery(id+"F0.wireOp",EDGE,"E16.81.2"),sQuery(id+"F0.wireOp",EDGE,"E16.81.3"),sQuery(id+"F0.wireOp",EDGE,"E16.81.4"),sQuery(id+"F0.wireOp",EDGE,"E16.82.0"),sQuery(id+"F0.wireOp",EDGE,"E16.82.1"),sQuery(id+"F0.wireOp",EDGE,"E16.82.2"),sQuery(id+"F0.wireOp",EDGE,"E16.82.3"),sQuery(id+"F0.wireOp",EDGE,"E16.82.4"),sQuery(id+"F0.wireOp",EDGE,"E16.83.0"),sQuery(id+"F0.wireOp",EDGE,"E16.83.1"),sQuery(id+"F0.wireOp",EDGE,"E16.83.2"),sQuery(id+"F0.wireOp",EDGE,"E16.83.3"),sQuery(id+"F0.wireOp",EDGE,"E16.83.4"),sQuery(id+"F0.wireOp",EDGE,"E16.84.0"),sQuery(id+"F0.wireOp",EDGE,"E16.84.1"),sQuery(id+"F0.wireOp",EDGE,"E16.84.2"),sQuery(id+"F0.wireOp",EDGE,"E16.84.3"),sQuery(id+"F0.wireOp",EDGE,"E16.84.4"),sQuery(id+"F0.wireOp",EDGE,"E16.85.0"),sQuery(id+"F0.wireOp",EDGE,"E16.85.1"),sQuery(id+"F0.wireOp",EDGE,"E16.85.2"),sQuery(id+"F0.wireOp",EDGE,"E16.85.3"),sQuery(id+"F0.wireOp",EDGE,"E16.85.4"),sQuery(id+"F0.wireOp",EDGE,"E16.86.0"),sQuery(id+"F0.wireOp",EDGE,"E16.86.1"),sQuery(id+"F0.wireOp",EDGE,"E16.86.2"),sQuery(id+"F0.wireOp",EDGE,"E16.86.3"),sQuery(id+"F0.wireOp",EDGE,"E16.86.4"),sQuery(id+"F0.wireOp",EDGE,"E16.87.0"),sQuery(id+"F0.wireOp",EDGE,"E16.87.1"),sQuery(id+"F0.wireOp",EDGE,"E16.87.2"),sQuery(id+"F0.wireOp",EDGE,"E16.87.3"),sQuery(id+"F0.wireOp",EDGE,"E16.87.4"),sQuery(id+"F0.wireOp",EDGE,"E16.88.0"),sQuery(id+"F0.wireOp",EDGE,"E16.88.1"),sQuery(id+"F0.wireOp",EDGE,"E16.88.2"),sQuery(id+"F0.wireOp",EDGE,"E16.88.3"),sQuery(id+"F0.wireOp",EDGE,"E16.88.4"),sQuery(id+"F0.wireOp",EDGE,"E16.89.0"),sQuery(id+"F0.wireOp",EDGE,"E16.89.1"),sQuery(id+"F0.wireOp",EDGE,"E16.89.2"),sQuery(id+"F0.wireOp",EDGE,"E16.89.3"),sQuery(id+"F0.wireOp",EDGE,"E16.89.4"),sQuery(id+"F0.wireOp",EDGE,"E16.90.0"),sQuery(id+"F0.wireOp",EDGE,"E16.90.1"),sQuery(id+"F0.wireOp",EDGE,"E16.90.2"),sQuery(id+"F0.wireOp",EDGE,"E16.90.3"),sQuery(id+"F0.wireOp",EDGE,"E16.90.4"),sQuery(id+"F0.wireOp",EDGE,"E16.91.0"),sQuery(id+"F0.wireOp",EDGE,"E16.91.1"),sQuery(id+"F0.wireOp",EDGE,"E16.91.2"),sQuery(id+"F0.wireOp",EDGE,"E16.91.3"),sQuery(id+"F0.wireOp",EDGE,"E16.91.4"),sQuery(id+"F0.wireOp",EDGE,"E16.92.0"),sQuery(id+"F0.wireOp",EDGE,"E16.92.1"),sQuery(id+"F0.wireOp",EDGE,"E16.92.2"),sQuery(id+"F0.wireOp",EDGE,"E16.92.3"),sQuery(id+"F0.wireOp",EDGE,"E16.92.4"),sQuery(id+"F0.wireOp",EDGE,"E16.93.0"),sQuery(id+"F0.wireOp",EDGE,"E16.93.1"),sQuery(id+"F0.wireOp",EDGE,"E16.93.2"),sQuery(id+"F0.wireOp",EDGE,"E16.93.3"),sQuery(id+"F0.wireOp",EDGE,"E16.93.4"),sQuery(id+"F0.wireOp",EDGE,"E16.94.0"),sQuery(id+"F0.wireOp",EDGE,"E16.94.1"),sQuery(id+"F0.wireOp",EDGE,"E16.94.2"),sQuery(id+"F0.wireOp",EDGE,"E16.94.3"),sQuery(id+"F0.wireOp",EDGE,"E16.94.4"),sQuery(id+"F0.wireOp",EDGE,"E16.95.0"),sQuery(id+"F0.wireOp",EDGE,"E16.95.1"),sQuery(id+"F0.wireOp",EDGE,"E16.95.2"),sQuery(id+"F0.wireOp",EDGE,"E16.95.3"),sQuery(id+"F0.wireOp",EDGE,"E16.95.4"),sQuery(id+"F0.wireOp",EDGE,"E16.96.0"),sQuery(id+"F0.wireOp",EDGE,"E16.96.1"),sQuery(id+"F0.wireOp",EDGE,"E16.96.2"),sQuery(id+"F0.wireOp",EDGE,"E16.96.3"),sQuery(id+"F0.wireOp",EDGE,"E16.96.4"),sQuery(id+"F0.wireOp",EDGE,"E16.97.0"),sQuery(id+"F0.wireOp",EDGE,"E16.97.1"),sQuery(id+"F0.wireOp",EDGE,"E16.97.2"),sQuery(id+"F0.wireOp",EDGE,"E16.97.3"),sQuery(id+"F0.wireOp",EDGE,"E16.97.4"),sQuery(id+"F0.wireOp",EDGE,"E16.98.0"),sQuery(id+"F0.wireOp",EDGE,"E16.98.1"),sQuery(id+"F0.wireOp",EDGE,"E16.98.2"),sQuery(id+"F0.wireOp",EDGE,"E16.98.3"),sQuery(id+"F0.wireOp",EDGE,"E16.98.4"),sQuery(id+"F0.wireOp",EDGE,"E16.99.0"),sQuery(id+"F0.wireOp",EDGE,"E16.99.1"),sQuery(id+"F0.wireOp",EDGE,"E16.99.2"),sQuery(id+"F0.wireOp",EDGE,"E16.99.3"),sQuery(id+"F0.wireOp",EDGE,"E16.99.4"),sQuery(id+"F0.wireOp",EDGE,"E16.100.0"),sQuery(id+"F0.wireOp",EDGE,"E16.100.1"),sQuery(id+"F0.wireOp",EDGE,"E16.100.2"),sQuery(id+"F0.wireOp",EDGE,"E16.100.3"),sQuery(id+"F0.wireOp",EDGE,"E16.100.4"),sQuery(id+"F0.wireOp",EDGE,"E16.101.0"),sQuery(id+"F0.wireOp",EDGE,"E16.101.1"),sQuery(id+"F0.wireOp",EDGE,"E16.101.2"),sQuery(id+"F0.wireOp",EDGE,"E16.101.3"),sQuery(id+"F0.wireOp",EDGE,"E16.101.4"),sQuery(id+"F0.wireOp",EDGE,"E16.102.0"),sQuery(id+"F0.wireOp",EDGE,"E16.102.1"),sQuery(id+"F0.wireOp",EDGE,"E16.102.2"),sQuery(id+"F0.wireOp",EDGE,"E16.102.3"),sQuery(id+"F0.wireOp",EDGE,"E16.102.4"),sQuery(id+"F0.wireOp",EDGE,"E16.103.0"),sQuery(id+"F0.wireOp",EDGE,"E16.103.1"),sQuery(id+"F0.wireOp",EDGE,"E16.103.2"),sQuery(id+"F0.wireOp",EDGE,"E16.103.3"),sQuery(id+"F0.wireOp",EDGE,"E16.103.4"),sQuery(id+"F0.wireOp",EDGE,"E16.104.0"),sQuery(id+"F0.wireOp",EDGE,"E16.104.1"),sQuery(id+"F0.wireOp",EDGE,"E16.104.2"),sQuery(id+"F0.wireOp",EDGE,"E16.104.3"),sQuery(id+"F0.wireOp",EDGE,"E16.104.4"),sQuery(id+"F0.wireOp",EDGE,"E16.105.0"),sQuery(id+"F0.wireOp",EDGE,"E16.105.1"),sQuery(id+"F0.wireOp",EDGE,"E16.105.2"),sQuery(id+"F0.wireOp",EDGE,"E16.105.3"),sQuery(id+"F0.wireOp",EDGE,"E16.105.4"),sQuery(id+"F0.wireOp",EDGE,"E16.106.0"),sQuery(id+"F0.wireOp",EDGE,"E16.106.1"),sQuery(id+"F0.wireOp",EDGE,"E16.106.2"),sQuery(id+"F0.wireOp",EDGE,"E16.106.3"),sQuery(id+"F0.wireOp",EDGE,"E16.106.4"),sQuery(id+"F0.wireOp",EDGE,"E16.107.0"),sQuery(id+"F0.wireOp",EDGE,"E16.107.1"),sQuery(id+"F0.wireOp",EDGE,"E16.107.2"),sQuery(id+"F0.wireOp",EDGE,"E16.107.3"),sQuery(id+"F0.wireOp",EDGE,"E16.107.4"),sQuery(id+"F0.wireOp",EDGE,"E16.108.0"),sQuery(id+"F0.wireOp",EDGE,"E16.108.1"),sQuery(id+"F0.wireOp",EDGE,"E16.108.2"),sQuery(id+"F0.wireOp",EDGE,"E16.108.3"),sQuery(id+"F0.wireOp",EDGE,"E16.108.4"),sQuery(id+"F0.wireOp",EDGE,"E16.109.0"),sQuery(id+"F0.wireOp",EDGE,"E16.109.1"),sQuery(id+"F0.wireOp",EDGE,"E16.109.2"),sQuery(id+"F0.wireOp",EDGE,"E16.109.3"),sQuery(id+"F0.wireOp",EDGE,"E16.109.4"),sQuery(id+"F0.wireOp",EDGE,"E16.110.0"),sQuery(id+"F0.wireOp",EDGE,"E16.110.1"),sQuery(id+"F0.wireOp",EDGE,"E16.110.2"),sQuery(id+"F0.wireOp",EDGE,"E16.110.3"),sQuery(id+"F0.wireOp",EDGE,"E16.110.4"),sQuery(id+"F0.wireOp",EDGE,"E16.111.0"),sQuery(id+"F0.wireOp",EDGE,"E16.111.1"),sQuery(id+"F0.wireOp",EDGE,"E16.111.2"),sQuery(id+"F0.wireOp",EDGE,"E16.111.3"),sQuery(id+"F0.wireOp",EDGE,"E16.111.4"),sQuery(id+"F0.wireOp",EDGE,"E16.112.0"),sQuery(id+"F0.wireOp",EDGE,"E16.112.1"),sQuery(id+"F0.wireOp",EDGE,"E16.112.2"),sQuery(id+"F0.wireOp",EDGE,"E16.112.3"),sQuery(id+"F0.wireOp",EDGE,"E16.112.4"),sQuery(id+"F0.wireOp",EDGE,"E16.113.0"),sQuery(id+"F0.wireOp",EDGE,"E16.113.1"),sQuery(id+"F0.wireOp",EDGE,"E16.113.2"),sQuery(id+"F0.wireOp",EDGE,"E16.113.3"),sQuery(id+"F0.wireOp",EDGE,"E16.113.4"),sQuery(id+"F0.wireOp",EDGE,"E16.114.0"),sQuery(id+"F0.wireOp",EDGE,"E16.114.1"),sQuery(id+"F0.wireOp",EDGE,"E16.114.2"),sQuery(id+"F0.wireOp",EDGE,"E16.114.3"),sQuery(id+"F0.wireOp",EDGE,"E16.114.4"),sQuery(id+"F0.wireOp",EDGE,"E16.115.0"),sQuery(id+"F0.wireOp",EDGE,"E16.115.1"),sQuery(id+"F0.wireOp",EDGE,"E16.115.2"),sQuery(id+"F0.wireOp",EDGE,"E16.115.3"),sQuery(id+"F0.wireOp",EDGE,"E16.115.4"),sQuery(id+"F0.wireOp",EDGE,"E16.116.0"),sQuery(id+"F0.wireOp",EDGE,"E16.116.1"),sQuery(id+"F0.wireOp",EDGE,"E16.116.2"),sQuery(id+"F0.wireOp",EDGE,"E16.116.3"),sQuery(id+"F0.wireOp",EDGE,"E16.116.4"),sQuery(id+"F0.wireOp",EDGE,"E16.117.0"),sQuery(id+"F0.wireOp",EDGE,"E16.117.1"),sQuery(id+"F0.wireOp",EDGE,"E16.117.2"),sQuery(id+"F0.wireOp",EDGE,"E16.117.3"),sQuery(id+"F0.wireOp",EDGE,"E16.117.4"),sQuery(id+"F0.wireOp",EDGE,"E16.118.0"),sQuery(id+"F0.wireOp",EDGE,"E16.118.1"),sQuery(id+"F0.wireOp",EDGE,"E16.118.2"),sQuery(id+"F0.wireOp",EDGE,"E16.118.3"),sQuery(id+"F0.wireOp",EDGE,"E16.118.4"),sQuery(id+"F0.wireOp",EDGE,"E16.119.0"),sQuery(id+"F0.wireOp",EDGE,"E16.119.1"),sQuery(id+"F0.wireOp",EDGE,"E16.119.2"),sQuery(id+"F0.wireOp",EDGE,"E16.119.3"),sQuery(id+"F0.wireOp",EDGE,"E16.119.4"),sQuery(id+"F0.wireOp",EDGE,"E16.120.0"),sQuery(id+"F0.wireOp",EDGE,"E16.120.1"),sQuery(id+"F0.wireOp",EDGE,"E16.120.2"),sQuery(id+"F0.wireOp",EDGE,"E16.120.3"),sQuery(id+"F0.wireOp",EDGE,"E16.120.4"),sQuery(id+"F0.wireOp",EDGE,"E16.121.0"),sQuery(id+"F0.wireOp",EDGE,"E16.121.1"),sQuery(id+"F0.wireOp",EDGE,"E16.121.2"),sQuery(id+"F0.wireOp",EDGE,"E16.121.3"),sQuery(id+"F0.wireOp",EDGE,"E16.121.4"),sQuery(id+"F0.wireOp",EDGE,"E16.122.0"),sQuery(id+"F0.wireOp",EDGE,"E16.122.1"),sQuery(id+"F0.wireOp",EDGE,"E16.122.2"),sQuery(id+"F0.wireOp",EDGE,"E16.122.3"),sQuery(id+"F0.wireOp",EDGE,"E16.122.4"),sQuery(id+"F0.wireOp",EDGE,"E16.123.0"),sQuery(id+"F0.wireOp",EDGE,"E16.123.1"),sQuery(id+"F0.wireOp",EDGE,"E16.123.2"),sQuery(id+"F0.wireOp",EDGE,"E16.123.3"),sQuery(id+"F0.wireOp",EDGE,"E16.123.4"),sQuery(id+"F0.wireOp",EDGE,"E16.124.0"),sQuery(id+"F0.wireOp",EDGE,"E16.124.1"),sQuery(id+"F0.wireOp",EDGE,"E16.124.2"),sQuery(id+"F0.wireOp",EDGE,"E16.124.3"),sQuery(id+"F0.wireOp",EDGE,"E16.124.4"),sQuery(id+"F0.wireOp",EDGE,"E16.125.0"),sQuery(id+"F0.wireOp",EDGE,"E16.125.1"),sQuery(id+"F0.wireOp",EDGE,"E16.125.2"),sQuery(id+"F0.wireOp",EDGE,"E16.125.3"),sQuery(id+"F0.wireOp",EDGE,"E16.125.4"),sQuery(id+"F0.wireOp",EDGE,"E16.126.0"),sQuery(id+"F0.wireOp",EDGE,"E16.126.1"),sQuery(id+"F0.wireOp",EDGE,"E16.126.2"),sQuery(id+"F0.wireOp",EDGE,"E16.126.3"),sQuery(id+"F0.wireOp",EDGE,"E16.126.4"),sQuery(id+"F0.wireOp",EDGE,"E16.127.0"),sQuery(id+"F0.wireOp",EDGE,"E16.127.1"),sQuery(id+"F0.wireOp",EDGE,"E16.127.2"),sQuery(id+"F0.wireOp",EDGE,"E16.127.3"),sQuery(id+"F0.wireOp",EDGE,"E16.127.4"),sQuery(id+"F0.wireOp",EDGE,"E16.128.0"),sQuery(id+"F0.wireOp",EDGE,"E16.128.1"),sQuery(id+"F0.wireOp",EDGE,"E16.128.2"),sQuery(id+"F0.wireOp",EDGE,"E16.128.3"),sQuery(id+"F0.wireOp",EDGE,"E16.128.4"),sQuery(id+"F0.wireOp",EDGE,"E16.129.0"),sQuery(id+"F0.wireOp",EDGE,"E16.129.1"),sQuery(id+"F0.wireOp",EDGE,"E16.129.2"),sQuery(id+"F0.wireOp",EDGE,"E16.129.3"),sQuery(id+"F0.wireOp",EDGE,"E16.129.4"),sQuery(id+"F0.wireOp",EDGE,"E16.130.0"),sQuery(id+"F0.wireOp",EDGE,"E16.130.1"),sQuery(id+"F0.wireOp",EDGE,"E16.130.2"),sQuery(id+"F0.wireOp",EDGE,"E16.130.3"),sQuery(id+"F0.wireOp",EDGE,"E16.130.4"),sQuery(id+"F0.wireOp",EDGE,"E16.131.0"),sQuery(id+"F0.wireOp",EDGE,"E16.131.1"),sQuery(id+"F0.wireOp",EDGE,"E16.131.2"),sQuery(id+"F0.wireOp",EDGE,"E16.131.3"),sQuery(id+"F0.wireOp",EDGE,"E16.131.4"),sQuery(id+"F0.wireOp",EDGE,"E16.132.0"),sQuery(id+"F0.wireOp",EDGE,"E16.132.1"),sQuery(id+"F0.wireOp",EDGE,"E16.132.2"),sQuery(id+"F0.wireOp",EDGE,"E16.132.3"),sQuery(id+"F0.wireOp",EDGE,"E16.132.4"),sQuery(id+"F0.wireOp",EDGE,"E16.133.0"),sQuery(id+"F0.wireOp",EDGE,"E16.133.1"),sQuery(id+"F0.wireOp",EDGE,"E16.133.2"),sQuery(id+"F0.wireOp",EDGE,"E16.133.3"),sQuery(id+"F0.wireOp",EDGE,"E16.133.4"),sQuery(id+"F0.wireOp",EDGE,"E16.134.0"),sQuery(id+"F0.wireOp",EDGE,"E16.134.1"),sQuery(id+"F0.wireOp",EDGE,"E16.134.2"),sQuery(id+"F0.wireOp",EDGE,"E16.134.3"),sQuery(id+"F0.wireOp",EDGE,"E16.134.4"),sQuery(id+"F0.wireOp",EDGE,"E16.135.0"),sQuery(id+"F0.wireOp",EDGE,"E16.135.1"),sQuery(id+"F0.wireOp",EDGE,"E16.135.2"),sQuery(id+"F0.wireOp",EDGE,"E16.135.3"),sQuery(id+"F0.wireOp",EDGE,"E16.135.4"),sQuery(id+"F0.wireOp",EDGE,"E16.136.0"),sQuery(id+"F0.wireOp",EDGE,"E16.136.1"),sQuery(id+"F0.wireOp",EDGE,"E16.136.2"),sQuery(id+"F0.wireOp",EDGE,"E16.136.3"),sQuery(id+"F0.wireOp",EDGE,"E16.136.4"),sQuery(id+"F0.wireOp",EDGE,"E16.137.0"),sQuery(id+"F0.wireOp",EDGE,"E16.137.1"),sQuery(id+"F0.wireOp",EDGE,"E16.137.2"),sQuery(id+"F0.wireOp",EDGE,"E16.137.3"),sQuery(id+"F0.wireOp",EDGE,"E16.137.4"),sQuery(id+"F0.wireOp",EDGE,"E16.138.0"),sQuery(id+"F0.wireOp",EDGE,"E16.138.1"),sQuery(id+"F0.wireOp",EDGE,"E16.138.2"),sQuery(id+"F0.wireOp",EDGE,"E16.138.3"),sQuery(id+"F0.wireOp",EDGE,"E16.138.4"),sQuery(id+"F0.wireOp",EDGE,"E16.139.0"),sQuery(id+"F0.wireOp",EDGE,"E16.139.1"),sQuery(id+"F0.wireOp",EDGE,"E16.139.2"),sQuery(id+"F0.wireOp",EDGE,"E16.139.3"),sQuery(id+"F0.wireOp",EDGE,"E16.139.4"),sQuery(id+"F0.wireOp",EDGE,"E16.140.0"),sQuery(id+"F0.wireOp",EDGE,"E16.140.1"),sQuery(id+"F0.wireOp",EDGE,"E16.140.2"),sQuery(id+"F0.wireOp",EDGE,"E16.140.3"),sQuery(id+"F0.wireOp",EDGE,"E16.140.4"),sQuery(id+"F0.wireOp",EDGE,"E16.141.0"),sQuery(id+"F0.wireOp",EDGE,"E16.141.1"),sQuery(id+"F0.wireOp",EDGE,"E16.141.2"),sQuery(id+"F0.wireOp",EDGE,"E16.141.3"),sQuery(id+"F0.wireOp",EDGE,"E16.141.4"),sQuery(id+"F0.wireOp",EDGE,"E16.142.0"),sQuery(id+"F0.wireOp",EDGE,"E16.142.1"),sQuery(id+"F0.wireOp",EDGE,"E16.142.2"),sQuery(id+"F0.wireOp",EDGE,"E16.142.3"),sQuery(id+"F0.wireOp",EDGE,"E16.142.4"),sQuery(id+"F0.wireOp",EDGE,"E16.143.0"),sQuery(id+"F0.wireOp",EDGE,"E16.143.1"),sQuery(id+"F0.wireOp",EDGE,"E16.143.2"),sQuery(id+"F0.wireOp",EDGE,"E16.143.3"),sQuery(id+"F0.wireOp",EDGE,"E16.143.4"),sQuery(id+"F0.wireOp",EDGE,"E16.144.0"),sQuery(id+"F0.wireOp",EDGE,"E16.144.1"),sQuery(id+"F0.wireOp",EDGE,"E16.144.2"),sQuery(id+"F0.wireOp",EDGE,"E16.144.3"),sQuery(id+"F0.wireOp",EDGE,"E16.144.4"),sQuery(id+"F0.wireOp",EDGE,"E16.145.0"),sQuery(id+"F0.wireOp",EDGE,"E16.145.1"),sQuery(id+"F0.wireOp",EDGE,"E16.145.2"),sQuery(id+"F0.wireOp",EDGE,"E16.145.3"),sQuery(id+"F0.wireOp",EDGE,"E16.145.4"),sQuery(id+"F0.wireOp",EDGE,"E16.146.0"),sQuery(id+"F0.wireOp",EDGE,"E16.146.1"),sQuery(id+"F0.wireOp",EDGE,"E16.146.2"),sQuery(id+"F0.wireOp",EDGE,"E16.146.3"),sQuery(id+"F0.wireOp",EDGE,"E16.146.4"),sQuery(id+"F0.wireOp",EDGE,"E16.147.0"),sQuery(id+"F0.wireOp",EDGE,"E16.147.1"),sQuery(id+"F0.wireOp",EDGE,"E16.147.2"),sQuery(id+"F0.wireOp",EDGE,"E16.147.3"),sQuery(id+"F0.wireOp",EDGE,"E16.147.4"),sQuery(id+"F0.wireOp",EDGE,"E16.148.0"),sQuery(id+"F0.wireOp",EDGE,"E16.148.1"),sQuery(id+"F0.wireOp",EDGE,"E16.148.2"),sQuery(id+"F0.wireOp",EDGE,"E16.148.3"),sQuery(id+"F0.wireOp",EDGE,"E16.148.4"),sQuery(id+"F0.wireOp",EDGE,"E16.149.0"),sQuery(id+"F0.wireOp",EDGE,"E16.149.1"),sQuery(id+"F0.wireOp",EDGE,"E16.149.2"),sQuery(id+"F0.wireOp",EDGE,"E16.149.3"),sQuery(id+"F0.wireOp",EDGE,"E16.149.4"),sQuery(id+"F0.wireOp",EDGE,"E16.150.0"),sQuery(id+"F0.wireOp",EDGE,"E16.150.1"),sQuery(id+"F0.wireOp",EDGE,"E16.150.2"),sQuery(id+"F0.wireOp",EDGE,"E16.150.3"),sQuery(id+"F0.wireOp",EDGE,"E16.150.4"),sQuery(id+"F0.wireOp",EDGE,"E16.151.0"),sQuery(id+"F0.wireOp",EDGE,"E16.151.1"),sQuery(id+"F0.wireOp",EDGE,"E16.151.2"),sQuery(id+"F0.wireOp",EDGE,"E16.151.3"),sQuery(id+"F0.wireOp",EDGE,"E16.151.4"),sQuery(id+"F0.wireOp",EDGE,"E16.152.0"),sQuery(id+"F0.wireOp",EDGE,"E16.152.1"),sQuery(id+"F0.wireOp",EDGE,"E16.152.2"),sQuery(id+"F0.wireOp",EDGE,"E16.152.3"),sQuery(id+"F0.wireOp",EDGE,"E16.152.4"),sQuery(id+"F0.wireOp",EDGE,"E16.153.0"),sQuery(id+"F0.wireOp",EDGE,"E16.153.1"),sQuery(id+"F0.wireOp",EDGE,"E16.153.2"),sQuery(id+"F0.wireOp",EDGE,"E16.153.3"),sQuery(id+"F0.wireOp",EDGE,"E16.153.4"),sQuery(id+"F0.wireOp",EDGE,"E16.154.0"),sQuery(id+"F0.wireOp",EDGE,"E16.154.1"),sQuery(id+"F0.wireOp",EDGE,"E16.154.2"),sQuery(id+"F0.wireOp",EDGE,"E16.154.3"),sQuery(id+"F0.wireOp",EDGE,"E16.154.4"),sQuery(id+"F0.wireOp",EDGE,"E16.155.0"),sQuery(id+"F0.wireOp",EDGE,"E16.155.1"),sQuery(id+"F0.wireOp",EDGE,"E16.155.2"),sQuery(id+"F0.wireOp",EDGE,"E16.155.3"),sQuery(id+"F0.wireOp",EDGE,"E16.155.4"),sQuery(id+"F0.wireOp",EDGE,"E16.156.0"),sQuery(id+"F0.wireOp",EDGE,"E16.156.1"),sQuery(id+"F0.wireOp",EDGE,"E16.156.2"),sQuery(id+"F0.wireOp",EDGE,"E16.156.3"),sQuery(id+"F0.wireOp",EDGE,"E16.156.4"),sQuery(id+"F0.wireOp",EDGE,"E16.157.0"),sQuery(id+"F0.wireOp",EDGE,"E16.157.1"),sQuery(id+"F0.wireOp",EDGE,"E16.157.2"),sQuery(id+"F0.wireOp",EDGE,"E16.157.3"),sQuery(id+"F0.wireOp",EDGE,"E16.157.4"),sQuery(id+"F0.wireOp",EDGE,"E16.158.0"),sQuery(id+"F0.wireOp",EDGE,"E16.158.1"),sQuery(id+"F0.wireOp",EDGE,"E16.158.2"),sQuery(id+"F0.wireOp",EDGE,"E16.158.3"),sQuery(id+"F0.wireOp",EDGE,"E16.158.4"),sQuery(id+"F0.wireOp",EDGE,"E16.159.0"),sQuery(id+"F0.wireOp",EDGE,"E16.159.1"),sQuery(id+"F0.wireOp",EDGE,"E16.159.2"),sQuery(id+"F0.wireOp",EDGE,"E16.159.3"),sQuery(id+"F0.wireOp",EDGE,"E16.159.4"),sQuery(id+"F0.wireOp",EDGE,"E16.160.0"),sQuery(id+"F0.wireOp",EDGE,"E16.160.1"),sQuery(id+"F0.wireOp",EDGE,"E16.160.2"),sQuery(id+"F0.wireOp",EDGE,"E16.160.3"),sQuery(id+"F0.wireOp",EDGE,"E16.160.4"),sQuery(id+"F0.wireOp",EDGE,"E16.161.0"),sQuery(id+"F0.wireOp",EDGE,"E16.161.1"),sQuery(id+"F0.wireOp",EDGE,"E16.161.2"),sQuery(id+"F0.wireOp",EDGE,"E16.161.3"),sQuery(id+"F0.wireOp",EDGE,"E16.161.4"),sQuery(id+"F0.wireOp",EDGE,"E16.162.0"),sQuery(id+"F0.wireOp",EDGE,"E16.162.1"),sQuery(id+"F0.wireOp",EDGE,"E16.162.2"),sQuery(id+"F0.wireOp",EDGE,"E16.162.3"),sQuery(id+"F0.wireOp",EDGE,"E16.162.4"),sQuery(id+"F0.wireOp",EDGE,"E16.163.0"),sQuery(id+"F0.wireOp",EDGE,"E16.163.1"),sQuery(id+"F0.wireOp",EDGE,"E16.163.2"),sQuery(id+"F0.wireOp",EDGE,"E16.163.3"),sQuery(id+"F0.wireOp",EDGE,"E16.163.4"),sQuery(id+"F0.wireOp",EDGE,"E16.164.0"),sQuery(id+"F0.wireOp",EDGE,"E16.164.1"),sQuery(id+"F0.wireOp",EDGE,"E16.164.2"),sQuery(id+"F0.wireOp",EDGE,"E16.164.3"),sQuery(id+"F0.wireOp",EDGE,"E16.164.4"),sQuery(id+"F0.wireOp",EDGE,"E16.165.0"),sQuery(id+"F0.wireOp",EDGE,"E16.165.1"),sQuery(id+"F0.wireOp",EDGE,"E16.165.2"),sQuery(id+"F0.wireOp",EDGE,"E16.165.3"),sQuery(id+"F0.wireOp",EDGE,"E16.165.4"),sQuery(id+"F0.wireOp",EDGE,"E16.166.0"),sQuery(id+"F0.wireOp",EDGE,"E16.166.1"),sQuery(id+"F0.wireOp",EDGE,"E16.166.2"),sQuery(id+"F0.wireOp",EDGE,"E16.166.3"),sQuery(id+"F0.wireOp",EDGE,"E16.166.4"),sQuery(id+"F0.wireOp",EDGE,"E16.167.0"),sQuery(id+"F0.wireOp",EDGE,"E16.167.1"),sQuery(id+"F0.wireOp",EDGE,"E16.167.2"),sQuery(id+"F0.wireOp",EDGE,"E16.167.3"),sQuery(id+"F0.wireOp",EDGE,"E16.167.4"),sQuery(id+"F0.wireOp",EDGE,"E16.168.0"),sQuery(id+"F0.wireOp",EDGE,"E16.168.1"),sQuery(id+"F0.wireOp",EDGE,"E16.168.2"),sQuery(id+"F0.wireOp",EDGE,"E16.168.3"),sQuery(id+"F0.wireOp",EDGE,"E16.168.4"),sQuery(id+"F0.wireOp",EDGE,"E16.169.0"),sQuery(id+"F0.wireOp",EDGE,"E16.169.1"),sQuery(id+"F0.wireOp",EDGE,"E16.169.2"),sQuery(id+"F0.wireOp",EDGE,"E16.169.3"),sQuery(id+"F0.wireOp",EDGE,"E16.169.4"),sQuery(id+"F0.wireOp",EDGE,"E16.170.0"),sQuery(id+"F0.wireOp",EDGE,"E16.170.1"),sQuery(id+"F0.wireOp",EDGE,"E16.170.2"),sQuery(id+"F0.wireOp",EDGE,"E16.170.3"),sQuery(id+"F0.wireOp",EDGE,"E16.170.4"),sQuery(id+"F0.wireOp",EDGE,"E16.171.0"),sQuery(id+"F0.wireOp",EDGE,"E16.171.1"),sQuery(id+"F0.wireOp",EDGE,"E16.171.2"),sQuery(id+"F0.wireOp",EDGE,"E16.171.3"),sQuery(id+"F0.wireOp",EDGE,"E16.171.4"),sQuery(id+"F0.wireOp",EDGE,"E16.172.0"),sQuery(id+"F0.wireOp",EDGE,"E16.172.1"),sQuery(id+"F0.wireOp",EDGE,"E16.172.2"),sQuery(id+"F0.wireOp",EDGE,"E16.172.3"),sQuery(id+"F0.wireOp",EDGE,"E16.172.4"),sQuery(id+"F0.wireOp",EDGE,"E16.173.0"),sQuery(id+"F0.wireOp",EDGE,"E16.173.1"),sQuery(id+"F0.wireOp",EDGE,"E16.173.2"),sQuery(id+"F0.wireOp",EDGE,"E16.173.3"),sQuery(id+"F0.wireOp",EDGE,"E16.173.4"),sQuery(id+"F0.wireOp",EDGE,"E16.174.0"),sQuery(id+"F0.wireOp",EDGE,"E16.174.1"),sQuery(id+"F0.wireOp",EDGE,"E16.174.2"),sQuery(id+"F0.wireOp",EDGE,"E16.174.3"),sQuery(id+"F0.wireOp",EDGE,"E16.174.4"),sQuery(id+"F0.wireOp",EDGE,"E16.175.0"),sQuery(id+"F0.wireOp",EDGE,"E16.175.1"),sQuery(id+"F0.wireOp",EDGE,"E16.175.2"),sQuery(id+"F0.wireOp",EDGE,"E16.175.3"),sQuery(id+"F0.wireOp",EDGE,"E16.175.4"),sQuery(id+"F0.wireOp",EDGE,"E16.176.0"),sQuery(id+"F0.wireOp",EDGE,"E16.176.1"),sQuery(id+"F0.wireOp",EDGE,"E16.176.2"),sQuery(id+"F0.wireOp",EDGE,"E16.176.3"),sQuery(id+"F0.wireOp",EDGE,"E16.176.4"),sQuery(id+"F0.wireOp",EDGE,"E16.177.0"),sQuery(id+"F0.wireOp",EDGE,"E16.177.1"),sQuery(id+"F0.wireOp",EDGE,"E16.177.2"),sQuery(id+"F0.wireOp",EDGE,"E16.177.3"),sQuery(id+"F0.wireOp",EDGE,"E16.177.4"),sQuery(id+"F0.wireOp",EDGE,"E16.178.0"),sQuery(id+"F0.wireOp",EDGE,"E16.178.1"),sQuery(id+"F0.wireOp",EDGE,"E16.178.2"),sQuery(id+"F0.wireOp",EDGE,"E16.178.3"),sQuery(id+"F0.wireOp",EDGE,"E16.178.4"),sQuery(id+"F0.wireOp",EDGE,"E16.179.0"),sQuery(id+"F0.wireOp",EDGE,"E16.179.1"),sQuery(id+"F0.wireOp",EDGE,"E16.179.2"),sQuery(id+"F0.wireOp",EDGE,"E16.179.3"),sQuery(id+"F0.wireOp",EDGE,"E16.179.4"),sQuery(id+"F0.wireOp",EDGE,"E16.180.0"),sQuery(id+"F0.wireOp",EDGE,"E16.180.1"),sQuery(id+"F0.wireOp",EDGE,"E16.180.2"),sQuery(id+"F0.wireOp",EDGE,"E16.180.3"),sQuery(id+"F0.wireOp",EDGE,"E16.180.4"),sQuery(id+"F0.wireOp",EDGE,"E16.181.0"),sQuery(id+"F0.wireOp",EDGE,"E16.181.1"),sQuery(id+"F0.wireOp",EDGE,"E16.181.2"),sQuery(id+"F0.wireOp",EDGE,"E16.181.3"),sQuery(id+"F0.wireOp",EDGE,"E16.181.4"),sQuery(id+"F0.wireOp",EDGE,"E16.182.0"),sQuery(id+"F0.wireOp",EDGE,"E16.182.1"),sQuery(id+"F0.wireOp",EDGE,"E16.182.2"),sQuery(id+"F0.wireOp",EDGE,"E16.182.3"),sQuery(id+"F0.wireOp",EDGE,"E16.182.4"),sQuery(id+"F0.wireOp",EDGE,"E16.183.0"),sQuery(id+"F0.wireOp",EDGE,"E16.183.1"),sQuery(id+"F0.wireOp",EDGE,"E16.183.2"),sQuery(id+"F0.wireOp",EDGE,"E16.183.3"),sQuery(id+"F0.wireOp",EDGE,"E16.183.4"),sQuery(id+"F0.wireOp",EDGE,"E16.184.0"),sQuery(id+"F0.wireOp",EDGE,"E16.184.1"),sQuery(id+"F0.wireOp",EDGE,"E16.184.2"),sQuery(id+"F0.wireOp",EDGE,"E16.184.3"),sQuery(id+"F0.wireOp",EDGE,"E16.184.4"),sQuery(id+"F0.wireOp",EDGE,"E16.185.0"),sQuery(id+"F0.wireOp",EDGE,"E16.185.1"),sQuery(id+"F0.wireOp",EDGE,"E16.185.2"),sQuery(id+"F0.wireOp",EDGE,"E16.185.3"),sQuery(id+"F0.wireOp",EDGE,"E16.185.4"),sQuery(id+"F0.wireOp",EDGE,"E16.186.0"),sQuery(id+"F0.wireOp",EDGE,"E16.186.1"),sQuery(id+"F0.wireOp",EDGE,"E16.186.2"),sQuery(id+"F0.wireOp",EDGE,"E16.186.3"),sQuery(id+"F0.wireOp",EDGE,"E16.186.4"),sQuery(id+"F0.wireOp",EDGE,"E16.187.0"),sQuery(id+"F0.wireOp",EDGE,"E16.187.1"),sQuery(id+"F0.wireOp",EDGE,"E16.187.2"),sQuery(id+"F0.wireOp",EDGE,"E16.187.3"),sQuery(id+"F0.wireOp",EDGE,"E16.187.4"),sQuery(id+"F0.wireOp",EDGE,"E16.188.0"),sQuery(id+"F0.wireOp",EDGE,"E16.188.1"),sQuery(id+"F0.wireOp",EDGE,"E16.188.2"),sQuery(id+"F0.wireOp",EDGE,"E16.188.3"),sQuery(id+"F0.wireOp",EDGE,"E16.188.4"),sQuery(id+"F0.wireOp",EDGE,"E16.189.0"),sQuery(id+"F0.wireOp",EDGE,"E16.189.1"),sQuery(id+"F0.wireOp",EDGE,"E16.189.2"),sQuery(id+"F0.wireOp",EDGE,"E16.189.3"),sQuery(id+"F0.wireOp",EDGE,"E16.189.4"),sQuery(id+"F0.wireOp",EDGE,"E16.190.0"),sQuery(id+"F0.wireOp",EDGE,"E16.190.1"),sQuery(id+"F0.wireOp",EDGE,"E16.190.2"),sQuery(id+"F0.wireOp",EDGE,"E16.190.3"),sQuery(id+"F0.wireOp",EDGE,"E16.190.4"),sQuery(id+"F0.wireOp",EDGE,"E16.191.0"),sQuery(id+"F0.wireOp",EDGE,"E16.191.1"),sQuery(id+"F0.wireOp",EDGE,"E16.191.2"),sQuery(id+"F0.wireOp",EDGE,"E16.191.3"),sQuery(id+"F0.wireOp",EDGE,"E16.191.4")])],"isStart":true});
            var sketch = newSketch(context, id + "F2", { "sketchPlane" : qUnion([Q0])});
            skCircle(sketch, "E17", {"center": v(0, 0) * mm, "radius": 95 * mm, "construction": true});
            skLineSegment(sketch, "E18", {"start": v(0, 0) * mm, "end": v(113.24, 0) * mm, "construction": true});
            skPoint(sketch, "E19", {"position": v(95, 0) * mm});
            skPoint(sketch, "E20.1.0", {"position": v(82.27, 47.5) * mm});
            skPoint(sketch, "E20.2.0", {"position": v(47.5, 82.27) * mm});
            skPoint(sketch, "E20.3.0", {"position": v(0, 95) * mm});
            skPoint(sketch, "E20.4.0", {"position": v(-47.5, 82.27) * mm});
            skPoint(sketch, "E20.5.0", {"position": v(-82.27, 47.5) * mm});
            skPoint(sketch, "E20.6.0", {"position": v(-95, 0) * mm});
            skPoint(sketch, "E20.7.0", {"position": v(-82.27, -47.5) * mm});
            skPoint(sketch, "E20.8.0", {"position": v(-47.5, -82.27) * mm});
            skPoint(sketch, "E20.9.0", {"position": v(0, -95) * mm});
            skPoint(sketch, "E20.10.0", {"position": v(47.5, -82.27) * mm});
            skPoint(sketch, "E20.11.0", {"position": v(82.27, -47.5) * mm});
            skSolve(sketch);
        }
        {
            var Q0;
            Q0=makeQuery(id+"F1.opExtrude","CAP_FACE",FACE,{"disambiguationData":[OSD([sQuery(id+"F0.wireOp",EDGE,"E0"),sQuery(id+"F0.wireOp",EDGE,"E4"),sQuery(id+"F0.wireOp",EDGE,"E5"),sQuery(id+"F0.wireOp",EDGE,"E6.filletArc"),sQuery(id+"F0.wireOp",EDGE,"E7.MirrorCS"),sQuery(id+"F0.wireOp",EDGE,"E8.MirrorCS"),sQuery(id+"F0.wireOp",EDGE,"E15"),sQuery(id+"F0.wireOp",EDGE,"E16.1.0"),sQuery(id+"F0.wireOp",EDGE,"E16.1.1"),sQuery(id+"F0.wireOp",EDGE,"E16.1.2"),sQuery(id+"F0.wireOp",EDGE,"E16.1.3"),sQuery(id+"F0.wireOp",EDGE,"E16.1.4"),sQuery(id+"F0.wireOp",EDGE,"E16.2.0"),sQuery(id+"F0.wireOp",EDGE,"E16.2.1"),sQuery(id+"F0.wireOp",EDGE,"E16.2.2"),sQuery(id+"F0.wireOp",EDGE,"E16.2.3"),sQuery(id+"F0.wireOp",EDGE,"E16.2.4"),sQuery(id+"F0.wireOp",EDGE,"E16.3.0"),sQuery(id+"F0.wireOp",EDGE,"E16.3.1"),sQuery(id+"F0.wireOp",EDGE,"E16.3.2"),sQuery(id+"F0.wireOp",EDGE,"E16.3.3"),sQuery(id+"F0.wireOp",EDGE,"E16.3.4"),sQuery(id+"F0.wireOp",EDGE,"E16.4.0"),sQuery(id+"F0.wireOp",EDGE,"E16.4.1"),sQuery(id+"F0.wireOp",EDGE,"E16.4.2"),sQuery(id+"F0.wireOp",EDGE,"E16.4.3"),sQuery(id+"F0.wireOp",EDGE,"E16.4.4"),sQuery(id+"F0.wireOp",EDGE,"E16.5.0"),sQuery(id+"F0.wireOp",EDGE,"E16.5.1"),sQuery(id+"F0.wireOp",EDGE,"E16.5.2"),sQuery(id+"F0.wireOp",EDGE,"E16.5.3"),sQuery(id+"F0.wireOp",EDGE,"E16.5.4"),sQuery(id+"F0.wireOp",EDGE,"E16.6.0"),sQuery(id+"F0.wireOp",EDGE,"E16.6.1"),sQuery(id+"F0.wireOp",EDGE,"E16.6.2"),sQuery(id+"F0.wireOp",EDGE,"E16.6.3"),sQuery(id+"F0.wireOp",EDGE,"E16.6.4"),sQuery(id+"F0.wireOp",EDGE,"E16.7.0"),sQuery(id+"F0.wireOp",EDGE,"E16.7.1"),sQuery(id+"F0.wireOp",EDGE,"E16.7.2"),sQuery(id+"F0.wireOp",EDGE,"E16.7.3"),sQuery(id+"F0.wireOp",EDGE,"E16.7.4"),sQuery(id+"F0.wireOp",EDGE,"E16.8.0"),sQuery(id+"F0.wireOp",EDGE,"E16.8.1"),sQuery(id+"F0.wireOp",EDGE,"E16.8.2"),sQuery(id+"F0.wireOp",EDGE,"E16.8.3"),sQuery(id+"F0.wireOp",EDGE,"E16.8.4"),sQuery(id+"F0.wireOp",EDGE,"E16.9.0"),sQuery(id+"F0.wireOp",EDGE,"E16.9.1"),sQuery(id+"F0.wireOp",EDGE,"E16.9.2"),sQuery(id+"F0.wireOp",EDGE,"E16.9.3"),sQuery(id+"F0.wireOp",EDGE,"E16.9.4"),sQuery(id+"F0.wireOp",EDGE,"E16.10.0"),sQuery(id+"F0.wireOp",EDGE,"E16.10.1"),sQuery(id+"F0.wireOp",EDGE,"E16.10.2"),sQuery(id+"F0.wireOp",EDGE,"E16.10.3"),sQuery(id+"F0.wireOp",EDGE,"E16.10.4"),sQuery(id+"F0.wireOp",EDGE,"E16.11.0"),sQuery(id+"F0.wireOp",EDGE,"E16.11.1"),sQuery(id+"F0.wireOp",EDGE,"E16.11.2"),sQuery(id+"F0.wireOp",EDGE,"E16.11.3"),sQuery(id+"F0.wireOp",EDGE,"E16.11.4"),sQuery(id+"F0.wireOp",EDGE,"E16.12.0"),sQuery(id+"F0.wireOp",EDGE,"E16.12.1"),sQuery(id+"F0.wireOp",EDGE,"E16.12.2"),sQuery(id+"F0.wireOp",EDGE,"E16.12.3"),sQuery(id+"F0.wireOp",EDGE,"E16.12.4"),sQuery(id+"F0.wireOp",EDGE,"E16.13.0"),sQuery(id+"F0.wireOp",EDGE,"E16.13.1"),sQuery(id+"F0.wireOp",EDGE,"E16.13.2"),sQuery(id+"F0.wireOp",EDGE,"E16.13.3"),sQuery(id+"F0.wireOp",EDGE,"E16.13.4"),sQuery(id+"F0.wireOp",EDGE,"E16.14.0"),sQuery(id+"F0.wireOp",EDGE,"E16.14.1"),sQuery(id+"F0.wireOp",EDGE,"E16.14.2"),sQuery(id+"F0.wireOp",EDGE,"E16.14.3"),sQuery(id+"F0.wireOp",EDGE,"E16.14.4"),sQuery(id+"F0.wireOp",EDGE,"E16.15.0"),sQuery(id+"F0.wireOp",EDGE,"E16.15.1"),sQuery(id+"F0.wireOp",EDGE,"E16.15.2"),sQuery(id+"F0.wireOp",EDGE,"E16.15.3"),sQuery(id+"F0.wireOp",EDGE,"E16.15.4"),sQuery(id+"F0.wireOp",EDGE,"E16.16.0"),sQuery(id+"F0.wireOp",EDGE,"E16.16.1"),sQuery(id+"F0.wireOp",EDGE,"E16.16.2"),sQuery(id+"F0.wireOp",EDGE,"E16.16.3"),sQuery(id+"F0.wireOp",EDGE,"E16.16.4"),sQuery(id+"F0.wireOp",EDGE,"E16.17.0"),sQuery(id+"F0.wireOp",EDGE,"E16.17.1"),sQuery(id+"F0.wireOp",EDGE,"E16.17.2"),sQuery(id+"F0.wireOp",EDGE,"E16.17.3"),sQuery(id+"F0.wireOp",EDGE,"E16.17.4"),sQuery(id+"F0.wireOp",EDGE,"E16.18.0"),sQuery(id+"F0.wireOp",EDGE,"E16.18.1"),sQuery(id+"F0.wireOp",EDGE,"E16.18.2"),sQuery(id+"F0.wireOp",EDGE,"E16.18.3"),sQuery(id+"F0.wireOp",EDGE,"E16.18.4"),sQuery(id+"F0.wireOp",EDGE,"E16.19.0"),sQuery(id+"F0.wireOp",EDGE,"E16.19.1"),sQuery(id+"F0.wireOp",EDGE,"E16.19.2"),sQuery(id+"F0.wireOp",EDGE,"E16.19.3"),sQuery(id+"F0.wireOp",EDGE,"E16.19.4"),sQuery(id+"F0.wireOp",EDGE,"E16.20.0"),sQuery(id+"F0.wireOp",EDGE,"E16.20.1"),sQuery(id+"F0.wireOp",EDGE,"E16.20.2"),sQuery(id+"F0.wireOp",EDGE,"E16.20.3"),sQuery(id+"F0.wireOp",EDGE,"E16.20.4"),sQuery(id+"F0.wireOp",EDGE,"E16.21.0"),sQuery(id+"F0.wireOp",EDGE,"E16.21.1"),sQuery(id+"F0.wireOp",EDGE,"E16.21.2"),sQuery(id+"F0.wireOp",EDGE,"E16.21.3"),sQuery(id+"F0.wireOp",EDGE,"E16.21.4"),sQuery(id+"F0.wireOp",EDGE,"E16.22.0"),sQuery(id+"F0.wireOp",EDGE,"E16.22.1"),sQuery(id+"F0.wireOp",EDGE,"E16.22.2"),sQuery(id+"F0.wireOp",EDGE,"E16.22.3"),sQuery(id+"F0.wireOp",EDGE,"E16.22.4"),sQuery(id+"F0.wireOp",EDGE,"E16.23.0"),sQuery(id+"F0.wireOp",EDGE,"E16.23.1"),sQuery(id+"F0.wireOp",EDGE,"E16.23.2"),sQuery(id+"F0.wireOp",EDGE,"E16.23.3"),sQuery(id+"F0.wireOp",EDGE,"E16.23.4"),sQuery(id+"F0.wireOp",EDGE,"E16.24.0"),sQuery(id+"F0.wireOp",EDGE,"E16.24.1"),sQuery(id+"F0.wireOp",EDGE,"E16.24.2"),sQuery(id+"F0.wireOp",EDGE,"E16.24.3"),sQuery(id+"F0.wireOp",EDGE,"E16.24.4"),sQuery(id+"F0.wireOp",EDGE,"E16.25.0"),sQuery(id+"F0.wireOp",EDGE,"E16.25.1"),sQuery(id+"F0.wireOp",EDGE,"E16.25.2"),sQuery(id+"F0.wireOp",EDGE,"E16.25.3"),sQuery(id+"F0.wireOp",EDGE,"E16.25.4"),sQuery(id+"F0.wireOp",EDGE,"E16.26.0"),sQuery(id+"F0.wireOp",EDGE,"E16.26.1"),sQuery(id+"F0.wireOp",EDGE,"E16.26.2"),sQuery(id+"F0.wireOp",EDGE,"E16.26.3"),sQuery(id+"F0.wireOp",EDGE,"E16.26.4"),sQuery(id+"F0.wireOp",EDGE,"E16.27.0"),sQuery(id+"F0.wireOp",EDGE,"E16.27.1"),sQuery(id+"F0.wireOp",EDGE,"E16.27.2"),sQuery(id+"F0.wireOp",EDGE,"E16.27.3"),sQuery(id+"F0.wireOp",EDGE,"E16.27.4"),sQuery(id+"F0.wireOp",EDGE,"E16.28.0"),sQuery(id+"F0.wireOp",EDGE,"E16.28.1"),sQuery(id+"F0.wireOp",EDGE,"E16.28.2"),sQuery(id+"F0.wireOp",EDGE,"E16.28.3"),sQuery(id+"F0.wireOp",EDGE,"E16.28.4"),sQuery(id+"F0.wireOp",EDGE,"E16.29.0"),sQuery(id+"F0.wireOp",EDGE,"E16.29.1"),sQuery(id+"F0.wireOp",EDGE,"E16.29.2"),sQuery(id+"F0.wireOp",EDGE,"E16.29.3"),sQuery(id+"F0.wireOp",EDGE,"E16.29.4"),sQuery(id+"F0.wireOp",EDGE,"E16.30.0"),sQuery(id+"F0.wireOp",EDGE,"E16.30.1"),sQuery(id+"F0.wireOp",EDGE,"E16.30.2"),sQuery(id+"F0.wireOp",EDGE,"E16.30.3"),sQuery(id+"F0.wireOp",EDGE,"E16.30.4"),sQuery(id+"F0.wireOp",EDGE,"E16.31.0"),sQuery(id+"F0.wireOp",EDGE,"E16.31.1"),sQuery(id+"F0.wireOp",EDGE,"E16.31.2"),sQuery(id+"F0.wireOp",EDGE,"E16.31.3"),sQuery(id+"F0.wireOp",EDGE,"E16.31.4"),sQuery(id+"F0.wireOp",EDGE,"E16.32.0"),sQuery(id+"F0.wireOp",EDGE,"E16.32.1"),sQuery(id+"F0.wireOp",EDGE,"E16.32.2"),sQuery(id+"F0.wireOp",EDGE,"E16.32.3"),sQuery(id+"F0.wireOp",EDGE,"E16.32.4"),sQuery(id+"F0.wireOp",EDGE,"E16.33.0"),sQuery(id+"F0.wireOp",EDGE,"E16.33.1"),sQuery(id+"F0.wireOp",EDGE,"E16.33.2"),sQuery(id+"F0.wireOp",EDGE,"E16.33.3"),sQuery(id+"F0.wireOp",EDGE,"E16.33.4"),sQuery(id+"F0.wireOp",EDGE,"E16.34.0"),sQuery(id+"F0.wireOp",EDGE,"E16.34.1"),sQuery(id+"F0.wireOp",EDGE,"E16.34.2"),sQuery(id+"F0.wireOp",EDGE,"E16.34.3"),sQuery(id+"F0.wireOp",EDGE,"E16.34.4"),sQuery(id+"F0.wireOp",EDGE,"E16.35.0"),sQuery(id+"F0.wireOp",EDGE,"E16.35.1"),sQuery(id+"F0.wireOp",EDGE,"E16.35.2"),sQuery(id+"F0.wireOp",EDGE,"E16.35.3"),sQuery(id+"F0.wireOp",EDGE,"E16.35.4"),sQuery(id+"F0.wireOp",EDGE,"E16.36.0"),sQuery(id+"F0.wireOp",EDGE,"E16.36.1"),sQuery(id+"F0.wireOp",EDGE,"E16.36.2"),sQuery(id+"F0.wireOp",EDGE,"E16.36.3"),sQuery(id+"F0.wireOp",EDGE,"E16.36.4"),sQuery(id+"F0.wireOp",EDGE,"E16.37.0"),sQuery(id+"F0.wireOp",EDGE,"E16.37.1"),sQuery(id+"F0.wireOp",EDGE,"E16.37.2"),sQuery(id+"F0.wireOp",EDGE,"E16.37.3"),sQuery(id+"F0.wireOp",EDGE,"E16.37.4"),sQuery(id+"F0.wireOp",EDGE,"E16.38.0"),sQuery(id+"F0.wireOp",EDGE,"E16.38.1"),sQuery(id+"F0.wireOp",EDGE,"E16.38.2"),sQuery(id+"F0.wireOp",EDGE,"E16.38.3"),sQuery(id+"F0.wireOp",EDGE,"E16.38.4"),sQuery(id+"F0.wireOp",EDGE,"E16.39.0"),sQuery(id+"F0.wireOp",EDGE,"E16.39.1"),sQuery(id+"F0.wireOp",EDGE,"E16.39.2"),sQuery(id+"F0.wireOp",EDGE,"E16.39.3"),sQuery(id+"F0.wireOp",EDGE,"E16.39.4"),sQuery(id+"F0.wireOp",EDGE,"E16.40.0"),sQuery(id+"F0.wireOp",EDGE,"E16.40.1"),sQuery(id+"F0.wireOp",EDGE,"E16.40.2"),sQuery(id+"F0.wireOp",EDGE,"E16.40.3"),sQuery(id+"F0.wireOp",EDGE,"E16.40.4"),sQuery(id+"F0.wireOp",EDGE,"E16.41.0"),sQuery(id+"F0.wireOp",EDGE,"E16.41.1"),sQuery(id+"F0.wireOp",EDGE,"E16.41.2"),sQuery(id+"F0.wireOp",EDGE,"E16.41.3"),sQuery(id+"F0.wireOp",EDGE,"E16.41.4"),sQuery(id+"F0.wireOp",EDGE,"E16.42.0"),sQuery(id+"F0.wireOp",EDGE,"E16.42.1"),sQuery(id+"F0.wireOp",EDGE,"E16.42.2"),sQuery(id+"F0.wireOp",EDGE,"E16.42.3"),sQuery(id+"F0.wireOp",EDGE,"E16.42.4"),sQuery(id+"F0.wireOp",EDGE,"E16.43.0"),sQuery(id+"F0.wireOp",EDGE,"E16.43.1"),sQuery(id+"F0.wireOp",EDGE,"E16.43.2"),sQuery(id+"F0.wireOp",EDGE,"E16.43.3"),sQuery(id+"F0.wireOp",EDGE,"E16.43.4"),sQuery(id+"F0.wireOp",EDGE,"E16.44.0"),sQuery(id+"F0.wireOp",EDGE,"E16.44.1"),sQuery(id+"F0.wireOp",EDGE,"E16.44.2"),sQuery(id+"F0.wireOp",EDGE,"E16.44.3"),sQuery(id+"F0.wireOp",EDGE,"E16.44.4"),sQuery(id+"F0.wireOp",EDGE,"E16.45.0"),sQuery(id+"F0.wireOp",EDGE,"E16.45.1"),sQuery(id+"F0.wireOp",EDGE,"E16.45.2"),sQuery(id+"F0.wireOp",EDGE,"E16.45.3"),sQuery(id+"F0.wireOp",EDGE,"E16.45.4"),sQuery(id+"F0.wireOp",EDGE,"E16.46.0"),sQuery(id+"F0.wireOp",EDGE,"E16.46.1"),sQuery(id+"F0.wireOp",EDGE,"E16.46.2"),sQuery(id+"F0.wireOp",EDGE,"E16.46.3"),sQuery(id+"F0.wireOp",EDGE,"E16.46.4"),sQuery(id+"F0.wireOp",EDGE,"E16.47.0"),sQuery(id+"F0.wireOp",EDGE,"E16.47.1"),sQuery(id+"F0.wireOp",EDGE,"E16.47.2"),sQuery(id+"F0.wireOp",EDGE,"E16.47.3"),sQuery(id+"F0.wireOp",EDGE,"E16.47.4"),sQuery(id+"F0.wireOp",EDGE,"E16.48.0"),sQuery(id+"F0.wireOp",EDGE,"E16.48.1"),sQuery(id+"F0.wireOp",EDGE,"E16.48.2"),sQuery(id+"F0.wireOp",EDGE,"E16.48.3"),sQuery(id+"F0.wireOp",EDGE,"E16.48.4"),sQuery(id+"F0.wireOp",EDGE,"E16.49.0"),sQuery(id+"F0.wireOp",EDGE,"E16.49.1"),sQuery(id+"F0.wireOp",EDGE,"E16.49.2"),sQuery(id+"F0.wireOp",EDGE,"E16.49.3"),sQuery(id+"F0.wireOp",EDGE,"E16.49.4"),sQuery(id+"F0.wireOp",EDGE,"E16.50.0"),sQuery(id+"F0.wireOp",EDGE,"E16.50.1"),sQuery(id+"F0.wireOp",EDGE,"E16.50.2"),sQuery(id+"F0.wireOp",EDGE,"E16.50.3"),sQuery(id+"F0.wireOp",EDGE,"E16.50.4"),sQuery(id+"F0.wireOp",EDGE,"E16.51.0"),sQuery(id+"F0.wireOp",EDGE,"E16.51.1"),sQuery(id+"F0.wireOp",EDGE,"E16.51.2"),sQuery(id+"F0.wireOp",EDGE,"E16.51.3"),sQuery(id+"F0.wireOp",EDGE,"E16.51.4"),sQuery(id+"F0.wireOp",EDGE,"E16.52.0"),sQuery(id+"F0.wireOp",EDGE,"E16.52.1"),sQuery(id+"F0.wireOp",EDGE,"E16.52.2"),sQuery(id+"F0.wireOp",EDGE,"E16.52.3"),sQuery(id+"F0.wireOp",EDGE,"E16.52.4"),sQuery(id+"F0.wireOp",EDGE,"E16.53.0"),sQuery(id+"F0.wireOp",EDGE,"E16.53.1"),sQuery(id+"F0.wireOp",EDGE,"E16.53.2"),sQuery(id+"F0.wireOp",EDGE,"E16.53.3"),sQuery(id+"F0.wireOp",EDGE,"E16.53.4"),sQuery(id+"F0.wireOp",EDGE,"E16.54.0"),sQuery(id+"F0.wireOp",EDGE,"E16.54.1"),sQuery(id+"F0.wireOp",EDGE,"E16.54.2"),sQuery(id+"F0.wireOp",EDGE,"E16.54.3"),sQuery(id+"F0.wireOp",EDGE,"E16.54.4"),sQuery(id+"F0.wireOp",EDGE,"E16.55.0"),sQuery(id+"F0.wireOp",EDGE,"E16.55.1"),sQuery(id+"F0.wireOp",EDGE,"E16.55.2"),sQuery(id+"F0.wireOp",EDGE,"E16.55.3"),sQuery(id+"F0.wireOp",EDGE,"E16.55.4"),sQuery(id+"F0.wireOp",EDGE,"E16.56.0"),sQuery(id+"F0.wireOp",EDGE,"E16.56.1"),sQuery(id+"F0.wireOp",EDGE,"E16.56.2"),sQuery(id+"F0.wireOp",EDGE,"E16.56.3"),sQuery(id+"F0.wireOp",EDGE,"E16.56.4"),sQuery(id+"F0.wireOp",EDGE,"E16.57.0"),sQuery(id+"F0.wireOp",EDGE,"E16.57.1"),sQuery(id+"F0.wireOp",EDGE,"E16.57.2"),sQuery(id+"F0.wireOp",EDGE,"E16.57.3"),sQuery(id+"F0.wireOp",EDGE,"E16.57.4"),sQuery(id+"F0.wireOp",EDGE,"E16.58.0"),sQuery(id+"F0.wireOp",EDGE,"E16.58.1"),sQuery(id+"F0.wireOp",EDGE,"E16.58.2"),sQuery(id+"F0.wireOp",EDGE,"E16.58.3"),sQuery(id+"F0.wireOp",EDGE,"E16.58.4"),sQuery(id+"F0.wireOp",EDGE,"E16.59.0"),sQuery(id+"F0.wireOp",EDGE,"E16.59.1"),sQuery(id+"F0.wireOp",EDGE,"E16.59.2"),sQuery(id+"F0.wireOp",EDGE,"E16.59.3"),sQuery(id+"F0.wireOp",EDGE,"E16.59.4"),sQuery(id+"F0.wireOp",EDGE,"E16.60.0"),sQuery(id+"F0.wireOp",EDGE,"E16.60.1"),sQuery(id+"F0.wireOp",EDGE,"E16.60.2"),sQuery(id+"F0.wireOp",EDGE,"E16.60.3"),sQuery(id+"F0.wireOp",EDGE,"E16.60.4"),sQuery(id+"F0.wireOp",EDGE,"E16.61.0"),sQuery(id+"F0.wireOp",EDGE,"E16.61.1"),sQuery(id+"F0.wireOp",EDGE,"E16.61.2"),sQuery(id+"F0.wireOp",EDGE,"E16.61.3"),sQuery(id+"F0.wireOp",EDGE,"E16.61.4"),sQuery(id+"F0.wireOp",EDGE,"E16.62.0"),sQuery(id+"F0.wireOp",EDGE,"E16.62.1"),sQuery(id+"F0.wireOp",EDGE,"E16.62.2"),sQuery(id+"F0.wireOp",EDGE,"E16.62.3"),sQuery(id+"F0.wireOp",EDGE,"E16.62.4"),sQuery(id+"F0.wireOp",EDGE,"E16.63.0"),sQuery(id+"F0.wireOp",EDGE,"E16.63.1"),sQuery(id+"F0.wireOp",EDGE,"E16.63.2"),sQuery(id+"F0.wireOp",EDGE,"E16.63.3"),sQuery(id+"F0.wireOp",EDGE,"E16.63.4"),sQuery(id+"F0.wireOp",EDGE,"E16.64.0"),sQuery(id+"F0.wireOp",EDGE,"E16.64.1"),sQuery(id+"F0.wireOp",EDGE,"E16.64.2"),sQuery(id+"F0.wireOp",EDGE,"E16.64.3"),sQuery(id+"F0.wireOp",EDGE,"E16.64.4"),sQuery(id+"F0.wireOp",EDGE,"E16.65.0"),sQuery(id+"F0.wireOp",EDGE,"E16.65.1"),sQuery(id+"F0.wireOp",EDGE,"E16.65.2"),sQuery(id+"F0.wireOp",EDGE,"E16.65.3"),sQuery(id+"F0.wireOp",EDGE,"E16.65.4"),sQuery(id+"F0.wireOp",EDGE,"E16.66.0"),sQuery(id+"F0.wireOp",EDGE,"E16.66.1"),sQuery(id+"F0.wireOp",EDGE,"E16.66.2"),sQuery(id+"F0.wireOp",EDGE,"E16.66.3"),sQuery(id+"F0.wireOp",EDGE,"E16.66.4"),sQuery(id+"F0.wireOp",EDGE,"E16.67.0"),sQuery(id+"F0.wireOp",EDGE,"E16.67.1"),sQuery(id+"F0.wireOp",EDGE,"E16.67.2"),sQuery(id+"F0.wireOp",EDGE,"E16.67.3"),sQuery(id+"F0.wireOp",EDGE,"E16.67.4"),sQuery(id+"F0.wireOp",EDGE,"E16.68.0"),sQuery(id+"F0.wireOp",EDGE,"E16.68.1"),sQuery(id+"F0.wireOp",EDGE,"E16.68.2"),sQuery(id+"F0.wireOp",EDGE,"E16.68.3"),sQuery(id+"F0.wireOp",EDGE,"E16.68.4"),sQuery(id+"F0.wireOp",EDGE,"E16.69.0"),sQuery(id+"F0.wireOp",EDGE,"E16.69.1"),sQuery(id+"F0.wireOp",EDGE,"E16.69.2"),sQuery(id+"F0.wireOp",EDGE,"E16.69.3"),sQuery(id+"F0.wireOp",EDGE,"E16.69.4"),sQuery(id+"F0.wireOp",EDGE,"E16.70.0"),sQuery(id+"F0.wireOp",EDGE,"E16.70.1"),sQuery(id+"F0.wireOp",EDGE,"E16.70.2"),sQuery(id+"F0.wireOp",EDGE,"E16.70.3"),sQuery(id+"F0.wireOp",EDGE,"E16.70.4"),sQuery(id+"F0.wireOp",EDGE,"E16.71.0"),sQuery(id+"F0.wireOp",EDGE,"E16.71.1"),sQuery(id+"F0.wireOp",EDGE,"E16.71.2"),sQuery(id+"F0.wireOp",EDGE,"E16.71.3"),sQuery(id+"F0.wireOp",EDGE,"E16.71.4"),sQuery(id+"F0.wireOp",EDGE,"E16.72.0"),sQuery(id+"F0.wireOp",EDGE,"E16.72.1"),sQuery(id+"F0.wireOp",EDGE,"E16.72.2"),sQuery(id+"F0.wireOp",EDGE,"E16.72.3"),sQuery(id+"F0.wireOp",EDGE,"E16.72.4"),sQuery(id+"F0.wireOp",EDGE,"E16.73.0"),sQuery(id+"F0.wireOp",EDGE,"E16.73.1"),sQuery(id+"F0.wireOp",EDGE,"E16.73.2"),sQuery(id+"F0.wireOp",EDGE,"E16.73.3"),sQuery(id+"F0.wireOp",EDGE,"E16.73.4"),sQuery(id+"F0.wireOp",EDGE,"E16.74.0"),sQuery(id+"F0.wireOp",EDGE,"E16.74.1"),sQuery(id+"F0.wireOp",EDGE,"E16.74.2"),sQuery(id+"F0.wireOp",EDGE,"E16.74.3"),sQuery(id+"F0.wireOp",EDGE,"E16.74.4"),sQuery(id+"F0.wireOp",EDGE,"E16.75.0"),sQuery(id+"F0.wireOp",EDGE,"E16.75.1"),sQuery(id+"F0.wireOp",EDGE,"E16.75.2"),sQuery(id+"F0.wireOp",EDGE,"E16.75.3"),sQuery(id+"F0.wireOp",EDGE,"E16.75.4"),sQuery(id+"F0.wireOp",EDGE,"E16.76.0"),sQuery(id+"F0.wireOp",EDGE,"E16.76.1"),sQuery(id+"F0.wireOp",EDGE,"E16.76.2"),sQuery(id+"F0.wireOp",EDGE,"E16.76.3"),sQuery(id+"F0.wireOp",EDGE,"E16.76.4"),sQuery(id+"F0.wireOp",EDGE,"E16.77.0"),sQuery(id+"F0.wireOp",EDGE,"E16.77.1"),sQuery(id+"F0.wireOp",EDGE,"E16.77.2"),sQuery(id+"F0.wireOp",EDGE,"E16.77.3"),sQuery(id+"F0.wireOp",EDGE,"E16.77.4"),sQuery(id+"F0.wireOp",EDGE,"E16.78.0"),sQuery(id+"F0.wireOp",EDGE,"E16.78.1"),sQuery(id+"F0.wireOp",EDGE,"E16.78.2"),sQuery(id+"F0.wireOp",EDGE,"E16.78.3"),sQuery(id+"F0.wireOp",EDGE,"E16.78.4"),sQuery(id+"F0.wireOp",EDGE,"E16.79.0"),sQuery(id+"F0.wireOp",EDGE,"E16.79.1"),sQuery(id+"F0.wireOp",EDGE,"E16.79.2"),sQuery(id+"F0.wireOp",EDGE,"E16.79.3"),sQuery(id+"F0.wireOp",EDGE,"E16.79.4"),sQuery(id+"F0.wireOp",EDGE,"E16.80.0"),sQuery(id+"F0.wireOp",EDGE,"E16.80.1"),sQuery(id+"F0.wireOp",EDGE,"E16.80.2"),sQuery(id+"F0.wireOp",EDGE,"E16.80.3"),sQuery(id+"F0.wireOp",EDGE,"E16.80.4"),sQuery(id+"F0.wireOp",EDGE,"E16.81.0"),sQuery(id+"F0.wireOp",EDGE,"E16.81.1"),sQuery(id+"F0.wireOp",EDGE,"E16.81.2"),sQuery(id+"F0.wireOp",EDGE,"E16.81.3"),sQuery(id+"F0.wireOp",EDGE,"E16.81.4"),sQuery(id+"F0.wireOp",EDGE,"E16.82.0"),sQuery(id+"F0.wireOp",EDGE,"E16.82.1"),sQuery(id+"F0.wireOp",EDGE,"E16.82.2"),sQuery(id+"F0.wireOp",EDGE,"E16.82.3"),sQuery(id+"F0.wireOp",EDGE,"E16.82.4"),sQuery(id+"F0.wireOp",EDGE,"E16.83.0"),sQuery(id+"F0.wireOp",EDGE,"E16.83.1"),sQuery(id+"F0.wireOp",EDGE,"E16.83.2"),sQuery(id+"F0.wireOp",EDGE,"E16.83.3"),sQuery(id+"F0.wireOp",EDGE,"E16.83.4"),sQuery(id+"F0.wireOp",EDGE,"E16.84.0"),sQuery(id+"F0.wireOp",EDGE,"E16.84.1"),sQuery(id+"F0.wireOp",EDGE,"E16.84.2"),sQuery(id+"F0.wireOp",EDGE,"E16.84.3"),sQuery(id+"F0.wireOp",EDGE,"E16.84.4"),sQuery(id+"F0.wireOp",EDGE,"E16.85.0"),sQuery(id+"F0.wireOp",EDGE,"E16.85.1"),sQuery(id+"F0.wireOp",EDGE,"E16.85.2"),sQuery(id+"F0.wireOp",EDGE,"E16.85.3"),sQuery(id+"F0.wireOp",EDGE,"E16.85.4"),sQuery(id+"F0.wireOp",EDGE,"E16.86.0"),sQuery(id+"F0.wireOp",EDGE,"E16.86.1"),sQuery(id+"F0.wireOp",EDGE,"E16.86.2"),sQuery(id+"F0.wireOp",EDGE,"E16.86.3"),sQuery(id+"F0.wireOp",EDGE,"E16.86.4"),sQuery(id+"F0.wireOp",EDGE,"E16.87.0"),sQuery(id+"F0.wireOp",EDGE,"E16.87.1"),sQuery(id+"F0.wireOp",EDGE,"E16.87.2"),sQuery(id+"F0.wireOp",EDGE,"E16.87.3"),sQuery(id+"F0.wireOp",EDGE,"E16.87.4"),sQuery(id+"F0.wireOp",EDGE,"E16.88.0"),sQuery(id+"F0.wireOp",EDGE,"E16.88.1"),sQuery(id+"F0.wireOp",EDGE,"E16.88.2"),sQuery(id+"F0.wireOp",EDGE,"E16.88.3"),sQuery(id+"F0.wireOp",EDGE,"E16.88.4"),sQuery(id+"F0.wireOp",EDGE,"E16.89.0"),sQuery(id+"F0.wireOp",EDGE,"E16.89.1"),sQuery(id+"F0.wireOp",EDGE,"E16.89.2"),sQuery(id+"F0.wireOp",EDGE,"E16.89.3"),sQuery(id+"F0.wireOp",EDGE,"E16.89.4"),sQuery(id+"F0.wireOp",EDGE,"E16.90.0"),sQuery(id+"F0.wireOp",EDGE,"E16.90.1"),sQuery(id+"F0.wireOp",EDGE,"E16.90.2"),sQuery(id+"F0.wireOp",EDGE,"E16.90.3"),sQuery(id+"F0.wireOp",EDGE,"E16.90.4"),sQuery(id+"F0.wireOp",EDGE,"E16.91.0"),sQuery(id+"F0.wireOp",EDGE,"E16.91.1"),sQuery(id+"F0.wireOp",EDGE,"E16.91.2"),sQuery(id+"F0.wireOp",EDGE,"E16.91.3"),sQuery(id+"F0.wireOp",EDGE,"E16.91.4"),sQuery(id+"F0.wireOp",EDGE,"E16.92.0"),sQuery(id+"F0.wireOp",EDGE,"E16.92.1"),sQuery(id+"F0.wireOp",EDGE,"E16.92.2"),sQuery(id+"F0.wireOp",EDGE,"E16.92.3"),sQuery(id+"F0.wireOp",EDGE,"E16.92.4"),sQuery(id+"F0.wireOp",EDGE,"E16.93.0"),sQuery(id+"F0.wireOp",EDGE,"E16.93.1"),sQuery(id+"F0.wireOp",EDGE,"E16.93.2"),sQuery(id+"F0.wireOp",EDGE,"E16.93.3"),sQuery(id+"F0.wireOp",EDGE,"E16.93.4"),sQuery(id+"F0.wireOp",EDGE,"E16.94.0"),sQuery(id+"F0.wireOp",EDGE,"E16.94.1"),sQuery(id+"F0.wireOp",EDGE,"E16.94.2"),sQuery(id+"F0.wireOp",EDGE,"E16.94.3"),sQuery(id+"F0.wireOp",EDGE,"E16.94.4"),sQuery(id+"F0.wireOp",EDGE,"E16.95.0"),sQuery(id+"F0.wireOp",EDGE,"E16.95.1"),sQuery(id+"F0.wireOp",EDGE,"E16.95.2"),sQuery(id+"F0.wireOp",EDGE,"E16.95.3"),sQuery(id+"F0.wireOp",EDGE,"E16.95.4"),sQuery(id+"F0.wireOp",EDGE,"E16.96.0"),sQuery(id+"F0.wireOp",EDGE,"E16.96.1"),sQuery(id+"F0.wireOp",EDGE,"E16.96.2"),sQuery(id+"F0.wireOp",EDGE,"E16.96.3"),sQuery(id+"F0.wireOp",EDGE,"E16.96.4"),sQuery(id+"F0.wireOp",EDGE,"E16.97.0"),sQuery(id+"F0.wireOp",EDGE,"E16.97.1"),sQuery(id+"F0.wireOp",EDGE,"E16.97.2"),sQuery(id+"F0.wireOp",EDGE,"E16.97.3"),sQuery(id+"F0.wireOp",EDGE,"E16.97.4"),sQuery(id+"F0.wireOp",EDGE,"E16.98.0"),sQuery(id+"F0.wireOp",EDGE,"E16.98.1"),sQuery(id+"F0.wireOp",EDGE,"E16.98.2"),sQuery(id+"F0.wireOp",EDGE,"E16.98.3"),sQuery(id+"F0.wireOp",EDGE,"E16.98.4"),sQuery(id+"F0.wireOp",EDGE,"E16.99.0"),sQuery(id+"F0.wireOp",EDGE,"E16.99.1"),sQuery(id+"F0.wireOp",EDGE,"E16.99.2"),sQuery(id+"F0.wireOp",EDGE,"E16.99.3"),sQuery(id+"F0.wireOp",EDGE,"E16.99.4"),sQuery(id+"F0.wireOp",EDGE,"E16.100.0"),sQuery(id+"F0.wireOp",EDGE,"E16.100.1"),sQuery(id+"F0.wireOp",EDGE,"E16.100.2"),sQuery(id+"F0.wireOp",EDGE,"E16.100.3"),sQuery(id+"F0.wireOp",EDGE,"E16.100.4"),sQuery(id+"F0.wireOp",EDGE,"E16.101.0"),sQuery(id+"F0.wireOp",EDGE,"E16.101.1"),sQuery(id+"F0.wireOp",EDGE,"E16.101.2"),sQuery(id+"F0.wireOp",EDGE,"E16.101.3"),sQuery(id+"F0.wireOp",EDGE,"E16.101.4"),sQuery(id+"F0.wireOp",EDGE,"E16.102.0"),sQuery(id+"F0.wireOp",EDGE,"E16.102.1"),sQuery(id+"F0.wireOp",EDGE,"E16.102.2"),sQuery(id+"F0.wireOp",EDGE,"E16.102.3"),sQuery(id+"F0.wireOp",EDGE,"E16.102.4"),sQuery(id+"F0.wireOp",EDGE,"E16.103.0"),sQuery(id+"F0.wireOp",EDGE,"E16.103.1"),sQuery(id+"F0.wireOp",EDGE,"E16.103.2"),sQuery(id+"F0.wireOp",EDGE,"E16.103.3"),sQuery(id+"F0.wireOp",EDGE,"E16.103.4"),sQuery(id+"F0.wireOp",EDGE,"E16.104.0"),sQuery(id+"F0.wireOp",EDGE,"E16.104.1"),sQuery(id+"F0.wireOp",EDGE,"E16.104.2"),sQuery(id+"F0.wireOp",EDGE,"E16.104.3"),sQuery(id+"F0.wireOp",EDGE,"E16.104.4"),sQuery(id+"F0.wireOp",EDGE,"E16.105.0"),sQuery(id+"F0.wireOp",EDGE,"E16.105.1"),sQuery(id+"F0.wireOp",EDGE,"E16.105.2"),sQuery(id+"F0.wireOp",EDGE,"E16.105.3"),sQuery(id+"F0.wireOp",EDGE,"E16.105.4"),sQuery(id+"F0.wireOp",EDGE,"E16.106.0"),sQuery(id+"F0.wireOp",EDGE,"E16.106.1"),sQuery(id+"F0.wireOp",EDGE,"E16.106.2"),sQuery(id+"F0.wireOp",EDGE,"E16.106.3"),sQuery(id+"F0.wireOp",EDGE,"E16.106.4"),sQuery(id+"F0.wireOp",EDGE,"E16.107.0"),sQuery(id+"F0.wireOp",EDGE,"E16.107.1"),sQuery(id+"F0.wireOp",EDGE,"E16.107.2"),sQuery(id+"F0.wireOp",EDGE,"E16.107.3"),sQuery(id+"F0.wireOp",EDGE,"E16.107.4"),sQuery(id+"F0.wireOp",EDGE,"E16.108.0"),sQuery(id+"F0.wireOp",EDGE,"E16.108.1"),sQuery(id+"F0.wireOp",EDGE,"E16.108.2"),sQuery(id+"F0.wireOp",EDGE,"E16.108.3"),sQuery(id+"F0.wireOp",EDGE,"E16.108.4"),sQuery(id+"F0.wireOp",EDGE,"E16.109.0"),sQuery(id+"F0.wireOp",EDGE,"E16.109.1"),sQuery(id+"F0.wireOp",EDGE,"E16.109.2"),sQuery(id+"F0.wireOp",EDGE,"E16.109.3"),sQuery(id+"F0.wireOp",EDGE,"E16.109.4"),sQuery(id+"F0.wireOp",EDGE,"E16.110.0"),sQuery(id+"F0.wireOp",EDGE,"E16.110.1"),sQuery(id+"F0.wireOp",EDGE,"E16.110.2"),sQuery(id+"F0.wireOp",EDGE,"E16.110.3"),sQuery(id+"F0.wireOp",EDGE,"E16.110.4"),sQuery(id+"F0.wireOp",EDGE,"E16.111.0"),sQuery(id+"F0.wireOp",EDGE,"E16.111.1"),sQuery(id+"F0.wireOp",EDGE,"E16.111.2"),sQuery(id+"F0.wireOp",EDGE,"E16.111.3"),sQuery(id+"F0.wireOp",EDGE,"E16.111.4"),sQuery(id+"F0.wireOp",EDGE,"E16.112.0"),sQuery(id+"F0.wireOp",EDGE,"E16.112.1"),sQuery(id+"F0.wireOp",EDGE,"E16.112.2"),sQuery(id+"F0.wireOp",EDGE,"E16.112.3"),sQuery(id+"F0.wireOp",EDGE,"E16.112.4"),sQuery(id+"F0.wireOp",EDGE,"E16.113.0"),sQuery(id+"F0.wireOp",EDGE,"E16.113.1"),sQuery(id+"F0.wireOp",EDGE,"E16.113.2"),sQuery(id+"F0.wireOp",EDGE,"E16.113.3"),sQuery(id+"F0.wireOp",EDGE,"E16.113.4"),sQuery(id+"F0.wireOp",EDGE,"E16.114.0"),sQuery(id+"F0.wireOp",EDGE,"E16.114.1"),sQuery(id+"F0.wireOp",EDGE,"E16.114.2"),sQuery(id+"F0.wireOp",EDGE,"E16.114.3"),sQuery(id+"F0.wireOp",EDGE,"E16.114.4"),sQuery(id+"F0.wireOp",EDGE,"E16.115.0"),sQuery(id+"F0.wireOp",EDGE,"E16.115.1"),sQuery(id+"F0.wireOp",EDGE,"E16.115.2"),sQuery(id+"F0.wireOp",EDGE,"E16.115.3"),sQuery(id+"F0.wireOp",EDGE,"E16.115.4"),sQuery(id+"F0.wireOp",EDGE,"E16.116.0"),sQuery(id+"F0.wireOp",EDGE,"E16.116.1"),sQuery(id+"F0.wireOp",EDGE,"E16.116.2"),sQuery(id+"F0.wireOp",EDGE,"E16.116.3"),sQuery(id+"F0.wireOp",EDGE,"E16.116.4"),sQuery(id+"F0.wireOp",EDGE,"E16.117.0"),sQuery(id+"F0.wireOp",EDGE,"E16.117.1"),sQuery(id+"F0.wireOp",EDGE,"E16.117.2"),sQuery(id+"F0.wireOp",EDGE,"E16.117.3"),sQuery(id+"F0.wireOp",EDGE,"E16.117.4"),sQuery(id+"F0.wireOp",EDGE,"E16.118.0"),sQuery(id+"F0.wireOp",EDGE,"E16.118.1"),sQuery(id+"F0.wireOp",EDGE,"E16.118.2"),sQuery(id+"F0.wireOp",EDGE,"E16.118.3"),sQuery(id+"F0.wireOp",EDGE,"E16.118.4"),sQuery(id+"F0.wireOp",EDGE,"E16.119.0"),sQuery(id+"F0.wireOp",EDGE,"E16.119.1"),sQuery(id+"F0.wireOp",EDGE,"E16.119.2"),sQuery(id+"F0.wireOp",EDGE,"E16.119.3"),sQuery(id+"F0.wireOp",EDGE,"E16.119.4"),sQuery(id+"F0.wireOp",EDGE,"E16.120.0"),sQuery(id+"F0.wireOp",EDGE,"E16.120.1"),sQuery(id+"F0.wireOp",EDGE,"E16.120.2"),sQuery(id+"F0.wireOp",EDGE,"E16.120.3"),sQuery(id+"F0.wireOp",EDGE,"E16.120.4"),sQuery(id+"F0.wireOp",EDGE,"E16.121.0"),sQuery(id+"F0.wireOp",EDGE,"E16.121.1"),sQuery(id+"F0.wireOp",EDGE,"E16.121.2"),sQuery(id+"F0.wireOp",EDGE,"E16.121.3"),sQuery(id+"F0.wireOp",EDGE,"E16.121.4"),sQuery(id+"F0.wireOp",EDGE,"E16.122.0"),sQuery(id+"F0.wireOp",EDGE,"E16.122.1"),sQuery(id+"F0.wireOp",EDGE,"E16.122.2"),sQuery(id+"F0.wireOp",EDGE,"E16.122.3"),sQuery(id+"F0.wireOp",EDGE,"E16.122.4"),sQuery(id+"F0.wireOp",EDGE,"E16.123.0"),sQuery(id+"F0.wireOp",EDGE,"E16.123.1"),sQuery(id+"F0.wireOp",EDGE,"E16.123.2"),sQuery(id+"F0.wireOp",EDGE,"E16.123.3"),sQuery(id+"F0.wireOp",EDGE,"E16.123.4"),sQuery(id+"F0.wireOp",EDGE,"E16.124.0"),sQuery(id+"F0.wireOp",EDGE,"E16.124.1"),sQuery(id+"F0.wireOp",EDGE,"E16.124.2"),sQuery(id+"F0.wireOp",EDGE,"E16.124.3"),sQuery(id+"F0.wireOp",EDGE,"E16.124.4"),sQuery(id+"F0.wireOp",EDGE,"E16.125.0"),sQuery(id+"F0.wireOp",EDGE,"E16.125.1"),sQuery(id+"F0.wireOp",EDGE,"E16.125.2"),sQuery(id+"F0.wireOp",EDGE,"E16.125.3"),sQuery(id+"F0.wireOp",EDGE,"E16.125.4"),sQuery(id+"F0.wireOp",EDGE,"E16.126.0"),sQuery(id+"F0.wireOp",EDGE,"E16.126.1"),sQuery(id+"F0.wireOp",EDGE,"E16.126.2"),sQuery(id+"F0.wireOp",EDGE,"E16.126.3"),sQuery(id+"F0.wireOp",EDGE,"E16.126.4"),sQuery(id+"F0.wireOp",EDGE,"E16.127.0"),sQuery(id+"F0.wireOp",EDGE,"E16.127.1"),sQuery(id+"F0.wireOp",EDGE,"E16.127.2"),sQuery(id+"F0.wireOp",EDGE,"E16.127.3"),sQuery(id+"F0.wireOp",EDGE,"E16.127.4"),sQuery(id+"F0.wireOp",EDGE,"E16.128.0"),sQuery(id+"F0.wireOp",EDGE,"E16.128.1"),sQuery(id+"F0.wireOp",EDGE,"E16.128.2"),sQuery(id+"F0.wireOp",EDGE,"E16.128.3"),sQuery(id+"F0.wireOp",EDGE,"E16.128.4"),sQuery(id+"F0.wireOp",EDGE,"E16.129.0"),sQuery(id+"F0.wireOp",EDGE,"E16.129.1"),sQuery(id+"F0.wireOp",EDGE,"E16.129.2"),sQuery(id+"F0.wireOp",EDGE,"E16.129.3"),sQuery(id+"F0.wireOp",EDGE,"E16.129.4"),sQuery(id+"F0.wireOp",EDGE,"E16.130.0"),sQuery(id+"F0.wireOp",EDGE,"E16.130.1"),sQuery(id+"F0.wireOp",EDGE,"E16.130.2"),sQuery(id+"F0.wireOp",EDGE,"E16.130.3"),sQuery(id+"F0.wireOp",EDGE,"E16.130.4"),sQuery(id+"F0.wireOp",EDGE,"E16.131.0"),sQuery(id+"F0.wireOp",EDGE,"E16.131.1"),sQuery(id+"F0.wireOp",EDGE,"E16.131.2"),sQuery(id+"F0.wireOp",EDGE,"E16.131.3"),sQuery(id+"F0.wireOp",EDGE,"E16.131.4"),sQuery(id+"F0.wireOp",EDGE,"E16.132.0"),sQuery(id+"F0.wireOp",EDGE,"E16.132.1"),sQuery(id+"F0.wireOp",EDGE,"E16.132.2"),sQuery(id+"F0.wireOp",EDGE,"E16.132.3"),sQuery(id+"F0.wireOp",EDGE,"E16.132.4"),sQuery(id+"F0.wireOp",EDGE,"E16.133.0"),sQuery(id+"F0.wireOp",EDGE,"E16.133.1"),sQuery(id+"F0.wireOp",EDGE,"E16.133.2"),sQuery(id+"F0.wireOp",EDGE,"E16.133.3"),sQuery(id+"F0.wireOp",EDGE,"E16.133.4"),sQuery(id+"F0.wireOp",EDGE,"E16.134.0"),sQuery(id+"F0.wireOp",EDGE,"E16.134.1"),sQuery(id+"F0.wireOp",EDGE,"E16.134.2"),sQuery(id+"F0.wireOp",EDGE,"E16.134.3"),sQuery(id+"F0.wireOp",EDGE,"E16.134.4"),sQuery(id+"F0.wireOp",EDGE,"E16.135.0"),sQuery(id+"F0.wireOp",EDGE,"E16.135.1"),sQuery(id+"F0.wireOp",EDGE,"E16.135.2"),sQuery(id+"F0.wireOp",EDGE,"E16.135.3"),sQuery(id+"F0.wireOp",EDGE,"E16.135.4"),sQuery(id+"F0.wireOp",EDGE,"E16.136.0"),sQuery(id+"F0.wireOp",EDGE,"E16.136.1"),sQuery(id+"F0.wireOp",EDGE,"E16.136.2"),sQuery(id+"F0.wireOp",EDGE,"E16.136.3"),sQuery(id+"F0.wireOp",EDGE,"E16.136.4"),sQuery(id+"F0.wireOp",EDGE,"E16.137.0"),sQuery(id+"F0.wireOp",EDGE,"E16.137.1"),sQuery(id+"F0.wireOp",EDGE,"E16.137.2"),sQuery(id+"F0.wireOp",EDGE,"E16.137.3"),sQuery(id+"F0.wireOp",EDGE,"E16.137.4"),sQuery(id+"F0.wireOp",EDGE,"E16.138.0"),sQuery(id+"F0.wireOp",EDGE,"E16.138.1"),sQuery(id+"F0.wireOp",EDGE,"E16.138.2"),sQuery(id+"F0.wireOp",EDGE,"E16.138.3"),sQuery(id+"F0.wireOp",EDGE,"E16.138.4"),sQuery(id+"F0.wireOp",EDGE,"E16.139.0"),sQuery(id+"F0.wireOp",EDGE,"E16.139.1"),sQuery(id+"F0.wireOp",EDGE,"E16.139.2"),sQuery(id+"F0.wireOp",EDGE,"E16.139.3"),sQuery(id+"F0.wireOp",EDGE,"E16.139.4"),sQuery(id+"F0.wireOp",EDGE,"E16.140.0"),sQuery(id+"F0.wireOp",EDGE,"E16.140.1"),sQuery(id+"F0.wireOp",EDGE,"E16.140.2"),sQuery(id+"F0.wireOp",EDGE,"E16.140.3"),sQuery(id+"F0.wireOp",EDGE,"E16.140.4"),sQuery(id+"F0.wireOp",EDGE,"E16.141.0"),sQuery(id+"F0.wireOp",EDGE,"E16.141.1"),sQuery(id+"F0.wireOp",EDGE,"E16.141.2"),sQuery(id+"F0.wireOp",EDGE,"E16.141.3"),sQuery(id+"F0.wireOp",EDGE,"E16.141.4"),sQuery(id+"F0.wireOp",EDGE,"E16.142.0"),sQuery(id+"F0.wireOp",EDGE,"E16.142.1"),sQuery(id+"F0.wireOp",EDGE,"E16.142.2"),sQuery(id+"F0.wireOp",EDGE,"E16.142.3"),sQuery(id+"F0.wireOp",EDGE,"E16.142.4"),sQuery(id+"F0.wireOp",EDGE,"E16.143.0"),sQuery(id+"F0.wireOp",EDGE,"E16.143.1"),sQuery(id+"F0.wireOp",EDGE,"E16.143.2"),sQuery(id+"F0.wireOp",EDGE,"E16.143.3"),sQuery(id+"F0.wireOp",EDGE,"E16.143.4"),sQuery(id+"F0.wireOp",EDGE,"E16.144.0"),sQuery(id+"F0.wireOp",EDGE,"E16.144.1"),sQuery(id+"F0.wireOp",EDGE,"E16.144.2"),sQuery(id+"F0.wireOp",EDGE,"E16.144.3"),sQuery(id+"F0.wireOp",EDGE,"E16.144.4"),sQuery(id+"F0.wireOp",EDGE,"E16.145.0"),sQuery(id+"F0.wireOp",EDGE,"E16.145.1"),sQuery(id+"F0.wireOp",EDGE,"E16.145.2"),sQuery(id+"F0.wireOp",EDGE,"E16.145.3"),sQuery(id+"F0.wireOp",EDGE,"E16.145.4"),sQuery(id+"F0.wireOp",EDGE,"E16.146.0"),sQuery(id+"F0.wireOp",EDGE,"E16.146.1"),sQuery(id+"F0.wireOp",EDGE,"E16.146.2"),sQuery(id+"F0.wireOp",EDGE,"E16.146.3"),sQuery(id+"F0.wireOp",EDGE,"E16.146.4"),sQuery(id+"F0.wireOp",EDGE,"E16.147.0"),sQuery(id+"F0.wireOp",EDGE,"E16.147.1"),sQuery(id+"F0.wireOp",EDGE,"E16.147.2"),sQuery(id+"F0.wireOp",EDGE,"E16.147.3"),sQuery(id+"F0.wireOp",EDGE,"E16.147.4"),sQuery(id+"F0.wireOp",EDGE,"E16.148.0"),sQuery(id+"F0.wireOp",EDGE,"E16.148.1"),sQuery(id+"F0.wireOp",EDGE,"E16.148.2"),sQuery(id+"F0.wireOp",EDGE,"E16.148.3"),sQuery(id+"F0.wireOp",EDGE,"E16.148.4"),sQuery(id+"F0.wireOp",EDGE,"E16.149.0"),sQuery(id+"F0.wireOp",EDGE,"E16.149.1"),sQuery(id+"F0.wireOp",EDGE,"E16.149.2"),sQuery(id+"F0.wireOp",EDGE,"E16.149.3"),sQuery(id+"F0.wireOp",EDGE,"E16.149.4"),sQuery(id+"F0.wireOp",EDGE,"E16.150.0"),sQuery(id+"F0.wireOp",EDGE,"E16.150.1"),sQuery(id+"F0.wireOp",EDGE,"E16.150.2"),sQuery(id+"F0.wireOp",EDGE,"E16.150.3"),sQuery(id+"F0.wireOp",EDGE,"E16.150.4"),sQuery(id+"F0.wireOp",EDGE,"E16.151.0"),sQuery(id+"F0.wireOp",EDGE,"E16.151.1"),sQuery(id+"F0.wireOp",EDGE,"E16.151.2"),sQuery(id+"F0.wireOp",EDGE,"E16.151.3"),sQuery(id+"F0.wireOp",EDGE,"E16.151.4"),sQuery(id+"F0.wireOp",EDGE,"E16.152.0"),sQuery(id+"F0.wireOp",EDGE,"E16.152.1"),sQuery(id+"F0.wireOp",EDGE,"E16.152.2"),sQuery(id+"F0.wireOp",EDGE,"E16.152.3"),sQuery(id+"F0.wireOp",EDGE,"E16.152.4"),sQuery(id+"F0.wireOp",EDGE,"E16.153.0"),sQuery(id+"F0.wireOp",EDGE,"E16.153.1"),sQuery(id+"F0.wireOp",EDGE,"E16.153.2"),sQuery(id+"F0.wireOp",EDGE,"E16.153.3"),sQuery(id+"F0.wireOp",EDGE,"E16.153.4"),sQuery(id+"F0.wireOp",EDGE,"E16.154.0"),sQuery(id+"F0.wireOp",EDGE,"E16.154.1"),sQuery(id+"F0.wireOp",EDGE,"E16.154.2"),sQuery(id+"F0.wireOp",EDGE,"E16.154.3"),sQuery(id+"F0.wireOp",EDGE,"E16.154.4"),sQuery(id+"F0.wireOp",EDGE,"E16.155.0"),sQuery(id+"F0.wireOp",EDGE,"E16.155.1"),sQuery(id+"F0.wireOp",EDGE,"E16.155.2"),sQuery(id+"F0.wireOp",EDGE,"E16.155.3"),sQuery(id+"F0.wireOp",EDGE,"E16.155.4"),sQuery(id+"F0.wireOp",EDGE,"E16.156.0"),sQuery(id+"F0.wireOp",EDGE,"E16.156.1"),sQuery(id+"F0.wireOp",EDGE,"E16.156.2"),sQuery(id+"F0.wireOp",EDGE,"E16.156.3"),sQuery(id+"F0.wireOp",EDGE,"E16.156.4"),sQuery(id+"F0.wireOp",EDGE,"E16.157.0"),sQuery(id+"F0.wireOp",EDGE,"E16.157.1"),sQuery(id+"F0.wireOp",EDGE,"E16.157.2"),sQuery(id+"F0.wireOp",EDGE,"E16.157.3"),sQuery(id+"F0.wireOp",EDGE,"E16.157.4"),sQuery(id+"F0.wireOp",EDGE,"E16.158.0"),sQuery(id+"F0.wireOp",EDGE,"E16.158.1"),sQuery(id+"F0.wireOp",EDGE,"E16.158.2"),sQuery(id+"F0.wireOp",EDGE,"E16.158.3"),sQuery(id+"F0.wireOp",EDGE,"E16.158.4"),sQuery(id+"F0.wireOp",EDGE,"E16.159.0"),sQuery(id+"F0.wireOp",EDGE,"E16.159.1"),sQuery(id+"F0.wireOp",EDGE,"E16.159.2"),sQuery(id+"F0.wireOp",EDGE,"E16.159.3"),sQuery(id+"F0.wireOp",EDGE,"E16.159.4"),sQuery(id+"F0.wireOp",EDGE,"E16.160.0"),sQuery(id+"F0.wireOp",EDGE,"E16.160.1"),sQuery(id+"F0.wireOp",EDGE,"E16.160.2"),sQuery(id+"F0.wireOp",EDGE,"E16.160.3"),sQuery(id+"F0.wireOp",EDGE,"E16.160.4"),sQuery(id+"F0.wireOp",EDGE,"E16.161.0"),sQuery(id+"F0.wireOp",EDGE,"E16.161.1"),sQuery(id+"F0.wireOp",EDGE,"E16.161.2"),sQuery(id+"F0.wireOp",EDGE,"E16.161.3"),sQuery(id+"F0.wireOp",EDGE,"E16.161.4"),sQuery(id+"F0.wireOp",EDGE,"E16.162.0"),sQuery(id+"F0.wireOp",EDGE,"E16.162.1"),sQuery(id+"F0.wireOp",EDGE,"E16.162.2"),sQuery(id+"F0.wireOp",EDGE,"E16.162.3"),sQuery(id+"F0.wireOp",EDGE,"E16.162.4"),sQuery(id+"F0.wireOp",EDGE,"E16.163.0"),sQuery(id+"F0.wireOp",EDGE,"E16.163.1"),sQuery(id+"F0.wireOp",EDGE,"E16.163.2"),sQuery(id+"F0.wireOp",EDGE,"E16.163.3"),sQuery(id+"F0.wireOp",EDGE,"E16.163.4"),sQuery(id+"F0.wireOp",EDGE,"E16.164.0"),sQuery(id+"F0.wireOp",EDGE,"E16.164.1"),sQuery(id+"F0.wireOp",EDGE,"E16.164.2"),sQuery(id+"F0.wireOp",EDGE,"E16.164.3"),sQuery(id+"F0.wireOp",EDGE,"E16.164.4"),sQuery(id+"F0.wireOp",EDGE,"E16.165.0"),sQuery(id+"F0.wireOp",EDGE,"E16.165.1"),sQuery(id+"F0.wireOp",EDGE,"E16.165.2"),sQuery(id+"F0.wireOp",EDGE,"E16.165.3"),sQuery(id+"F0.wireOp",EDGE,"E16.165.4"),sQuery(id+"F0.wireOp",EDGE,"E16.166.0"),sQuery(id+"F0.wireOp",EDGE,"E16.166.1"),sQuery(id+"F0.wireOp",EDGE,"E16.166.2"),sQuery(id+"F0.wireOp",EDGE,"E16.166.3"),sQuery(id+"F0.wireOp",EDGE,"E16.166.4"),sQuery(id+"F0.wireOp",EDGE,"E16.167.0"),sQuery(id+"F0.wireOp",EDGE,"E16.167.1"),sQuery(id+"F0.wireOp",EDGE,"E16.167.2"),sQuery(id+"F0.wireOp",EDGE,"E16.167.3"),sQuery(id+"F0.wireOp",EDGE,"E16.167.4"),sQuery(id+"F0.wireOp",EDGE,"E16.168.0"),sQuery(id+"F0.wireOp",EDGE,"E16.168.1"),sQuery(id+"F0.wireOp",EDGE,"E16.168.2"),sQuery(id+"F0.wireOp",EDGE,"E16.168.3"),sQuery(id+"F0.wireOp",EDGE,"E16.168.4"),sQuery(id+"F0.wireOp",EDGE,"E16.169.0"),sQuery(id+"F0.wireOp",EDGE,"E16.169.1"),sQuery(id+"F0.wireOp",EDGE,"E16.169.2"),sQuery(id+"F0.wireOp",EDGE,"E16.169.3"),sQuery(id+"F0.wireOp",EDGE,"E16.169.4"),sQuery(id+"F0.wireOp",EDGE,"E16.170.0"),sQuery(id+"F0.wireOp",EDGE,"E16.170.1"),sQuery(id+"F0.wireOp",EDGE,"E16.170.2"),sQuery(id+"F0.wireOp",EDGE,"E16.170.3"),sQuery(id+"F0.wireOp",EDGE,"E16.170.4"),sQuery(id+"F0.wireOp",EDGE,"E16.171.0"),sQuery(id+"F0.wireOp",EDGE,"E16.171.1"),sQuery(id+"F0.wireOp",EDGE,"E16.171.2"),sQuery(id+"F0.wireOp",EDGE,"E16.171.3"),sQuery(id+"F0.wireOp",EDGE,"E16.171.4"),sQuery(id+"F0.wireOp",EDGE,"E16.172.0"),sQuery(id+"F0.wireOp",EDGE,"E16.172.1"),sQuery(id+"F0.wireOp",EDGE,"E16.172.2"),sQuery(id+"F0.wireOp",EDGE,"E16.172.3"),sQuery(id+"F0.wireOp",EDGE,"E16.172.4"),sQuery(id+"F0.wireOp",EDGE,"E16.173.0"),sQuery(id+"F0.wireOp",EDGE,"E16.173.1"),sQuery(id+"F0.wireOp",EDGE,"E16.173.2"),sQuery(id+"F0.wireOp",EDGE,"E16.173.3"),sQuery(id+"F0.wireOp",EDGE,"E16.173.4"),sQuery(id+"F0.wireOp",EDGE,"E16.174.0"),sQuery(id+"F0.wireOp",EDGE,"E16.174.1"),sQuery(id+"F0.wireOp",EDGE,"E16.174.2"),sQuery(id+"F0.wireOp",EDGE,"E16.174.3"),sQuery(id+"F0.wireOp",EDGE,"E16.174.4"),sQuery(id+"F0.wireOp",EDGE,"E16.175.0"),sQuery(id+"F0.wireOp",EDGE,"E16.175.1"),sQuery(id+"F0.wireOp",EDGE,"E16.175.2"),sQuery(id+"F0.wireOp",EDGE,"E16.175.3"),sQuery(id+"F0.wireOp",EDGE,"E16.175.4"),sQuery(id+"F0.wireOp",EDGE,"E16.176.0"),sQuery(id+"F0.wireOp",EDGE,"E16.176.1"),sQuery(id+"F0.wireOp",EDGE,"E16.176.2"),sQuery(id+"F0.wireOp",EDGE,"E16.176.3"),sQuery(id+"F0.wireOp",EDGE,"E16.176.4"),sQuery(id+"F0.wireOp",EDGE,"E16.177.0"),sQuery(id+"F0.wireOp",EDGE,"E16.177.1"),sQuery(id+"F0.wireOp",EDGE,"E16.177.2"),sQuery(id+"F0.wireOp",EDGE,"E16.177.3"),sQuery(id+"F0.wireOp",EDGE,"E16.177.4"),sQuery(id+"F0.wireOp",EDGE,"E16.178.0"),sQuery(id+"F0.wireOp",EDGE,"E16.178.1"),sQuery(id+"F0.wireOp",EDGE,"E16.178.2"),sQuery(id+"F0.wireOp",EDGE,"E16.178.3"),sQuery(id+"F0.wireOp",EDGE,"E16.178.4"),sQuery(id+"F0.wireOp",EDGE,"E16.179.0"),sQuery(id+"F0.wireOp",EDGE,"E16.179.1"),sQuery(id+"F0.wireOp",EDGE,"E16.179.2"),sQuery(id+"F0.wireOp",EDGE,"E16.179.3"),sQuery(id+"F0.wireOp",EDGE,"E16.179.4"),sQuery(id+"F0.wireOp",EDGE,"E16.180.0"),sQuery(id+"F0.wireOp",EDGE,"E16.180.1"),sQuery(id+"F0.wireOp",EDGE,"E16.180.2"),sQuery(id+"F0.wireOp",EDGE,"E16.180.3"),sQuery(id+"F0.wireOp",EDGE,"E16.180.4"),sQuery(id+"F0.wireOp",EDGE,"E16.181.0"),sQuery(id+"F0.wireOp",EDGE,"E16.181.1"),sQuery(id+"F0.wireOp",EDGE,"E16.181.2"),sQuery(id+"F0.wireOp",EDGE,"E16.181.3"),sQuery(id+"F0.wireOp",EDGE,"E16.181.4"),sQuery(id+"F0.wireOp",EDGE,"E16.182.0"),sQuery(id+"F0.wireOp",EDGE,"E16.182.1"),sQuery(id+"F0.wireOp",EDGE,"E16.182.2"),sQuery(id+"F0.wireOp",EDGE,"E16.182.3"),sQuery(id+"F0.wireOp",EDGE,"E16.182.4"),sQuery(id+"F0.wireOp",EDGE,"E16.183.0"),sQuery(id+"F0.wireOp",EDGE,"E16.183.1"),sQuery(id+"F0.wireOp",EDGE,"E16.183.2"),sQuery(id+"F0.wireOp",EDGE,"E16.183.3"),sQuery(id+"F0.wireOp",EDGE,"E16.183.4"),sQuery(id+"F0.wireOp",EDGE,"E16.184.0"),sQuery(id+"F0.wireOp",EDGE,"E16.184.1"),sQuery(id+"F0.wireOp",EDGE,"E16.184.2"),sQuery(id+"F0.wireOp",EDGE,"E16.184.3"),sQuery(id+"F0.wireOp",EDGE,"E16.184.4"),sQuery(id+"F0.wireOp",EDGE,"E16.185.0"),sQuery(id+"F0.wireOp",EDGE,"E16.185.1"),sQuery(id+"F0.wireOp",EDGE,"E16.185.2"),sQuery(id+"F0.wireOp",EDGE,"E16.185.3"),sQuery(id+"F0.wireOp",EDGE,"E16.185.4"),sQuery(id+"F0.wireOp",EDGE,"E16.186.0"),sQuery(id+"F0.wireOp",EDGE,"E16.186.1"),sQuery(id+"F0.wireOp",EDGE,"E16.186.2"),sQuery(id+"F0.wireOp",EDGE,"E16.186.3"),sQuery(id+"F0.wireOp",EDGE,"E16.186.4"),sQuery(id+"F0.wireOp",EDGE,"E16.187.0"),sQuery(id+"F0.wireOp",EDGE,"E16.187.1"),sQuery(id+"F0.wireOp",EDGE,"E16.187.2"),sQuery(id+"F0.wireOp",EDGE,"E16.187.3"),sQuery(id+"F0.wireOp",EDGE,"E16.187.4"),sQuery(id+"F0.wireOp",EDGE,"E16.188.0"),sQuery(id+"F0.wireOp",EDGE,"E16.188.1"),sQuery(id+"F0.wireOp",EDGE,"E16.188.2"),sQuery(id+"F0.wireOp",EDGE,"E16.188.3"),sQuery(id+"F0.wireOp",EDGE,"E16.188.4"),sQuery(id+"F0.wireOp",EDGE,"E16.189.0"),sQuery(id+"F0.wireOp",EDGE,"E16.189.1"),sQuery(id+"F0.wireOp",EDGE,"E16.189.2"),sQuery(id+"F0.wireOp",EDGE,"E16.189.3"),sQuery(id+"F0.wireOp",EDGE,"E16.189.4"),sQuery(id+"F0.wireOp",EDGE,"E16.190.0"),sQuery(id+"F0.wireOp",EDGE,"E16.190.1"),sQuery(id+"F0.wireOp",EDGE,"E16.190.2"),sQuery(id+"F0.wireOp",EDGE,"E16.190.3"),sQuery(id+"F0.wireOp",EDGE,"E16.190.4"),sQuery(id+"F0.wireOp",EDGE,"E16.191.0"),sQuery(id+"F0.wireOp",EDGE,"E16.191.1"),sQuery(id+"F0.wireOp",EDGE,"E16.191.2"),sQuery(id+"F0.wireOp",EDGE,"E16.191.3"),sQuery(id+"F0.wireOp",EDGE,"E16.191.4")])],"isStart":false});
            var sketch = newSketch(context, id + "F3", { "sketchPlane" : qUnion([Q0])});
            skArc(sketch, "E21.0", {"start": v(-89.73, 7) * mm, "mid": v(-90, 0) * mm, "end": v(-89.73, -7) * mm});
            skLineSegment(sketch, "E22", {"start": v(-28.77, 0) * mm, "end": v(-133.54, 0.01) * mm, "construction": true});
            skArc(sketch, "E23", {"start": v(-89.73, -7) * mm, "mid": v(-83, 0) * mm, "end": v(-89.73, 7) * mm});
            skSolve(sketch);
        }
        {
            var Q0;
            Q0=qSketchRegion(id+"F3",true);
            extrude(context, id + "F4", {"entities" : qUnion([Q0]), "operationType" : NewBodyOperationType.ADD, "oppositeDirection" : true, "depth" : 20 * mm, "offsetDistance" : 25 * mm});
        }
        {
            var Q0;
            Q0=makeQuery(id+"F2.imprint","IMPRINT",FACE,{"disambiguationData":[TD([[makeQuery(id+"F2.imprint","IMPRINT",EDGE,{"derivedFrom":makeQuery(id+"F1.opExtrude","CAP_EDGE",EDGE,{"disambiguationData":[OSD([sQuery(id+"F0.wireOp",EDGE,"E0")])],"isStart":true})}),1.0]])]});
            var sketch = newSketch(context, id + "F5", { "sketchPlane" : qUnion([Q0])});
            skPoint(sketch, "E24.0", {"position": v(81.2, 38.8) * mm});
            skCircle(sketch, "E25", {"center": v(0, 0) * mm, "radius": 90 * mm, "construction": true});
            skPoint(sketch, "E26", {"position": v(90, 0) * mm});
            skSolve(sketch);
        }
        {
            var Q0;
            Q0=sQuery(id+"F5.wireOp",VERTEX,"E26");
            var Q1;
            Q1=makeQuery(id+"F1.opExtrude","SWEPT_BODY",BODY,{"disambiguationData":[OSD([sQuery(id+"F0.wireOp",EDGE,"E0"),sQuery(id+"F0.wireOp",EDGE,"E4"),sQuery(id+"F0.wireOp",EDGE,"E5"),sQuery(id+"F0.wireOp",EDGE,"E6.filletArc"),sQuery(id+"F0.wireOp",EDGE,"E7.MirrorCS"),sQuery(id+"F0.wireOp",EDGE,"E8.MirrorCS"),sQuery(id+"F0.wireOp",EDGE,"E15"),sQuery(id+"F0.wireOp",EDGE,"E16.1.0"),sQuery(id+"F0.wireOp",EDGE,"E16.1.1"),sQuery(id+"F0.wireOp",EDGE,"E16.1.2"),sQuery(id+"F0.wireOp",EDGE,"E16.1.3"),sQuery(id+"F0.wireOp",EDGE,"E16.1.4"),sQuery(id+"F0.wireOp",EDGE,"E16.2.0"),sQuery(id+"F0.wireOp",EDGE,"E16.2.1"),sQuery(id+"F0.wireOp",EDGE,"E16.2.2"),sQuery(id+"F0.wireOp",EDGE,"E16.2.3"),sQuery(id+"F0.wireOp",EDGE,"E16.2.4"),sQuery(id+"F0.wireOp",EDGE,"E16.3.0"),sQuery(id+"F0.wireOp",EDGE,"E16.3.1"),sQuery(id+"F0.wireOp",EDGE,"E16.3.2"),sQuery(id+"F0.wireOp",EDGE,"E16.3.3"),sQuery(id+"F0.wireOp",EDGE,"E16.3.4"),sQuery(id+"F0.wireOp",EDGE,"E16.4.0"),sQuery(id+"F0.wireOp",EDGE,"E16.4.1"),sQuery(id+"F0.wireOp",EDGE,"E16.4.2"),sQuery(id+"F0.wireOp",EDGE,"E16.4.3"),sQuery(id+"F0.wireOp",EDGE,"E16.4.4"),sQuery(id+"F0.wireOp",EDGE,"E16.5.0"),sQuery(id+"F0.wireOp",EDGE,"E16.5.1"),sQuery(id+"F0.wireOp",EDGE,"E16.5.2"),sQuery(id+"F0.wireOp",EDGE,"E16.5.3"),sQuery(id+"F0.wireOp",EDGE,"E16.5.4"),sQuery(id+"F0.wireOp",EDGE,"E16.6.0"),sQuery(id+"F0.wireOp",EDGE,"E16.6.1"),sQuery(id+"F0.wireOp",EDGE,"E16.6.2"),sQuery(id+"F0.wireOp",EDGE,"E16.6.3"),sQuery(id+"F0.wireOp",EDGE,"E16.6.4"),sQuery(id+"F0.wireOp",EDGE,"E16.7.0"),sQuery(id+"F0.wireOp",EDGE,"E16.7.1"),sQuery(id+"F0.wireOp",EDGE,"E16.7.2"),sQuery(id+"F0.wireOp",EDGE,"E16.7.3"),sQuery(id+"F0.wireOp",EDGE,"E16.7.4"),sQuery(id+"F0.wireOp",EDGE,"E16.8.0"),sQuery(id+"F0.wireOp",EDGE,"E16.8.1"),sQuery(id+"F0.wireOp",EDGE,"E16.8.2"),sQuery(id+"F0.wireOp",EDGE,"E16.8.3"),sQuery(id+"F0.wireOp",EDGE,"E16.8.4"),sQuery(id+"F0.wireOp",EDGE,"E16.9.0"),sQuery(id+"F0.wireOp",EDGE,"E16.9.1"),sQuery(id+"F0.wireOp",EDGE,"E16.9.2"),sQuery(id+"F0.wireOp",EDGE,"E16.9.3"),sQuery(id+"F0.wireOp",EDGE,"E16.9.4"),sQuery(id+"F0.wireOp",EDGE,"E16.10.0"),sQuery(id+"F0.wireOp",EDGE,"E16.10.1"),sQuery(id+"F0.wireOp",EDGE,"E16.10.2"),sQuery(id+"F0.wireOp",EDGE,"E16.10.3"),sQuery(id+"F0.wireOp",EDGE,"E16.10.4"),sQuery(id+"F0.wireOp",EDGE,"E16.11.0"),sQuery(id+"F0.wireOp",EDGE,"E16.11.1"),sQuery(id+"F0.wireOp",EDGE,"E16.11.2"),sQuery(id+"F0.wireOp",EDGE,"E16.11.3"),sQuery(id+"F0.wireOp",EDGE,"E16.11.4"),sQuery(id+"F0.wireOp",EDGE,"E16.12.0"),sQuery(id+"F0.wireOp",EDGE,"E16.12.1"),sQuery(id+"F0.wireOp",EDGE,"E16.12.2"),sQuery(id+"F0.wireOp",EDGE,"E16.12.3"),sQuery(id+"F0.wireOp",EDGE,"E16.12.4"),sQuery(id+"F0.wireOp",EDGE,"E16.13.0"),sQuery(id+"F0.wireOp",EDGE,"E16.13.1"),sQuery(id+"F0.wireOp",EDGE,"E16.13.2"),sQuery(id+"F0.wireOp",EDGE,"E16.13.3"),sQuery(id+"F0.wireOp",EDGE,"E16.13.4"),sQuery(id+"F0.wireOp",EDGE,"E16.14.0"),sQuery(id+"F0.wireOp",EDGE,"E16.14.1"),sQuery(id+"F0.wireOp",EDGE,"E16.14.2"),sQuery(id+"F0.wireOp",EDGE,"E16.14.3"),sQuery(id+"F0.wireOp",EDGE,"E16.14.4"),sQuery(id+"F0.wireOp",EDGE,"E16.15.0"),sQuery(id+"F0.wireOp",EDGE,"E16.15.1"),sQuery(id+"F0.wireOp",EDGE,"E16.15.2"),sQuery(id+"F0.wireOp",EDGE,"E16.15.3"),sQuery(id+"F0.wireOp",EDGE,"E16.15.4"),sQuery(id+"F0.wireOp",EDGE,"E16.16.0"),sQuery(id+"F0.wireOp",EDGE,"E16.16.1"),sQuery(id+"F0.wireOp",EDGE,"E16.16.2"),sQuery(id+"F0.wireOp",EDGE,"E16.16.3"),sQuery(id+"F0.wireOp",EDGE,"E16.16.4"),sQuery(id+"F0.wireOp",EDGE,"E16.17.0"),sQuery(id+"F0.wireOp",EDGE,"E16.17.1"),sQuery(id+"F0.wireOp",EDGE,"E16.17.2"),sQuery(id+"F0.wireOp",EDGE,"E16.17.3"),sQuery(id+"F0.wireOp",EDGE,"E16.17.4"),sQuery(id+"F0.wireOp",EDGE,"E16.18.0"),sQuery(id+"F0.wireOp",EDGE,"E16.18.1"),sQuery(id+"F0.wireOp",EDGE,"E16.18.2"),sQuery(id+"F0.wireOp",EDGE,"E16.18.3"),sQuery(id+"F0.wireOp",EDGE,"E16.18.4"),sQuery(id+"F0.wireOp",EDGE,"E16.19.0"),sQuery(id+"F0.wireOp",EDGE,"E16.19.1"),sQuery(id+"F0.wireOp",EDGE,"E16.19.2"),sQuery(id+"F0.wireOp",EDGE,"E16.19.3"),sQuery(id+"F0.wireOp",EDGE,"E16.19.4"),sQuery(id+"F0.wireOp",EDGE,"E16.20.0"),sQuery(id+"F0.wireOp",EDGE,"E16.20.1"),sQuery(id+"F0.wireOp",EDGE,"E16.20.2"),sQuery(id+"F0.wireOp",EDGE,"E16.20.3"),sQuery(id+"F0.wireOp",EDGE,"E16.20.4"),sQuery(id+"F0.wireOp",EDGE,"E16.21.0"),sQuery(id+"F0.wireOp",EDGE,"E16.21.1"),sQuery(id+"F0.wireOp",EDGE,"E16.21.2"),sQuery(id+"F0.wireOp",EDGE,"E16.21.3"),sQuery(id+"F0.wireOp",EDGE,"E16.21.4"),sQuery(id+"F0.wireOp",EDGE,"E16.22.0"),sQuery(id+"F0.wireOp",EDGE,"E16.22.1"),sQuery(id+"F0.wireOp",EDGE,"E16.22.2"),sQuery(id+"F0.wireOp",EDGE,"E16.22.3"),sQuery(id+"F0.wireOp",EDGE,"E16.22.4"),sQuery(id+"F0.wireOp",EDGE,"E16.23.0"),sQuery(id+"F0.wireOp",EDGE,"E16.23.1"),sQuery(id+"F0.wireOp",EDGE,"E16.23.2"),sQuery(id+"F0.wireOp",EDGE,"E16.23.3"),sQuery(id+"F0.wireOp",EDGE,"E16.23.4"),sQuery(id+"F0.wireOp",EDGE,"E16.24.0"),sQuery(id+"F0.wireOp",EDGE,"E16.24.1"),sQuery(id+"F0.wireOp",EDGE,"E16.24.2"),sQuery(id+"F0.wireOp",EDGE,"E16.24.3"),sQuery(id+"F0.wireOp",EDGE,"E16.24.4"),sQuery(id+"F0.wireOp",EDGE,"E16.25.0"),sQuery(id+"F0.wireOp",EDGE,"E16.25.1"),sQuery(id+"F0.wireOp",EDGE,"E16.25.2"),sQuery(id+"F0.wireOp",EDGE,"E16.25.3"),sQuery(id+"F0.wireOp",EDGE,"E16.25.4"),sQuery(id+"F0.wireOp",EDGE,"E16.26.0"),sQuery(id+"F0.wireOp",EDGE,"E16.26.1"),sQuery(id+"F0.wireOp",EDGE,"E16.26.2"),sQuery(id+"F0.wireOp",EDGE,"E16.26.3"),sQuery(id+"F0.wireOp",EDGE,"E16.26.4"),sQuery(id+"F0.wireOp",EDGE,"E16.27.0"),sQuery(id+"F0.wireOp",EDGE,"E16.27.1"),sQuery(id+"F0.wireOp",EDGE,"E16.27.2"),sQuery(id+"F0.wireOp",EDGE,"E16.27.3"),sQuery(id+"F0.wireOp",EDGE,"E16.27.4"),sQuery(id+"F0.wireOp",EDGE,"E16.28.0"),sQuery(id+"F0.wireOp",EDGE,"E16.28.1"),sQuery(id+"F0.wireOp",EDGE,"E16.28.2"),sQuery(id+"F0.wireOp",EDGE,"E16.28.3"),sQuery(id+"F0.wireOp",EDGE,"E16.28.4"),sQuery(id+"F0.wireOp",EDGE,"E16.29.0"),sQuery(id+"F0.wireOp",EDGE,"E16.29.1"),sQuery(id+"F0.wireOp",EDGE,"E16.29.2"),sQuery(id+"F0.wireOp",EDGE,"E16.29.3"),sQuery(id+"F0.wireOp",EDGE,"E16.29.4"),sQuery(id+"F0.wireOp",EDGE,"E16.30.0"),sQuery(id+"F0.wireOp",EDGE,"E16.30.1"),sQuery(id+"F0.wireOp",EDGE,"E16.30.2"),sQuery(id+"F0.wireOp",EDGE,"E16.30.3"),sQuery(id+"F0.wireOp",EDGE,"E16.30.4"),sQuery(id+"F0.wireOp",EDGE,"E16.31.0"),sQuery(id+"F0.wireOp",EDGE,"E16.31.1"),sQuery(id+"F0.wireOp",EDGE,"E16.31.2"),sQuery(id+"F0.wireOp",EDGE,"E16.31.3"),sQuery(id+"F0.wireOp",EDGE,"E16.31.4"),sQuery(id+"F0.wireOp",EDGE,"E16.32.0"),sQuery(id+"F0.wireOp",EDGE,"E16.32.1"),sQuery(id+"F0.wireOp",EDGE,"E16.32.2"),sQuery(id+"F0.wireOp",EDGE,"E16.32.3"),sQuery(id+"F0.wireOp",EDGE,"E16.32.4"),sQuery(id+"F0.wireOp",EDGE,"E16.33.0"),sQuery(id+"F0.wireOp",EDGE,"E16.33.1"),sQuery(id+"F0.wireOp",EDGE,"E16.33.2"),sQuery(id+"F0.wireOp",EDGE,"E16.33.3"),sQuery(id+"F0.wireOp",EDGE,"E16.33.4"),sQuery(id+"F0.wireOp",EDGE,"E16.34.0"),sQuery(id+"F0.wireOp",EDGE,"E16.34.1"),sQuery(id+"F0.wireOp",EDGE,"E16.34.2"),sQuery(id+"F0.wireOp",EDGE,"E16.34.3"),sQuery(id+"F0.wireOp",EDGE,"E16.34.4"),sQuery(id+"F0.wireOp",EDGE,"E16.35.0"),sQuery(id+"F0.wireOp",EDGE,"E16.35.1"),sQuery(id+"F0.wireOp",EDGE,"E16.35.2"),sQuery(id+"F0.wireOp",EDGE,"E16.35.3"),sQuery(id+"F0.wireOp",EDGE,"E16.35.4"),sQuery(id+"F0.wireOp",EDGE,"E16.36.0"),sQuery(id+"F0.wireOp",EDGE,"E16.36.1"),sQuery(id+"F0.wireOp",EDGE,"E16.36.2"),sQuery(id+"F0.wireOp",EDGE,"E16.36.3"),sQuery(id+"F0.wireOp",EDGE,"E16.36.4"),sQuery(id+"F0.wireOp",EDGE,"E16.37.0"),sQuery(id+"F0.wireOp",EDGE,"E16.37.1"),sQuery(id+"F0.wireOp",EDGE,"E16.37.2"),sQuery(id+"F0.wireOp",EDGE,"E16.37.3"),sQuery(id+"F0.wireOp",EDGE,"E16.37.4"),sQuery(id+"F0.wireOp",EDGE,"E16.38.0"),sQuery(id+"F0.wireOp",EDGE,"E16.38.1"),sQuery(id+"F0.wireOp",EDGE,"E16.38.2"),sQuery(id+"F0.wireOp",EDGE,"E16.38.3"),sQuery(id+"F0.wireOp",EDGE,"E16.38.4"),sQuery(id+"F0.wireOp",EDGE,"E16.39.0"),sQuery(id+"F0.wireOp",EDGE,"E16.39.1"),sQuery(id+"F0.wireOp",EDGE,"E16.39.2"),sQuery(id+"F0.wireOp",EDGE,"E16.39.3"),sQuery(id+"F0.wireOp",EDGE,"E16.39.4"),sQuery(id+"F0.wireOp",EDGE,"E16.40.0"),sQuery(id+"F0.wireOp",EDGE,"E16.40.1"),sQuery(id+"F0.wireOp",EDGE,"E16.40.2"),sQuery(id+"F0.wireOp",EDGE,"E16.40.3"),sQuery(id+"F0.wireOp",EDGE,"E16.40.4"),sQuery(id+"F0.wireOp",EDGE,"E16.41.0"),sQuery(id+"F0.wireOp",EDGE,"E16.41.1"),sQuery(id+"F0.wireOp",EDGE,"E16.41.2"),sQuery(id+"F0.wireOp",EDGE,"E16.41.3"),sQuery(id+"F0.wireOp",EDGE,"E16.41.4"),sQuery(id+"F0.wireOp",EDGE,"E16.42.0"),sQuery(id+"F0.wireOp",EDGE,"E16.42.1"),sQuery(id+"F0.wireOp",EDGE,"E16.42.2"),sQuery(id+"F0.wireOp",EDGE,"E16.42.3"),sQuery(id+"F0.wireOp",EDGE,"E16.42.4"),sQuery(id+"F0.wireOp",EDGE,"E16.43.0"),sQuery(id+"F0.wireOp",EDGE,"E16.43.1"),sQuery(id+"F0.wireOp",EDGE,"E16.43.2"),sQuery(id+"F0.wireOp",EDGE,"E16.43.3"),sQuery(id+"F0.wireOp",EDGE,"E16.43.4"),sQuery(id+"F0.wireOp",EDGE,"E16.44.0"),sQuery(id+"F0.wireOp",EDGE,"E16.44.1"),sQuery(id+"F0.wireOp",EDGE,"E16.44.2"),sQuery(id+"F0.wireOp",EDGE,"E16.44.3"),sQuery(id+"F0.wireOp",EDGE,"E16.44.4"),sQuery(id+"F0.wireOp",EDGE,"E16.45.0"),sQuery(id+"F0.wireOp",EDGE,"E16.45.1"),sQuery(id+"F0.wireOp",EDGE,"E16.45.2"),sQuery(id+"F0.wireOp",EDGE,"E16.45.3"),sQuery(id+"F0.wireOp",EDGE,"E16.45.4"),sQuery(id+"F0.wireOp",EDGE,"E16.46.0"),sQuery(id+"F0.wireOp",EDGE,"E16.46.1"),sQuery(id+"F0.wireOp",EDGE,"E16.46.2"),sQuery(id+"F0.wireOp",EDGE,"E16.46.3"),sQuery(id+"F0.wireOp",EDGE,"E16.46.4"),sQuery(id+"F0.wireOp",EDGE,"E16.47.0"),sQuery(id+"F0.wireOp",EDGE,"E16.47.1"),sQuery(id+"F0.wireOp",EDGE,"E16.47.2"),sQuery(id+"F0.wireOp",EDGE,"E16.47.3"),sQuery(id+"F0.wireOp",EDGE,"E16.47.4"),sQuery(id+"F0.wireOp",EDGE,"E16.48.0"),sQuery(id+"F0.wireOp",EDGE,"E16.48.1"),sQuery(id+"F0.wireOp",EDGE,"E16.48.2"),sQuery(id+"F0.wireOp",EDGE,"E16.48.3"),sQuery(id+"F0.wireOp",EDGE,"E16.48.4"),sQuery(id+"F0.wireOp",EDGE,"E16.49.0"),sQuery(id+"F0.wireOp",EDGE,"E16.49.1"),sQuery(id+"F0.wireOp",EDGE,"E16.49.2"),sQuery(id+"F0.wireOp",EDGE,"E16.49.3"),sQuery(id+"F0.wireOp",EDGE,"E16.49.4"),sQuery(id+"F0.wireOp",EDGE,"E16.50.0"),sQuery(id+"F0.wireOp",EDGE,"E16.50.1"),sQuery(id+"F0.wireOp",EDGE,"E16.50.2"),sQuery(id+"F0.wireOp",EDGE,"E16.50.3"),sQuery(id+"F0.wireOp",EDGE,"E16.50.4"),sQuery(id+"F0.wireOp",EDGE,"E16.51.0"),sQuery(id+"F0.wireOp",EDGE,"E16.51.1"),sQuery(id+"F0.wireOp",EDGE,"E16.51.2"),sQuery(id+"F0.wireOp",EDGE,"E16.51.3"),sQuery(id+"F0.wireOp",EDGE,"E16.51.4"),sQuery(id+"F0.wireOp",EDGE,"E16.52.0"),sQuery(id+"F0.wireOp",EDGE,"E16.52.1"),sQuery(id+"F0.wireOp",EDGE,"E16.52.2"),sQuery(id+"F0.wireOp",EDGE,"E16.52.3"),sQuery(id+"F0.wireOp",EDGE,"E16.52.4"),sQuery(id+"F0.wireOp",EDGE,"E16.53.0"),sQuery(id+"F0.wireOp",EDGE,"E16.53.1"),sQuery(id+"F0.wireOp",EDGE,"E16.53.2"),sQuery(id+"F0.wireOp",EDGE,"E16.53.3"),sQuery(id+"F0.wireOp",EDGE,"E16.53.4"),sQuery(id+"F0.wireOp",EDGE,"E16.54.0"),sQuery(id+"F0.wireOp",EDGE,"E16.54.1"),sQuery(id+"F0.wireOp",EDGE,"E16.54.2"),sQuery(id+"F0.wireOp",EDGE,"E16.54.3"),sQuery(id+"F0.wireOp",EDGE,"E16.54.4"),sQuery(id+"F0.wireOp",EDGE,"E16.55.0"),sQuery(id+"F0.wireOp",EDGE,"E16.55.1"),sQuery(id+"F0.wireOp",EDGE,"E16.55.2"),sQuery(id+"F0.wireOp",EDGE,"E16.55.3"),sQuery(id+"F0.wireOp",EDGE,"E16.55.4"),sQuery(id+"F0.wireOp",EDGE,"E16.56.0"),sQuery(id+"F0.wireOp",EDGE,"E16.56.1"),sQuery(id+"F0.wireOp",EDGE,"E16.56.2"),sQuery(id+"F0.wireOp",EDGE,"E16.56.3"),sQuery(id+"F0.wireOp",EDGE,"E16.56.4"),sQuery(id+"F0.wireOp",EDGE,"E16.57.0"),sQuery(id+"F0.wireOp",EDGE,"E16.57.1"),sQuery(id+"F0.wireOp",EDGE,"E16.57.2"),sQuery(id+"F0.wireOp",EDGE,"E16.57.3"),sQuery(id+"F0.wireOp",EDGE,"E16.57.4"),sQuery(id+"F0.wireOp",EDGE,"E16.58.0"),sQuery(id+"F0.wireOp",EDGE,"E16.58.1"),sQuery(id+"F0.wireOp",EDGE,"E16.58.2"),sQuery(id+"F0.wireOp",EDGE,"E16.58.3"),sQuery(id+"F0.wireOp",EDGE,"E16.58.4"),sQuery(id+"F0.wireOp",EDGE,"E16.59.0"),sQuery(id+"F0.wireOp",EDGE,"E16.59.1"),sQuery(id+"F0.wireOp",EDGE,"E16.59.2"),sQuery(id+"F0.wireOp",EDGE,"E16.59.3"),sQuery(id+"F0.wireOp",EDGE,"E16.59.4"),sQuery(id+"F0.wireOp",EDGE,"E16.60.0"),sQuery(id+"F0.wireOp",EDGE,"E16.60.1"),sQuery(id+"F0.wireOp",EDGE,"E16.60.2"),sQuery(id+"F0.wireOp",EDGE,"E16.60.3"),sQuery(id+"F0.wireOp",EDGE,"E16.60.4"),sQuery(id+"F0.wireOp",EDGE,"E16.61.0"),sQuery(id+"F0.wireOp",EDGE,"E16.61.1"),sQuery(id+"F0.wireOp",EDGE,"E16.61.2"),sQuery(id+"F0.wireOp",EDGE,"E16.61.3"),sQuery(id+"F0.wireOp",EDGE,"E16.61.4"),sQuery(id+"F0.wireOp",EDGE,"E16.62.0"),sQuery(id+"F0.wireOp",EDGE,"E16.62.1"),sQuery(id+"F0.wireOp",EDGE,"E16.62.2"),sQuery(id+"F0.wireOp",EDGE,"E16.62.3"),sQuery(id+"F0.wireOp",EDGE,"E16.62.4"),sQuery(id+"F0.wireOp",EDGE,"E16.63.0"),sQuery(id+"F0.wireOp",EDGE,"E16.63.1"),sQuery(id+"F0.wireOp",EDGE,"E16.63.2"),sQuery(id+"F0.wireOp",EDGE,"E16.63.3"),sQuery(id+"F0.wireOp",EDGE,"E16.63.4"),sQuery(id+"F0.wireOp",EDGE,"E16.64.0"),sQuery(id+"F0.wireOp",EDGE,"E16.64.1"),sQuery(id+"F0.wireOp",EDGE,"E16.64.2"),sQuery(id+"F0.wireOp",EDGE,"E16.64.3"),sQuery(id+"F0.wireOp",EDGE,"E16.64.4"),sQuery(id+"F0.wireOp",EDGE,"E16.65.0"),sQuery(id+"F0.wireOp",EDGE,"E16.65.1"),sQuery(id+"F0.wireOp",EDGE,"E16.65.2"),sQuery(id+"F0.wireOp",EDGE,"E16.65.3"),sQuery(id+"F0.wireOp",EDGE,"E16.65.4"),sQuery(id+"F0.wireOp",EDGE,"E16.66.0"),sQuery(id+"F0.wireOp",EDGE,"E16.66.1"),sQuery(id+"F0.wireOp",EDGE,"E16.66.2"),sQuery(id+"F0.wireOp",EDGE,"E16.66.3"),sQuery(id+"F0.wireOp",EDGE,"E16.66.4"),sQuery(id+"F0.wireOp",EDGE,"E16.67.0"),sQuery(id+"F0.wireOp",EDGE,"E16.67.1"),sQuery(id+"F0.wireOp",EDGE,"E16.67.2"),sQuery(id+"F0.wireOp",EDGE,"E16.67.3"),sQuery(id+"F0.wireOp",EDGE,"E16.67.4"),sQuery(id+"F0.wireOp",EDGE,"E16.68.0"),sQuery(id+"F0.wireOp",EDGE,"E16.68.1"),sQuery(id+"F0.wireOp",EDGE,"E16.68.2"),sQuery(id+"F0.wireOp",EDGE,"E16.68.3"),sQuery(id+"F0.wireOp",EDGE,"E16.68.4"),sQuery(id+"F0.wireOp",EDGE,"E16.69.0"),sQuery(id+"F0.wireOp",EDGE,"E16.69.1"),sQuery(id+"F0.wireOp",EDGE,"E16.69.2"),sQuery(id+"F0.wireOp",EDGE,"E16.69.3"),sQuery(id+"F0.wireOp",EDGE,"E16.69.4"),sQuery(id+"F0.wireOp",EDGE,"E16.70.0"),sQuery(id+"F0.wireOp",EDGE,"E16.70.1"),sQuery(id+"F0.wireOp",EDGE,"E16.70.2"),sQuery(id+"F0.wireOp",EDGE,"E16.70.3"),sQuery(id+"F0.wireOp",EDGE,"E16.70.4"),sQuery(id+"F0.wireOp",EDGE,"E16.71.0"),sQuery(id+"F0.wireOp",EDGE,"E16.71.1"),sQuery(id+"F0.wireOp",EDGE,"E16.71.2"),sQuery(id+"F0.wireOp",EDGE,"E16.71.3"),sQuery(id+"F0.wireOp",EDGE,"E16.71.4"),sQuery(id+"F0.wireOp",EDGE,"E16.72.0"),sQuery(id+"F0.wireOp",EDGE,"E16.72.1"),sQuery(id+"F0.wireOp",EDGE,"E16.72.2"),sQuery(id+"F0.wireOp",EDGE,"E16.72.3"),sQuery(id+"F0.wireOp",EDGE,"E16.72.4"),sQuery(id+"F0.wireOp",EDGE,"E16.73.0"),sQuery(id+"F0.wireOp",EDGE,"E16.73.1"),sQuery(id+"F0.wireOp",EDGE,"E16.73.2"),sQuery(id+"F0.wireOp",EDGE,"E16.73.3"),sQuery(id+"F0.wireOp",EDGE,"E16.73.4"),sQuery(id+"F0.wireOp",EDGE,"E16.74.0"),sQuery(id+"F0.wireOp",EDGE,"E16.74.1"),sQuery(id+"F0.wireOp",EDGE,"E16.74.2"),sQuery(id+"F0.wireOp",EDGE,"E16.74.3"),sQuery(id+"F0.wireOp",EDGE,"E16.74.4"),sQuery(id+"F0.wireOp",EDGE,"E16.75.0"),sQuery(id+"F0.wireOp",EDGE,"E16.75.1"),sQuery(id+"F0.wireOp",EDGE,"E16.75.2"),sQuery(id+"F0.wireOp",EDGE,"E16.75.3"),sQuery(id+"F0.wireOp",EDGE,"E16.75.4"),sQuery(id+"F0.wireOp",EDGE,"E16.76.0"),sQuery(id+"F0.wireOp",EDGE,"E16.76.1"),sQuery(id+"F0.wireOp",EDGE,"E16.76.2"),sQuery(id+"F0.wireOp",EDGE,"E16.76.3"),sQuery(id+"F0.wireOp",EDGE,"E16.76.4"),sQuery(id+"F0.wireOp",EDGE,"E16.77.0"),sQuery(id+"F0.wireOp",EDGE,"E16.77.1"),sQuery(id+"F0.wireOp",EDGE,"E16.77.2"),sQuery(id+"F0.wireOp",EDGE,"E16.77.3"),sQuery(id+"F0.wireOp",EDGE,"E16.77.4"),sQuery(id+"F0.wireOp",EDGE,"E16.78.0"),sQuery(id+"F0.wireOp",EDGE,"E16.78.1"),sQuery(id+"F0.wireOp",EDGE,"E16.78.2"),sQuery(id+"F0.wireOp",EDGE,"E16.78.3"),sQuery(id+"F0.wireOp",EDGE,"E16.78.4"),sQuery(id+"F0.wireOp",EDGE,"E16.79.0"),sQuery(id+"F0.wireOp",EDGE,"E16.79.1"),sQuery(id+"F0.wireOp",EDGE,"E16.79.2"),sQuery(id+"F0.wireOp",EDGE,"E16.79.3"),sQuery(id+"F0.wireOp",EDGE,"E16.79.4"),sQuery(id+"F0.wireOp",EDGE,"E16.80.0"),sQuery(id+"F0.wireOp",EDGE,"E16.80.1"),sQuery(id+"F0.wireOp",EDGE,"E16.80.2"),sQuery(id+"F0.wireOp",EDGE,"E16.80.3"),sQuery(id+"F0.wireOp",EDGE,"E16.80.4"),sQuery(id+"F0.wireOp",EDGE,"E16.81.0"),sQuery(id+"F0.wireOp",EDGE,"E16.81.1"),sQuery(id+"F0.wireOp",EDGE,"E16.81.2"),sQuery(id+"F0.wireOp",EDGE,"E16.81.3"),sQuery(id+"F0.wireOp",EDGE,"E16.81.4"),sQuery(id+"F0.wireOp",EDGE,"E16.82.0"),sQuery(id+"F0.wireOp",EDGE,"E16.82.1"),sQuery(id+"F0.wireOp",EDGE,"E16.82.2"),sQuery(id+"F0.wireOp",EDGE,"E16.82.3"),sQuery(id+"F0.wireOp",EDGE,"E16.82.4"),sQuery(id+"F0.wireOp",EDGE,"E16.83.0"),sQuery(id+"F0.wireOp",EDGE,"E16.83.1"),sQuery(id+"F0.wireOp",EDGE,"E16.83.2"),sQuery(id+"F0.wireOp",EDGE,"E16.83.3"),sQuery(id+"F0.wireOp",EDGE,"E16.83.4"),sQuery(id+"F0.wireOp",EDGE,"E16.84.0"),sQuery(id+"F0.wireOp",EDGE,"E16.84.1"),sQuery(id+"F0.wireOp",EDGE,"E16.84.2"),sQuery(id+"F0.wireOp",EDGE,"E16.84.3"),sQuery(id+"F0.wireOp",EDGE,"E16.84.4"),sQuery(id+"F0.wireOp",EDGE,"E16.85.0"),sQuery(id+"F0.wireOp",EDGE,"E16.85.1"),sQuery(id+"F0.wireOp",EDGE,"E16.85.2"),sQuery(id+"F0.wireOp",EDGE,"E16.85.3"),sQuery(id+"F0.wireOp",EDGE,"E16.85.4"),sQuery(id+"F0.wireOp",EDGE,"E16.86.0"),sQuery(id+"F0.wireOp",EDGE,"E16.86.1"),sQuery(id+"F0.wireOp",EDGE,"E16.86.2"),sQuery(id+"F0.wireOp",EDGE,"E16.86.3"),sQuery(id+"F0.wireOp",EDGE,"E16.86.4"),sQuery(id+"F0.wireOp",EDGE,"E16.87.0"),sQuery(id+"F0.wireOp",EDGE,"E16.87.1"),sQuery(id+"F0.wireOp",EDGE,"E16.87.2"),sQuery(id+"F0.wireOp",EDGE,"E16.87.3"),sQuery(id+"F0.wireOp",EDGE,"E16.87.4"),sQuery(id+"F0.wireOp",EDGE,"E16.88.0"),sQuery(id+"F0.wireOp",EDGE,"E16.88.1"),sQuery(id+"F0.wireOp",EDGE,"E16.88.2"),sQuery(id+"F0.wireOp",EDGE,"E16.88.3"),sQuery(id+"F0.wireOp",EDGE,"E16.88.4"),sQuery(id+"F0.wireOp",EDGE,"E16.89.0"),sQuery(id+"F0.wireOp",EDGE,"E16.89.1"),sQuery(id+"F0.wireOp",EDGE,"E16.89.2"),sQuery(id+"F0.wireOp",EDGE,"E16.89.3"),sQuery(id+"F0.wireOp",EDGE,"E16.89.4"),sQuery(id+"F0.wireOp",EDGE,"E16.90.0"),sQuery(id+"F0.wireOp",EDGE,"E16.90.1"),sQuery(id+"F0.wireOp",EDGE,"E16.90.2"),sQuery(id+"F0.wireOp",EDGE,"E16.90.3"),sQuery(id+"F0.wireOp",EDGE,"E16.90.4"),sQuery(id+"F0.wireOp",EDGE,"E16.91.0"),sQuery(id+"F0.wireOp",EDGE,"E16.91.1"),sQuery(id+"F0.wireOp",EDGE,"E16.91.2"),sQuery(id+"F0.wireOp",EDGE,"E16.91.3"),sQuery(id+"F0.wireOp",EDGE,"E16.91.4"),sQuery(id+"F0.wireOp",EDGE,"E16.92.0"),sQuery(id+"F0.wireOp",EDGE,"E16.92.1"),sQuery(id+"F0.wireOp",EDGE,"E16.92.2"),sQuery(id+"F0.wireOp",EDGE,"E16.92.3"),sQuery(id+"F0.wireOp",EDGE,"E16.92.4"),sQuery(id+"F0.wireOp",EDGE,"E16.93.0"),sQuery(id+"F0.wireOp",EDGE,"E16.93.1"),sQuery(id+"F0.wireOp",EDGE,"E16.93.2"),sQuery(id+"F0.wireOp",EDGE,"E16.93.3"),sQuery(id+"F0.wireOp",EDGE,"E16.93.4"),sQuery(id+"F0.wireOp",EDGE,"E16.94.0"),sQuery(id+"F0.wireOp",EDGE,"E16.94.1"),sQuery(id+"F0.wireOp",EDGE,"E16.94.2"),sQuery(id+"F0.wireOp",EDGE,"E16.94.3"),sQuery(id+"F0.wireOp",EDGE,"E16.94.4"),sQuery(id+"F0.wireOp",EDGE,"E16.95.0"),sQuery(id+"F0.wireOp",EDGE,"E16.95.1"),sQuery(id+"F0.wireOp",EDGE,"E16.95.2"),sQuery(id+"F0.wireOp",EDGE,"E16.95.3"),sQuery(id+"F0.wireOp",EDGE,"E16.95.4"),sQuery(id+"F0.wireOp",EDGE,"E16.96.0"),sQuery(id+"F0.wireOp",EDGE,"E16.96.1"),sQuery(id+"F0.wireOp",EDGE,"E16.96.2"),sQuery(id+"F0.wireOp",EDGE,"E16.96.3"),sQuery(id+"F0.wireOp",EDGE,"E16.96.4"),sQuery(id+"F0.wireOp",EDGE,"E16.97.0"),sQuery(id+"F0.wireOp",EDGE,"E16.97.1"),sQuery(id+"F0.wireOp",EDGE,"E16.97.2"),sQuery(id+"F0.wireOp",EDGE,"E16.97.3"),sQuery(id+"F0.wireOp",EDGE,"E16.97.4"),sQuery(id+"F0.wireOp",EDGE,"E16.98.0"),sQuery(id+"F0.wireOp",EDGE,"E16.98.1"),sQuery(id+"F0.wireOp",EDGE,"E16.98.2"),sQuery(id+"F0.wireOp",EDGE,"E16.98.3"),sQuery(id+"F0.wireOp",EDGE,"E16.98.4"),sQuery(id+"F0.wireOp",EDGE,"E16.99.0"),sQuery(id+"F0.wireOp",EDGE,"E16.99.1"),sQuery(id+"F0.wireOp",EDGE,"E16.99.2"),sQuery(id+"F0.wireOp",EDGE,"E16.99.3"),sQuery(id+"F0.wireOp",EDGE,"E16.99.4"),sQuery(id+"F0.wireOp",EDGE,"E16.100.0"),sQuery(id+"F0.wireOp",EDGE,"E16.100.1"),sQuery(id+"F0.wireOp",EDGE,"E16.100.2"),sQuery(id+"F0.wireOp",EDGE,"E16.100.3"),sQuery(id+"F0.wireOp",EDGE,"E16.100.4"),sQuery(id+"F0.wireOp",EDGE,"E16.101.0"),sQuery(id+"F0.wireOp",EDGE,"E16.101.1"),sQuery(id+"F0.wireOp",EDGE,"E16.101.2"),sQuery(id+"F0.wireOp",EDGE,"E16.101.3"),sQuery(id+"F0.wireOp",EDGE,"E16.101.4"),sQuery(id+"F0.wireOp",EDGE,"E16.102.0"),sQuery(id+"F0.wireOp",EDGE,"E16.102.1"),sQuery(id+"F0.wireOp",EDGE,"E16.102.2"),sQuery(id+"F0.wireOp",EDGE,"E16.102.3"),sQuery(id+"F0.wireOp",EDGE,"E16.102.4"),sQuery(id+"F0.wireOp",EDGE,"E16.103.0"),sQuery(id+"F0.wireOp",EDGE,"E16.103.1"),sQuery(id+"F0.wireOp",EDGE,"E16.103.2"),sQuery(id+"F0.wireOp",EDGE,"E16.103.3"),sQuery(id+"F0.wireOp",EDGE,"E16.103.4"),sQuery(id+"F0.wireOp",EDGE,"E16.104.0"),sQuery(id+"F0.wireOp",EDGE,"E16.104.1"),sQuery(id+"F0.wireOp",EDGE,"E16.104.2"),sQuery(id+"F0.wireOp",EDGE,"E16.104.3"),sQuery(id+"F0.wireOp",EDGE,"E16.104.4"),sQuery(id+"F0.wireOp",EDGE,"E16.105.0"),sQuery(id+"F0.wireOp",EDGE,"E16.105.1"),sQuery(id+"F0.wireOp",EDGE,"E16.105.2"),sQuery(id+"F0.wireOp",EDGE,"E16.105.3"),sQuery(id+"F0.wireOp",EDGE,"E16.105.4"),sQuery(id+"F0.wireOp",EDGE,"E16.106.0"),sQuery(id+"F0.wireOp",EDGE,"E16.106.1"),sQuery(id+"F0.wireOp",EDGE,"E16.106.2"),sQuery(id+"F0.wireOp",EDGE,"E16.106.3"),sQuery(id+"F0.wireOp",EDGE,"E16.106.4"),sQuery(id+"F0.wireOp",EDGE,"E16.107.0"),sQuery(id+"F0.wireOp",EDGE,"E16.107.1"),sQuery(id+"F0.wireOp",EDGE,"E16.107.2"),sQuery(id+"F0.wireOp",EDGE,"E16.107.3"),sQuery(id+"F0.wireOp",EDGE,"E16.107.4"),sQuery(id+"F0.wireOp",EDGE,"E16.108.0"),sQuery(id+"F0.wireOp",EDGE,"E16.108.1"),sQuery(id+"F0.wireOp",EDGE,"E16.108.2"),sQuery(id+"F0.wireOp",EDGE,"E16.108.3"),sQuery(id+"F0.wireOp",EDGE,"E16.108.4"),sQuery(id+"F0.wireOp",EDGE,"E16.109.0"),sQuery(id+"F0.wireOp",EDGE,"E16.109.1"),sQuery(id+"F0.wireOp",EDGE,"E16.109.2"),sQuery(id+"F0.wireOp",EDGE,"E16.109.3"),sQuery(id+"F0.wireOp",EDGE,"E16.109.4"),sQuery(id+"F0.wireOp",EDGE,"E16.110.0"),sQuery(id+"F0.wireOp",EDGE,"E16.110.1"),sQuery(id+"F0.wireOp",EDGE,"E16.110.2"),sQuery(id+"F0.wireOp",EDGE,"E16.110.3"),sQuery(id+"F0.wireOp",EDGE,"E16.110.4"),sQuery(id+"F0.wireOp",EDGE,"E16.111.0"),sQuery(id+"F0.wireOp",EDGE,"E16.111.1"),sQuery(id+"F0.wireOp",EDGE,"E16.111.2"),sQuery(id+"F0.wireOp",EDGE,"E16.111.3"),sQuery(id+"F0.wireOp",EDGE,"E16.111.4"),sQuery(id+"F0.wireOp",EDGE,"E16.112.0"),sQuery(id+"F0.wireOp",EDGE,"E16.112.1"),sQuery(id+"F0.wireOp",EDGE,"E16.112.2"),sQuery(id+"F0.wireOp",EDGE,"E16.112.3"),sQuery(id+"F0.wireOp",EDGE,"E16.112.4"),sQuery(id+"F0.wireOp",EDGE,"E16.113.0"),sQuery(id+"F0.wireOp",EDGE,"E16.113.1"),sQuery(id+"F0.wireOp",EDGE,"E16.113.2"),sQuery(id+"F0.wireOp",EDGE,"E16.113.3"),sQuery(id+"F0.wireOp",EDGE,"E16.113.4"),sQuery(id+"F0.wireOp",EDGE,"E16.114.0"),sQuery(id+"F0.wireOp",EDGE,"E16.114.1"),sQuery(id+"F0.wireOp",EDGE,"E16.114.2"),sQuery(id+"F0.wireOp",EDGE,"E16.114.3"),sQuery(id+"F0.wireOp",EDGE,"E16.114.4"),sQuery(id+"F0.wireOp",EDGE,"E16.115.0"),sQuery(id+"F0.wireOp",EDGE,"E16.115.1"),sQuery(id+"F0.wireOp",EDGE,"E16.115.2"),sQuery(id+"F0.wireOp",EDGE,"E16.115.3"),sQuery(id+"F0.wireOp",EDGE,"E16.115.4"),sQuery(id+"F0.wireOp",EDGE,"E16.116.0"),sQuery(id+"F0.wireOp",EDGE,"E16.116.1"),sQuery(id+"F0.wireOp",EDGE,"E16.116.2"),sQuery(id+"F0.wireOp",EDGE,"E16.116.3"),sQuery(id+"F0.wireOp",EDGE,"E16.116.4"),sQuery(id+"F0.wireOp",EDGE,"E16.117.0"),sQuery(id+"F0.wireOp",EDGE,"E16.117.1"),sQuery(id+"F0.wireOp",EDGE,"E16.117.2"),sQuery(id+"F0.wireOp",EDGE,"E16.117.3"),sQuery(id+"F0.wireOp",EDGE,"E16.117.4"),sQuery(id+"F0.wireOp",EDGE,"E16.118.0"),sQuery(id+"F0.wireOp",EDGE,"E16.118.1"),sQuery(id+"F0.wireOp",EDGE,"E16.118.2"),sQuery(id+"F0.wireOp",EDGE,"E16.118.3"),sQuery(id+"F0.wireOp",EDGE,"E16.118.4"),sQuery(id+"F0.wireOp",EDGE,"E16.119.0"),sQuery(id+"F0.wireOp",EDGE,"E16.119.1"),sQuery(id+"F0.wireOp",EDGE,"E16.119.2"),sQuery(id+"F0.wireOp",EDGE,"E16.119.3"),sQuery(id+"F0.wireOp",EDGE,"E16.119.4"),sQuery(id+"F0.wireOp",EDGE,"E16.120.0"),sQuery(id+"F0.wireOp",EDGE,"E16.120.1"),sQuery(id+"F0.wireOp",EDGE,"E16.120.2"),sQuery(id+"F0.wireOp",EDGE,"E16.120.3"),sQuery(id+"F0.wireOp",EDGE,"E16.120.4"),sQuery(id+"F0.wireOp",EDGE,"E16.121.0"),sQuery(id+"F0.wireOp",EDGE,"E16.121.1"),sQuery(id+"F0.wireOp",EDGE,"E16.121.2"),sQuery(id+"F0.wireOp",EDGE,"E16.121.3"),sQuery(id+"F0.wireOp",EDGE,"E16.121.4"),sQuery(id+"F0.wireOp",EDGE,"E16.122.0"),sQuery(id+"F0.wireOp",EDGE,"E16.122.1"),sQuery(id+"F0.wireOp",EDGE,"E16.122.2"),sQuery(id+"F0.wireOp",EDGE,"E16.122.3"),sQuery(id+"F0.wireOp",EDGE,"E16.122.4"),sQuery(id+"F0.wireOp",EDGE,"E16.123.0"),sQuery(id+"F0.wireOp",EDGE,"E16.123.1"),sQuery(id+"F0.wireOp",EDGE,"E16.123.2"),sQuery(id+"F0.wireOp",EDGE,"E16.123.3"),sQuery(id+"F0.wireOp",EDGE,"E16.123.4"),sQuery(id+"F0.wireOp",EDGE,"E16.124.0"),sQuery(id+"F0.wireOp",EDGE,"E16.124.1"),sQuery(id+"F0.wireOp",EDGE,"E16.124.2"),sQuery(id+"F0.wireOp",EDGE,"E16.124.3"),sQuery(id+"F0.wireOp",EDGE,"E16.124.4"),sQuery(id+"F0.wireOp",EDGE,"E16.125.0"),sQuery(id+"F0.wireOp",EDGE,"E16.125.1"),sQuery(id+"F0.wireOp",EDGE,"E16.125.2"),sQuery(id+"F0.wireOp",EDGE,"E16.125.3"),sQuery(id+"F0.wireOp",EDGE,"E16.125.4"),sQuery(id+"F0.wireOp",EDGE,"E16.126.0"),sQuery(id+"F0.wireOp",EDGE,"E16.126.1"),sQuery(id+"F0.wireOp",EDGE,"E16.126.2"),sQuery(id+"F0.wireOp",EDGE,"E16.126.3"),sQuery(id+"F0.wireOp",EDGE,"E16.126.4"),sQuery(id+"F0.wireOp",EDGE,"E16.127.0"),sQuery(id+"F0.wireOp",EDGE,"E16.127.1"),sQuery(id+"F0.wireOp",EDGE,"E16.127.2"),sQuery(id+"F0.wireOp",EDGE,"E16.127.3"),sQuery(id+"F0.wireOp",EDGE,"E16.127.4"),sQuery(id+"F0.wireOp",EDGE,"E16.128.0"),sQuery(id+"F0.wireOp",EDGE,"E16.128.1"),sQuery(id+"F0.wireOp",EDGE,"E16.128.2"),sQuery(id+"F0.wireOp",EDGE,"E16.128.3"),sQuery(id+"F0.wireOp",EDGE,"E16.128.4"),sQuery(id+"F0.wireOp",EDGE,"E16.129.0"),sQuery(id+"F0.wireOp",EDGE,"E16.129.1"),sQuery(id+"F0.wireOp",EDGE,"E16.129.2"),sQuery(id+"F0.wireOp",EDGE,"E16.129.3"),sQuery(id+"F0.wireOp",EDGE,"E16.129.4"),sQuery(id+"F0.wireOp",EDGE,"E16.130.0"),sQuery(id+"F0.wireOp",EDGE,"E16.130.1"),sQuery(id+"F0.wireOp",EDGE,"E16.130.2"),sQuery(id+"F0.wireOp",EDGE,"E16.130.3"),sQuery(id+"F0.wireOp",EDGE,"E16.130.4"),sQuery(id+"F0.wireOp",EDGE,"E16.131.0"),sQuery(id+"F0.wireOp",EDGE,"E16.131.1"),sQuery(id+"F0.wireOp",EDGE,"E16.131.2"),sQuery(id+"F0.wireOp",EDGE,"E16.131.3"),sQuery(id+"F0.wireOp",EDGE,"E16.131.4"),sQuery(id+"F0.wireOp",EDGE,"E16.132.0"),sQuery(id+"F0.wireOp",EDGE,"E16.132.1"),sQuery(id+"F0.wireOp",EDGE,"E16.132.2"),sQuery(id+"F0.wireOp",EDGE,"E16.132.3"),sQuery(id+"F0.wireOp",EDGE,"E16.132.4"),sQuery(id+"F0.wireOp",EDGE,"E16.133.0"),sQuery(id+"F0.wireOp",EDGE,"E16.133.1"),sQuery(id+"F0.wireOp",EDGE,"E16.133.2"),sQuery(id+"F0.wireOp",EDGE,"E16.133.3"),sQuery(id+"F0.wireOp",EDGE,"E16.133.4"),sQuery(id+"F0.wireOp",EDGE,"E16.134.0"),sQuery(id+"F0.wireOp",EDGE,"E16.134.1"),sQuery(id+"F0.wireOp",EDGE,"E16.134.2"),sQuery(id+"F0.wireOp",EDGE,"E16.134.3"),sQuery(id+"F0.wireOp",EDGE,"E16.134.4"),sQuery(id+"F0.wireOp",EDGE,"E16.135.0"),sQuery(id+"F0.wireOp",EDGE,"E16.135.1"),sQuery(id+"F0.wireOp",EDGE,"E16.135.2"),sQuery(id+"F0.wireOp",EDGE,"E16.135.3"),sQuery(id+"F0.wireOp",EDGE,"E16.135.4"),sQuery(id+"F0.wireOp",EDGE,"E16.136.0"),sQuery(id+"F0.wireOp",EDGE,"E16.136.1"),sQuery(id+"F0.wireOp",EDGE,"E16.136.2"),sQuery(id+"F0.wireOp",EDGE,"E16.136.3"),sQuery(id+"F0.wireOp",EDGE,"E16.136.4"),sQuery(id+"F0.wireOp",EDGE,"E16.137.0"),sQuery(id+"F0.wireOp",EDGE,"E16.137.1"),sQuery(id+"F0.wireOp",EDGE,"E16.137.2"),sQuery(id+"F0.wireOp",EDGE,"E16.137.3"),sQuery(id+"F0.wireOp",EDGE,"E16.137.4"),sQuery(id+"F0.wireOp",EDGE,"E16.138.0"),sQuery(id+"F0.wireOp",EDGE,"E16.138.1"),sQuery(id+"F0.wireOp",EDGE,"E16.138.2"),sQuery(id+"F0.wireOp",EDGE,"E16.138.3"),sQuery(id+"F0.wireOp",EDGE,"E16.138.4"),sQuery(id+"F0.wireOp",EDGE,"E16.139.0"),sQuery(id+"F0.wireOp",EDGE,"E16.139.1"),sQuery(id+"F0.wireOp",EDGE,"E16.139.2"),sQuery(id+"F0.wireOp",EDGE,"E16.139.3"),sQuery(id+"F0.wireOp",EDGE,"E16.139.4"),sQuery(id+"F0.wireOp",EDGE,"E16.140.0"),sQuery(id+"F0.wireOp",EDGE,"E16.140.1"),sQuery(id+"F0.wireOp",EDGE,"E16.140.2"),sQuery(id+"F0.wireOp",EDGE,"E16.140.3"),sQuery(id+"F0.wireOp",EDGE,"E16.140.4"),sQuery(id+"F0.wireOp",EDGE,"E16.141.0"),sQuery(id+"F0.wireOp",EDGE,"E16.141.1"),sQuery(id+"F0.wireOp",EDGE,"E16.141.2"),sQuery(id+"F0.wireOp",EDGE,"E16.141.3"),sQuery(id+"F0.wireOp",EDGE,"E16.141.4"),sQuery(id+"F0.wireOp",EDGE,"E16.142.0"),sQuery(id+"F0.wireOp",EDGE,"E16.142.1"),sQuery(id+"F0.wireOp",EDGE,"E16.142.2"),sQuery(id+"F0.wireOp",EDGE,"E16.142.3"),sQuery(id+"F0.wireOp",EDGE,"E16.142.4"),sQuery(id+"F0.wireOp",EDGE,"E16.143.0"),sQuery(id+"F0.wireOp",EDGE,"E16.143.1"),sQuery(id+"F0.wireOp",EDGE,"E16.143.2"),sQuery(id+"F0.wireOp",EDGE,"E16.143.3"),sQuery(id+"F0.wireOp",EDGE,"E16.143.4"),sQuery(id+"F0.wireOp",EDGE,"E16.144.0"),sQuery(id+"F0.wireOp",EDGE,"E16.144.1"),sQuery(id+"F0.wireOp",EDGE,"E16.144.2"),sQuery(id+"F0.wireOp",EDGE,"E16.144.3"),sQuery(id+"F0.wireOp",EDGE,"E16.144.4"),sQuery(id+"F0.wireOp",EDGE,"E16.145.0"),sQuery(id+"F0.wireOp",EDGE,"E16.145.1"),sQuery(id+"F0.wireOp",EDGE,"E16.145.2"),sQuery(id+"F0.wireOp",EDGE,"E16.145.3"),sQuery(id+"F0.wireOp",EDGE,"E16.145.4"),sQuery(id+"F0.wireOp",EDGE,"E16.146.0"),sQuery(id+"F0.wireOp",EDGE,"E16.146.1"),sQuery(id+"F0.wireOp",EDGE,"E16.146.2"),sQuery(id+"F0.wireOp",EDGE,"E16.146.3"),sQuery(id+"F0.wireOp",EDGE,"E16.146.4"),sQuery(id+"F0.wireOp",EDGE,"E16.147.0"),sQuery(id+"F0.wireOp",EDGE,"E16.147.1"),sQuery(id+"F0.wireOp",EDGE,"E16.147.2"),sQuery(id+"F0.wireOp",EDGE,"E16.147.3"),sQuery(id+"F0.wireOp",EDGE,"E16.147.4"),sQuery(id+"F0.wireOp",EDGE,"E16.148.0"),sQuery(id+"F0.wireOp",EDGE,"E16.148.1"),sQuery(id+"F0.wireOp",EDGE,"E16.148.2"),sQuery(id+"F0.wireOp",EDGE,"E16.148.3"),sQuery(id+"F0.wireOp",EDGE,"E16.148.4"),sQuery(id+"F0.wireOp",EDGE,"E16.149.0"),sQuery(id+"F0.wireOp",EDGE,"E16.149.1"),sQuery(id+"F0.wireOp",EDGE,"E16.149.2"),sQuery(id+"F0.wireOp",EDGE,"E16.149.3"),sQuery(id+"F0.wireOp",EDGE,"E16.149.4"),sQuery(id+"F0.wireOp",EDGE,"E16.150.0"),sQuery(id+"F0.wireOp",EDGE,"E16.150.1"),sQuery(id+"F0.wireOp",EDGE,"E16.150.2"),sQuery(id+"F0.wireOp",EDGE,"E16.150.3"),sQuery(id+"F0.wireOp",EDGE,"E16.150.4"),sQuery(id+"F0.wireOp",EDGE,"E16.151.0"),sQuery(id+"F0.wireOp",EDGE,"E16.151.1"),sQuery(id+"F0.wireOp",EDGE,"E16.151.2"),sQuery(id+"F0.wireOp",EDGE,"E16.151.3"),sQuery(id+"F0.wireOp",EDGE,"E16.151.4"),sQuery(id+"F0.wireOp",EDGE,"E16.152.0"),sQuery(id+"F0.wireOp",EDGE,"E16.152.1"),sQuery(id+"F0.wireOp",EDGE,"E16.152.2"),sQuery(id+"F0.wireOp",EDGE,"E16.152.3"),sQuery(id+"F0.wireOp",EDGE,"E16.152.4"),sQuery(id+"F0.wireOp",EDGE,"E16.153.0"),sQuery(id+"F0.wireOp",EDGE,"E16.153.1"),sQuery(id+"F0.wireOp",EDGE,"E16.153.2"),sQuery(id+"F0.wireOp",EDGE,"E16.153.3"),sQuery(id+"F0.wireOp",EDGE,"E16.153.4"),sQuery(id+"F0.wireOp",EDGE,"E16.154.0"),sQuery(id+"F0.wireOp",EDGE,"E16.154.1"),sQuery(id+"F0.wireOp",EDGE,"E16.154.2"),sQuery(id+"F0.wireOp",EDGE,"E16.154.3"),sQuery(id+"F0.wireOp",EDGE,"E16.154.4"),sQuery(id+"F0.wireOp",EDGE,"E16.155.0"),sQuery(id+"F0.wireOp",EDGE,"E16.155.1"),sQuery(id+"F0.wireOp",EDGE,"E16.155.2"),sQuery(id+"F0.wireOp",EDGE,"E16.155.3"),sQuery(id+"F0.wireOp",EDGE,"E16.155.4"),sQuery(id+"F0.wireOp",EDGE,"E16.156.0"),sQuery(id+"F0.wireOp",EDGE,"E16.156.1"),sQuery(id+"F0.wireOp",EDGE,"E16.156.2"),sQuery(id+"F0.wireOp",EDGE,"E16.156.3"),sQuery(id+"F0.wireOp",EDGE,"E16.156.4"),sQuery(id+"F0.wireOp",EDGE,"E16.157.0"),sQuery(id+"F0.wireOp",EDGE,"E16.157.1"),sQuery(id+"F0.wireOp",EDGE,"E16.157.2"),sQuery(id+"F0.wireOp",EDGE,"E16.157.3"),sQuery(id+"F0.wireOp",EDGE,"E16.157.4"),sQuery(id+"F0.wireOp",EDGE,"E16.158.0"),sQuery(id+"F0.wireOp",EDGE,"E16.158.1"),sQuery(id+"F0.wireOp",EDGE,"E16.158.2"),sQuery(id+"F0.wireOp",EDGE,"E16.158.3"),sQuery(id+"F0.wireOp",EDGE,"E16.158.4"),sQuery(id+"F0.wireOp",EDGE,"E16.159.0"),sQuery(id+"F0.wireOp",EDGE,"E16.159.1"),sQuery(id+"F0.wireOp",EDGE,"E16.159.2"),sQuery(id+"F0.wireOp",EDGE,"E16.159.3"),sQuery(id+"F0.wireOp",EDGE,"E16.159.4"),sQuery(id+"F0.wireOp",EDGE,"E16.160.0"),sQuery(id+"F0.wireOp",EDGE,"E16.160.1"),sQuery(id+"F0.wireOp",EDGE,"E16.160.2"),sQuery(id+"F0.wireOp",EDGE,"E16.160.3"),sQuery(id+"F0.wireOp",EDGE,"E16.160.4"),sQuery(id+"F0.wireOp",EDGE,"E16.161.0"),sQuery(id+"F0.wireOp",EDGE,"E16.161.1"),sQuery(id+"F0.wireOp",EDGE,"E16.161.2"),sQuery(id+"F0.wireOp",EDGE,"E16.161.3"),sQuery(id+"F0.wireOp",EDGE,"E16.161.4"),sQuery(id+"F0.wireOp",EDGE,"E16.162.0"),sQuery(id+"F0.wireOp",EDGE,"E16.162.1"),sQuery(id+"F0.wireOp",EDGE,"E16.162.2"),sQuery(id+"F0.wireOp",EDGE,"E16.162.3"),sQuery(id+"F0.wireOp",EDGE,"E16.162.4"),sQuery(id+"F0.wireOp",EDGE,"E16.163.0"),sQuery(id+"F0.wireOp",EDGE,"E16.163.1"),sQuery(id+"F0.wireOp",EDGE,"E16.163.2"),sQuery(id+"F0.wireOp",EDGE,"E16.163.3"),sQuery(id+"F0.wireOp",EDGE,"E16.163.4"),sQuery(id+"F0.wireOp",EDGE,"E16.164.0"),sQuery(id+"F0.wireOp",EDGE,"E16.164.1"),sQuery(id+"F0.wireOp",EDGE,"E16.164.2"),sQuery(id+"F0.wireOp",EDGE,"E16.164.3"),sQuery(id+"F0.wireOp",EDGE,"E16.164.4"),sQuery(id+"F0.wireOp",EDGE,"E16.165.0"),sQuery(id+"F0.wireOp",EDGE,"E16.165.1"),sQuery(id+"F0.wireOp",EDGE,"E16.165.2"),sQuery(id+"F0.wireOp",EDGE,"E16.165.3"),sQuery(id+"F0.wireOp",EDGE,"E16.165.4"),sQuery(id+"F0.wireOp",EDGE,"E16.166.0"),sQuery(id+"F0.wireOp",EDGE,"E16.166.1"),sQuery(id+"F0.wireOp",EDGE,"E16.166.2"),sQuery(id+"F0.wireOp",EDGE,"E16.166.3"),sQuery(id+"F0.wireOp",EDGE,"E16.166.4"),sQuery(id+"F0.wireOp",EDGE,"E16.167.0"),sQuery(id+"F0.wireOp",EDGE,"E16.167.1"),sQuery(id+"F0.wireOp",EDGE,"E16.167.2"),sQuery(id+"F0.wireOp",EDGE,"E16.167.3"),sQuery(id+"F0.wireOp",EDGE,"E16.167.4"),sQuery(id+"F0.wireOp",EDGE,"E16.168.0"),sQuery(id+"F0.wireOp",EDGE,"E16.168.1"),sQuery(id+"F0.wireOp",EDGE,"E16.168.2"),sQuery(id+"F0.wireOp",EDGE,"E16.168.3"),sQuery(id+"F0.wireOp",EDGE,"E16.168.4"),sQuery(id+"F0.wireOp",EDGE,"E16.169.0"),sQuery(id+"F0.wireOp",EDGE,"E16.169.1"),sQuery(id+"F0.wireOp",EDGE,"E16.169.2"),sQuery(id+"F0.wireOp",EDGE,"E16.169.3"),sQuery(id+"F0.wireOp",EDGE,"E16.169.4"),sQuery(id+"F0.wireOp",EDGE,"E16.170.0"),sQuery(id+"F0.wireOp",EDGE,"E16.170.1"),sQuery(id+"F0.wireOp",EDGE,"E16.170.2"),sQuery(id+"F0.wireOp",EDGE,"E16.170.3"),sQuery(id+"F0.wireOp",EDGE,"E16.170.4"),sQuery(id+"F0.wireOp",EDGE,"E16.171.0"),sQuery(id+"F0.wireOp",EDGE,"E16.171.1"),sQuery(id+"F0.wireOp",EDGE,"E16.171.2"),sQuery(id+"F0.wireOp",EDGE,"E16.171.3"),sQuery(id+"F0.wireOp",EDGE,"E16.171.4"),sQuery(id+"F0.wireOp",EDGE,"E16.172.0"),sQuery(id+"F0.wireOp",EDGE,"E16.172.1"),sQuery(id+"F0.wireOp",EDGE,"E16.172.2"),sQuery(id+"F0.wireOp",EDGE,"E16.172.3"),sQuery(id+"F0.wireOp",EDGE,"E16.172.4"),sQuery(id+"F0.wireOp",EDGE,"E16.173.0"),sQuery(id+"F0.wireOp",EDGE,"E16.173.1"),sQuery(id+"F0.wireOp",EDGE,"E16.173.2"),sQuery(id+"F0.wireOp",EDGE,"E16.173.3"),sQuery(id+"F0.wireOp",EDGE,"E16.173.4"),sQuery(id+"F0.wireOp",EDGE,"E16.174.0"),sQuery(id+"F0.wireOp",EDGE,"E16.174.1"),sQuery(id+"F0.wireOp",EDGE,"E16.174.2"),sQuery(id+"F0.wireOp",EDGE,"E16.174.3"),sQuery(id+"F0.wireOp",EDGE,"E16.174.4"),sQuery(id+"F0.wireOp",EDGE,"E16.175.0"),sQuery(id+"F0.wireOp",EDGE,"E16.175.1"),sQuery(id+"F0.wireOp",EDGE,"E16.175.2"),sQuery(id+"F0.wireOp",EDGE,"E16.175.3"),sQuery(id+"F0.wireOp",EDGE,"E16.175.4"),sQuery(id+"F0.wireOp",EDGE,"E16.176.0"),sQuery(id+"F0.wireOp",EDGE,"E16.176.1"),sQuery(id+"F0.wireOp",EDGE,"E16.176.2"),sQuery(id+"F0.wireOp",EDGE,"E16.176.3"),sQuery(id+"F0.wireOp",EDGE,"E16.176.4"),sQuery(id+"F0.wireOp",EDGE,"E16.177.0"),sQuery(id+"F0.wireOp",EDGE,"E16.177.1"),sQuery(id+"F0.wireOp",EDGE,"E16.177.2"),sQuery(id+"F0.wireOp",EDGE,"E16.177.3"),sQuery(id+"F0.wireOp",EDGE,"E16.177.4"),sQuery(id+"F0.wireOp",EDGE,"E16.178.0"),sQuery(id+"F0.wireOp",EDGE,"E16.178.1"),sQuery(id+"F0.wireOp",EDGE,"E16.178.2"),sQuery(id+"F0.wireOp",EDGE,"E16.178.3"),sQuery(id+"F0.wireOp",EDGE,"E16.178.4"),sQuery(id+"F0.wireOp",EDGE,"E16.179.0"),sQuery(id+"F0.wireOp",EDGE,"E16.179.1"),sQuery(id+"F0.wireOp",EDGE,"E16.179.2"),sQuery(id+"F0.wireOp",EDGE,"E16.179.3"),sQuery(id+"F0.wireOp",EDGE,"E16.179.4"),sQuery(id+"F0.wireOp",EDGE,"E16.180.0"),sQuery(id+"F0.wireOp",EDGE,"E16.180.1"),sQuery(id+"F0.wireOp",EDGE,"E16.180.2"),sQuery(id+"F0.wireOp",EDGE,"E16.180.3"),sQuery(id+"F0.wireOp",EDGE,"E16.180.4"),sQuery(id+"F0.wireOp",EDGE,"E16.181.0"),sQuery(id+"F0.wireOp",EDGE,"E16.181.1"),sQuery(id+"F0.wireOp",EDGE,"E16.181.2"),sQuery(id+"F0.wireOp",EDGE,"E16.181.3"),sQuery(id+"F0.wireOp",EDGE,"E16.181.4"),sQuery(id+"F0.wireOp",EDGE,"E16.182.0"),sQuery(id+"F0.wireOp",EDGE,"E16.182.1"),sQuery(id+"F0.wireOp",EDGE,"E16.182.2"),sQuery(id+"F0.wireOp",EDGE,"E16.182.3"),sQuery(id+"F0.wireOp",EDGE,"E16.182.4"),sQuery(id+"F0.wireOp",EDGE,"E16.183.0"),sQuery(id+"F0.wireOp",EDGE,"E16.183.1"),sQuery(id+"F0.wireOp",EDGE,"E16.183.2"),sQuery(id+"F0.wireOp",EDGE,"E16.183.3"),sQuery(id+"F0.wireOp",EDGE,"E16.183.4"),sQuery(id+"F0.wireOp",EDGE,"E16.184.0"),sQuery(id+"F0.wireOp",EDGE,"E16.184.1"),sQuery(id+"F0.wireOp",EDGE,"E16.184.2"),sQuery(id+"F0.wireOp",EDGE,"E16.184.3"),sQuery(id+"F0.wireOp",EDGE,"E16.184.4"),sQuery(id+"F0.wireOp",EDGE,"E16.185.0"),sQuery(id+"F0.wireOp",EDGE,"E16.185.1"),sQuery(id+"F0.wireOp",EDGE,"E16.185.2"),sQuery(id+"F0.wireOp",EDGE,"E16.185.3"),sQuery(id+"F0.wireOp",EDGE,"E16.185.4"),sQuery(id+"F0.wireOp",EDGE,"E16.186.0"),sQuery(id+"F0.wireOp",EDGE,"E16.186.1"),sQuery(id+"F0.wireOp",EDGE,"E16.186.2"),sQuery(id+"F0.wireOp",EDGE,"E16.186.3"),sQuery(id+"F0.wireOp",EDGE,"E16.186.4"),sQuery(id+"F0.wireOp",EDGE,"E16.187.0"),sQuery(id+"F0.wireOp",EDGE,"E16.187.1"),sQuery(id+"F0.wireOp",EDGE,"E16.187.2"),sQuery(id+"F0.wireOp",EDGE,"E16.187.3"),sQuery(id+"F0.wireOp",EDGE,"E16.187.4"),sQuery(id+"F0.wireOp",EDGE,"E16.188.0"),sQuery(id+"F0.wireOp",EDGE,"E16.188.1"),sQuery(id+"F0.wireOp",EDGE,"E16.188.2"),sQuery(id+"F0.wireOp",EDGE,"E16.188.3"),sQuery(id+"F0.wireOp",EDGE,"E16.188.4"),sQuery(id+"F0.wireOp",EDGE,"E16.189.0"),sQuery(id+"F0.wireOp",EDGE,"E16.189.1"),sQuery(id+"F0.wireOp",EDGE,"E16.189.2"),sQuery(id+"F0.wireOp",EDGE,"E16.189.3"),sQuery(id+"F0.wireOp",EDGE,"E16.189.4"),sQuery(id+"F0.wireOp",EDGE,"E16.190.0"),sQuery(id+"F0.wireOp",EDGE,"E16.190.1"),sQuery(id+"F0.wireOp",EDGE,"E16.190.2"),sQuery(id+"F0.wireOp",EDGE,"E16.190.3"),sQuery(id+"F0.wireOp",EDGE,"E16.190.4"),sQuery(id+"F0.wireOp",EDGE,"E16.191.0"),sQuery(id+"F0.wireOp",EDGE,"E16.191.1"),sQuery(id+"F0.wireOp",EDGE,"E16.191.2"),sQuery(id+"F0.wireOp",EDGE,"E16.191.3"),sQuery(id+"F0.wireOp",EDGE,"E16.191.4")])]});
            hole(context, id + "F6", {"style" : HoleStyle.C_SINK, "endStyle" : HoleEndStyle.THROUGH, "standardTappedOrClearance" : lookupTablePath({ "fit" : "Normal", "standard" : "ISO", "size" : "M4", "type" : "Clearance" }), "standardBlindInLast" : lookupTablePath({ "fit" : "Standard", "standard" : "ISO", "size" : "M4", "type" : "Clearance" }), "holeDiameter" : 4.4 * mm, "cSinkDiameter" : 8.96 * mm, "cSinkAngle" : 90 * degree, "majorDiameter" : 5 * mm, "isTappedThrough" : true, "tappedDepth" : 12 * mm, "tapClearance" : 3, "startFromSketch" : true, "locations" : qUnion([Q0]), "scope" : qUnion([Q1])});
        }
        {
            var Q0;
            Q0=makeQuery(id+"FnGEPf5ERnqVvQ3_1.1.F4.boolean.opBoolean","SPLIT",EDGE,{"disambiguationData":[OD(1.0)],"derivedFrom":makeQuery(id+"F1.opExtrude","CAP_EDGE",EDGE,{"disambiguationData":[OSD([sQuery(id+"F0.wireOp",EDGE,"E0")])],"isStart":true})});
            var Q1;
            Q1=makeQuery(id+"FnGEPf5ERnqVvQ3_1.1.F4.opExtrude","CAP_EDGE",EDGE,{"disambiguationData":[OSD([sQuery(id+"F3.wireOp",EDGE,"E23")])],"isStart":false});
            var Q2;
            {var subQ0=sQuery(id+"F3.wireOp",EDGE,"E23");var subQ2=sQuery(id+"F0.wireOp",EDGE,"E0");Q2=makeQuery(id+"FnGEPf5ERnqVvQ3_1.2.F4.boolean.opBoolean","SPLIT",EDGE,{"disambiguationData":[TD([makeQuery(id+"FnGEPf5ERnqVvQ3_1.1.F4.opExtrude","SWEPT_FACE",FACE,{"disambiguationData":[OSD([subQ0])]})])],"derivedFrom":makeQuery(id+"FnGEPf5ERnqVvQ3_1.1.F4.boolean.opBoolean","SPLIT",EDGE,{"disambiguationData":[OD(0.0)],"derivedFrom":makeQuery(id+"F1.opExtrude","CAP_EDGE",EDGE,{"disambiguationData":[OSD([subQ2])],"isStart":true})})});}
            var Q3;
            Q3=makeQuery(id+"FnGEPf5ERnqVvQ3_1.2.F4.opExtrude","CAP_EDGE",EDGE,{"disambiguationData":[OSD([sQuery(id+"F3.wireOp",EDGE,"E23")])],"isStart":false});
            var Q4;
            {var subQ0=sQuery(id+"F3.wireOp",EDGE,"E23");var subQ4=sQuery(id+"F0.wireOp",EDGE,"E0");var subQ8=makeQuery(id+"FnGEPf5ERnqVvQ3_1.2.F4.opExtrude","SWEPT_FACE",FACE,{"disambiguationData":[OSD([subQ0])]});Q4=makeQuery(id+"FnGEPf5ERnqVvQ3_1.3.F4.boolean.opBoolean","SPLIT",EDGE,{"disambiguationData":[TD([subQ8])],"derivedFrom":makeQuery(id+"FnGEPf5ERnqVvQ3_1.2.F4.boolean.opBoolean","SPLIT",EDGE,{"disambiguationData":[TD([makeQuery(id+"F4.opExtrude","SWEPT_FACE",FACE,{"disambiguationData":[OSD([subQ0])]})])],"derivedFrom":makeQuery(id+"FnGEPf5ERnqVvQ3_1.1.F4.boolean.opBoolean","SPLIT",EDGE,{"disambiguationData":[OD(0.0)],"derivedFrom":makeQuery(id+"F1.opExtrude","CAP_EDGE",EDGE,{"disambiguationData":[OSD([subQ4])],"isStart":true})})})});}
            var Q5;
            Q5=makeQuery(id+"FnGEPf5ERnqVvQ3_1.3.F4.opExtrude","CAP_EDGE",EDGE,{"disambiguationData":[OSD([sQuery(id+"F3.wireOp",EDGE,"E23")])],"isStart":false});
            var Q6;
            {var subQ0=sQuery(id+"F3.wireOp",EDGE,"E23");var subQ4=sQuery(id+"F0.wireOp",EDGE,"E0");var subQ9=makeQuery(id+"FnGEPf5ERnqVvQ3_1.3.F4.opExtrude","SWEPT_FACE",FACE,{"disambiguationData":[OSD([subQ0])]});var subQ10=makeQuery(id+"F4.opExtrude","SWEPT_FACE",FACE,{"disambiguationData":[OSD([subQ0])]});Q6=makeQuery(id+"FnGEPf5ERnqVvQ3_1.4.F4.boolean.opBoolean","SPLIT",EDGE,{"disambiguationData":[TD([subQ9])],"derivedFrom":makeQuery(id+"FnGEPf5ERnqVvQ3_1.3.F4.boolean.opBoolean","SPLIT",EDGE,{"disambiguationData":[TD([subQ10])],"derivedFrom":makeQuery(id+"FnGEPf5ERnqVvQ3_1.2.F4.boolean.opBoolean","SPLIT",EDGE,{"disambiguationData":[TD([subQ10])],"derivedFrom":makeQuery(id+"FnGEPf5ERnqVvQ3_1.1.F4.boolean.opBoolean","SPLIT",EDGE,{"disambiguationData":[OD(0.0)],"derivedFrom":makeQuery(id+"F1.opExtrude","CAP_EDGE",EDGE,{"disambiguationData":[OSD([subQ4])],"isStart":true})})})})});}
            var Q7;
            Q7=makeQuery(id+"FnGEPf5ERnqVvQ3_1.4.F4.opExtrude","CAP_EDGE",EDGE,{"disambiguationData":[OSD([sQuery(id+"F3.wireOp",EDGE,"E23")])],"isStart":false});
            var Q8;
            {var subQ0=sQuery(id+"F3.wireOp",EDGE,"E23");var subQ4=sQuery(id+"F0.wireOp",EDGE,"E0");var subQ6=makeQuery(id+"FnGEPf5ERnqVvQ3_1.4.F4.opExtrude","SWEPT_FACE",FACE,{"disambiguationData":[OSD([subQ0])]});var subQ11=makeQuery(id+"F4.opExtrude","SWEPT_FACE",FACE,{"disambiguationData":[OSD([subQ0])]});Q8=makeQuery(id+"FnGEPf5ERnqVvQ3_1.5.F4.boolean.opBoolean","SPLIT",EDGE,{"disambiguationData":[TD([subQ6])],"derivedFrom":makeQuery(id+"FnGEPf5ERnqVvQ3_1.4.F4.boolean.opBoolean","SPLIT",EDGE,{"disambiguationData":[TD([subQ11])],"derivedFrom":makeQuery(id+"FnGEPf5ERnqVvQ3_1.3.F4.boolean.opBoolean","SPLIT",EDGE,{"disambiguationData":[TD([subQ11])],"derivedFrom":makeQuery(id+"FnGEPf5ERnqVvQ3_1.2.F4.boolean.opBoolean","SPLIT",EDGE,{"disambiguationData":[TD([subQ11])],"derivedFrom":makeQuery(id+"FnGEPf5ERnqVvQ3_1.1.F4.boolean.opBoolean","SPLIT",EDGE,{"disambiguationData":[OD(0.0)],"derivedFrom":makeQuery(id+"F1.opExtrude","CAP_EDGE",EDGE,{"disambiguationData":[OSD([subQ4])],"isStart":true})})})})})});}
            var Q9;
            Q9=makeQuery(id+"FnGEPf5ERnqVvQ3_1.5.F4.opExtrude","CAP_EDGE",EDGE,{"disambiguationData":[OSD([sQuery(id+"F3.wireOp",EDGE,"E23")])],"isStart":false});
            var Q10;
            {var subQ0=sQuery(id+"F3.wireOp",EDGE,"E23");var subQ6=sQuery(id+"F0.wireOp",EDGE,"E0");var subQ10=makeQuery(id+"FnGEPf5ERnqVvQ3_1.5.F4.opExtrude","SWEPT_FACE",FACE,{"disambiguationData":[OSD([subQ0])]});var subQ12=makeQuery(id+"F4.opExtrude","SWEPT_FACE",FACE,{"disambiguationData":[OSD([subQ0])]});Q10=makeQuery(id+"FnGEPf5ERnqVvQ3_1.6.F4.boolean.opBoolean","SPLIT",EDGE,{"disambiguationData":[TD([subQ10])],"derivedFrom":makeQuery(id+"FnGEPf5ERnqVvQ3_1.5.F4.boolean.opBoolean","SPLIT",EDGE,{"disambiguationData":[TD([subQ12])],"derivedFrom":makeQuery(id+"FnGEPf5ERnqVvQ3_1.4.F4.boolean.opBoolean","SPLIT",EDGE,{"disambiguationData":[TD([subQ12])],"derivedFrom":makeQuery(id+"FnGEPf5ERnqVvQ3_1.3.F4.boolean.opBoolean","SPLIT",EDGE,{"disambiguationData":[TD([subQ12])],"derivedFrom":makeQuery(id+"FnGEPf5ERnqVvQ3_1.2.F4.boolean.opBoolean","SPLIT",EDGE,{"disambiguationData":[TD([subQ12])],"derivedFrom":makeQuery(id+"FnGEPf5ERnqVvQ3_1.1.F4.boolean.opBoolean","SPLIT",EDGE,{"disambiguationData":[OD(0.0)],"derivedFrom":makeQuery(id+"F1.opExtrude","CAP_EDGE",EDGE,{"disambiguationData":[OSD([subQ6])],"isStart":true})})})})})})});}
            var Q11;
            Q11=makeQuery(id+"FnGEPf5ERnqVvQ3_1.6.F4.opExtrude","CAP_EDGE",EDGE,{"disambiguationData":[OSD([sQuery(id+"F3.wireOp",EDGE,"E23")])],"isStart":false});
            var Q12;
            {var subQ0=sQuery(id+"F3.wireOp",EDGE,"E23");var subQ6=makeQuery(id+"FnGEPf5ERnqVvQ3_1.6.F4.opExtrude","SWEPT_FACE",FACE,{"disambiguationData":[OSD([subQ0])]});var subQ8=sQuery(id+"F0.wireOp",EDGE,"E0");var subQ13=makeQuery(id+"F4.opExtrude","SWEPT_FACE",FACE,{"disambiguationData":[OSD([subQ0])]});Q12=makeQuery(id+"FnGEPf5ERnqVvQ3_1.7.F4.boolean.opBoolean","SPLIT",EDGE,{"disambiguationData":[TD([subQ6])],"derivedFrom":makeQuery(id+"FnGEPf5ERnqVvQ3_1.6.F4.boolean.opBoolean","SPLIT",EDGE,{"disambiguationData":[TD([subQ13])],"derivedFrom":makeQuery(id+"FnGEPf5ERnqVvQ3_1.5.F4.boolean.opBoolean","SPLIT",EDGE,{"disambiguationData":[TD([subQ13])],"derivedFrom":makeQuery(id+"FnGEPf5ERnqVvQ3_1.4.F4.boolean.opBoolean","SPLIT",EDGE,{"disambiguationData":[TD([subQ13])],"derivedFrom":makeQuery(id+"FnGEPf5ERnqVvQ3_1.3.F4.boolean.opBoolean","SPLIT",EDGE,{"disambiguationData":[TD([subQ13])],"derivedFrom":makeQuery(id+"FnGEPf5ERnqVvQ3_1.2.F4.boolean.opBoolean","SPLIT",EDGE,{"disambiguationData":[TD([subQ13])],"derivedFrom":makeQuery(id+"FnGEPf5ERnqVvQ3_1.1.F4.boolean.opBoolean","SPLIT",EDGE,{"disambiguationData":[OD(0.0)],"derivedFrom":makeQuery(id+"F1.opExtrude","CAP_EDGE",EDGE,{"disambiguationData":[OSD([subQ8])],"isStart":true})})})})})})})});}
            var Q13;
            {var subQ0=sQuery(id+"F3.wireOp",EDGE,"E23");var subQ8=sQuery(id+"F0.wireOp",EDGE,"E0");var subQ13=makeQuery(id+"FnGEPf5ERnqVvQ3_1.7.F4.opExtrude","SWEPT_FACE",FACE,{"disambiguationData":[OSD([subQ0])]});var subQ14=makeQuery(id+"F4.opExtrude","SWEPT_FACE",FACE,{"disambiguationData":[OSD([subQ0])]});Q13=makeQuery(id+"FnGEPf5ERnqVvQ3_1.8.F4.boolean.opBoolean","SPLIT",EDGE,{"disambiguationData":[TD([subQ13])],"derivedFrom":makeQuery(id+"FnGEPf5ERnqVvQ3_1.7.F4.boolean.opBoolean","SPLIT",EDGE,{"disambiguationData":[TD([subQ14])],"derivedFrom":makeQuery(id+"FnGEPf5ERnqVvQ3_1.6.F4.boolean.opBoolean","SPLIT",EDGE,{"disambiguationData":[TD([subQ14])],"derivedFrom":makeQuery(id+"FnGEPf5ERnqVvQ3_1.5.F4.boolean.opBoolean","SPLIT",EDGE,{"disambiguationData":[TD([subQ14])],"derivedFrom":makeQuery(id+"FnGEPf5ERnqVvQ3_1.4.F4.boolean.opBoolean","SPLIT",EDGE,{"disambiguationData":[TD([subQ14])],"derivedFrom":makeQuery(id+"FnGEPf5ERnqVvQ3_1.3.F4.boolean.opBoolean","SPLIT",EDGE,{"disambiguationData":[TD([subQ14])],"derivedFrom":makeQuery(id+"FnGEPf5ERnqVvQ3_1.2.F4.boolean.opBoolean","SPLIT",EDGE,{"disambiguationData":[TD([subQ14])],"derivedFrom":makeQuery(id+"FnGEPf5ERnqVvQ3_1.1.F4.boolean.opBoolean","SPLIT",EDGE,{"disambiguationData":[OD(0.0)],"derivedFrom":makeQuery(id+"F1.opExtrude","CAP_EDGE",EDGE,{"disambiguationData":[OSD([subQ8])],"isStart":true})})})})})})})})});}
            var Q14;
            Q14=makeQuery(id+"FnGEPf5ERnqVvQ3_1.7.F4.opExtrude","CAP_EDGE",EDGE,{"disambiguationData":[OSD([sQuery(id+"F3.wireOp",EDGE,"E23")])],"isStart":false});
            var Q15;
            Q15=makeQuery(id+"FnGEPf5ERnqVvQ3_1.8.F4.opExtrude","CAP_EDGE",EDGE,{"disambiguationData":[OSD([sQuery(id+"F3.wireOp",EDGE,"E23")])],"isStart":false});
            var Q16;
            {var subQ0=sQuery(id+"F3.wireOp",EDGE,"E23");var subQ8=sQuery(id+"F0.wireOp",EDGE,"E0");var subQ14=makeQuery(id+"FnGEPf5ERnqVvQ3_1.8.F4.opExtrude","SWEPT_FACE",FACE,{"disambiguationData":[OSD([subQ0])]});var subQ15=makeQuery(id+"F4.opExtrude","SWEPT_FACE",FACE,{"disambiguationData":[OSD([subQ0])]});Q16=makeQuery(id+"FnGEPf5ERnqVvQ3_1.9.F4.boolean.opBoolean","SPLIT",EDGE,{"disambiguationData":[TD([subQ14])],"derivedFrom":makeQuery(id+"FnGEPf5ERnqVvQ3_1.8.F4.boolean.opBoolean","SPLIT",EDGE,{"disambiguationData":[TD([subQ15])],"derivedFrom":makeQuery(id+"FnGEPf5ERnqVvQ3_1.7.F4.boolean.opBoolean","SPLIT",EDGE,{"disambiguationData":[TD([subQ15])],"derivedFrom":makeQuery(id+"FnGEPf5ERnqVvQ3_1.6.F4.boolean.opBoolean","SPLIT",EDGE,{"disambiguationData":[TD([subQ15])],"derivedFrom":makeQuery(id+"FnGEPf5ERnqVvQ3_1.5.F4.boolean.opBoolean","SPLIT",EDGE,{"disambiguationData":[TD([subQ15])],"derivedFrom":makeQuery(id+"FnGEPf5ERnqVvQ3_1.4.F4.boolean.opBoolean","SPLIT",EDGE,{"disambiguationData":[TD([subQ15])],"derivedFrom":makeQuery(id+"FnGEPf5ERnqVvQ3_1.3.F4.boolean.opBoolean","SPLIT",EDGE,{"disambiguationData":[TD([subQ15])],"derivedFrom":makeQuery(id+"FnGEPf5ERnqVvQ3_1.2.F4.boolean.opBoolean","SPLIT",EDGE,{"disambiguationData":[TD([subQ15])],"derivedFrom":makeQuery(id+"FnGEPf5ERnqVvQ3_1.1.F4.boolean.opBoolean","SPLIT",EDGE,{"disambiguationData":[OD(0.0)],"derivedFrom":makeQuery(id+"F1.opExtrude","CAP_EDGE",EDGE,{"disambiguationData":[OSD([subQ8])],"isStart":true})})})})})})})})})});}
            var Q17;
            Q17=makeQuery(id+"FnGEPf5ERnqVvQ3_1.9.F4.opExtrude","CAP_EDGE",EDGE,{"disambiguationData":[OSD([sQuery(id+"F3.wireOp",EDGE,"E23")])],"isStart":false});
            var Q18;
            {var subQ0=sQuery(id+"F3.wireOp",EDGE,"E23");var subQ8=sQuery(id+"F0.wireOp",EDGE,"E0");var subQ15=makeQuery(id+"FnGEPf5ERnqVvQ3_1.9.F4.opExtrude","SWEPT_FACE",FACE,{"disambiguationData":[OSD([subQ0])]});var subQ16=makeQuery(id+"F4.opExtrude","SWEPT_FACE",FACE,{"disambiguationData":[OSD([subQ0])]});Q18=makeQuery(id+"FnGEPf5ERnqVvQ3_1.10.F4.boolean.opBoolean","SPLIT",EDGE,{"disambiguationData":[TD([subQ15])],"derivedFrom":makeQuery(id+"FnGEPf5ERnqVvQ3_1.9.F4.boolean.opBoolean","SPLIT",EDGE,{"disambiguationData":[TD([subQ16])],"derivedFrom":makeQuery(id+"FnGEPf5ERnqVvQ3_1.8.F4.boolean.opBoolean","SPLIT",EDGE,{"disambiguationData":[TD([subQ16])],"derivedFrom":makeQuery(id+"FnGEPf5ERnqVvQ3_1.7.F4.boolean.opBoolean","SPLIT",EDGE,{"disambiguationData":[TD([subQ16])],"derivedFrom":makeQuery(id+"FnGEPf5ERnqVvQ3_1.6.F4.boolean.opBoolean","SPLIT",EDGE,{"disambiguationData":[TD([subQ16])],"derivedFrom":makeQuery(id+"FnGEPf5ERnqVvQ3_1.5.F4.boolean.opBoolean","SPLIT",EDGE,{"disambiguationData":[TD([subQ16])],"derivedFrom":makeQuery(id+"FnGEPf5ERnqVvQ3_1.4.F4.boolean.opBoolean","SPLIT",EDGE,{"disambiguationData":[TD([subQ16])],"derivedFrom":makeQuery(id+"FnGEPf5ERnqVvQ3_1.3.F4.boolean.opBoolean","SPLIT",EDGE,{"disambiguationData":[TD([subQ16])],"derivedFrom":makeQuery(id+"FnGEPf5ERnqVvQ3_1.2.F4.boolean.opBoolean","SPLIT",EDGE,{"disambiguationData":[TD([subQ16])],"derivedFrom":makeQuery(id+"FnGEPf5ERnqVvQ3_1.1.F4.boolean.opBoolean","SPLIT",EDGE,{"disambiguationData":[OD(0.0)],"derivedFrom":makeQuery(id+"F1.opExtrude","CAP_EDGE",EDGE,{"disambiguationData":[OSD([subQ8])],"isStart":true})})})})})})})})})})});}
            var Q19;
            Q19=makeQuery(id+"FnGEPf5ERnqVvQ3_1.10.F4.opExtrude","CAP_EDGE",EDGE,{"disambiguationData":[OSD([sQuery(id+"F3.wireOp",EDGE,"E23")])],"isStart":false});
            var Q20;
            {var subQ0=sQuery(id+"F3.wireOp",EDGE,"E23");var subQ8=sQuery(id+"F0.wireOp",EDGE,"E0");var subQ16=makeQuery(id+"FnGEPf5ERnqVvQ3_1.10.F4.opExtrude","SWEPT_FACE",FACE,{"disambiguationData":[OSD([subQ0])]});var subQ17=makeQuery(id+"F4.opExtrude","SWEPT_FACE",FACE,{"disambiguationData":[OSD([subQ0])]});Q20=makeQuery(id+"FnGEPf5ERnqVvQ3_1.11.F4.boolean.opBoolean","SPLIT",EDGE,{"disambiguationData":[TD([subQ16])],"derivedFrom":makeQuery(id+"FnGEPf5ERnqVvQ3_1.10.F4.boolean.opBoolean","SPLIT",EDGE,{"disambiguationData":[TD([subQ17])],"derivedFrom":makeQuery(id+"FnGEPf5ERnqVvQ3_1.9.F4.boolean.opBoolean","SPLIT",EDGE,{"disambiguationData":[TD([subQ17])],"derivedFrom":makeQuery(id+"FnGEPf5ERnqVvQ3_1.8.F4.boolean.opBoolean","SPLIT",EDGE,{"disambiguationData":[TD([subQ17])],"derivedFrom":makeQuery(id+"FnGEPf5ERnqVvQ3_1.7.F4.boolean.opBoolean","SPLIT",EDGE,{"disambiguationData":[TD([subQ17])],"derivedFrom":makeQuery(id+"FnGEPf5ERnqVvQ3_1.6.F4.boolean.opBoolean","SPLIT",EDGE,{"disambiguationData":[TD([subQ17])],"derivedFrom":makeQuery(id+"FnGEPf5ERnqVvQ3_1.5.F4.boolean.opBoolean","SPLIT",EDGE,{"disambiguationData":[TD([subQ17])],"derivedFrom":makeQuery(id+"FnGEPf5ERnqVvQ3_1.4.F4.boolean.opBoolean","SPLIT",EDGE,{"disambiguationData":[TD([subQ17])],"derivedFrom":makeQuery(id+"FnGEPf5ERnqVvQ3_1.3.F4.boolean.opBoolean","SPLIT",EDGE,{"disambiguationData":[TD([subQ17])],"derivedFrom":makeQuery(id+"FnGEPf5ERnqVvQ3_1.2.F4.boolean.opBoolean","SPLIT",EDGE,{"disambiguationData":[TD([subQ17])],"derivedFrom":makeQuery(id+"FnGEPf5ERnqVvQ3_1.1.F4.boolean.opBoolean","SPLIT",EDGE,{"disambiguationData":[OD(0.0)],"derivedFrom":makeQuery(id+"F1.opExtrude","CAP_EDGE",EDGE,{"disambiguationData":[OSD([subQ8])],"isStart":true})})})})})})})})})})})});}
            var Q21;
            Q21=makeQuery(id+"FnGEPf5ERnqVvQ3_1.11.F4.opExtrude","CAP_EDGE",EDGE,{"disambiguationData":[OSD([sQuery(id+"F3.wireOp",EDGE,"E23")])],"isStart":false});
            var Q22;
            {var subQ0=sQuery(id+"F3.wireOp",EDGE,"E23");var subQ8=sQuery(id+"F0.wireOp",EDGE,"E0");var subQ12=makeQuery(id+"F4.opExtrude","SWEPT_FACE",FACE,{"disambiguationData":[OSD([subQ0])]});Q22=makeQuery(id+"FnGEPf5ERnqVvQ3_1.11.F4.boolean.opBoolean","SPLIT",EDGE,{"disambiguationData":[TD([subQ12])],"derivedFrom":makeQuery(id+"FnGEPf5ERnqVvQ3_1.10.F4.boolean.opBoolean","SPLIT",EDGE,{"disambiguationData":[TD([subQ12])],"derivedFrom":makeQuery(id+"FnGEPf5ERnqVvQ3_1.9.F4.boolean.opBoolean","SPLIT",EDGE,{"disambiguationData":[TD([subQ12])],"derivedFrom":makeQuery(id+"FnGEPf5ERnqVvQ3_1.8.F4.boolean.opBoolean","SPLIT",EDGE,{"disambiguationData":[TD([subQ12])],"derivedFrom":makeQuery(id+"FnGEPf5ERnqVvQ3_1.7.F4.boolean.opBoolean","SPLIT",EDGE,{"disambiguationData":[TD([subQ12])],"derivedFrom":makeQuery(id+"FnGEPf5ERnqVvQ3_1.6.F4.boolean.opBoolean","SPLIT",EDGE,{"disambiguationData":[TD([subQ12])],"derivedFrom":makeQuery(id+"FnGEPf5ERnqVvQ3_1.5.F4.boolean.opBoolean","SPLIT",EDGE,{"disambiguationData":[TD([subQ12])],"derivedFrom":makeQuery(id+"FnGEPf5ERnqVvQ3_1.4.F4.boolean.opBoolean","SPLIT",EDGE,{"disambiguationData":[TD([subQ12])],"derivedFrom":makeQuery(id+"FnGEPf5ERnqVvQ3_1.3.F4.boolean.opBoolean","SPLIT",EDGE,{"disambiguationData":[TD([subQ12])],"derivedFrom":makeQuery(id+"FnGEPf5ERnqVvQ3_1.2.F4.boolean.opBoolean","SPLIT",EDGE,{"disambiguationData":[TD([subQ12])],"derivedFrom":makeQuery(id+"FnGEPf5ERnqVvQ3_1.1.F4.boolean.opBoolean","SPLIT",EDGE,{"disambiguationData":[OD(0.0)],"derivedFrom":makeQuery(id+"F1.opExtrude","CAP_EDGE",EDGE,{"disambiguationData":[OSD([subQ8])],"isStart":true})})})})})})})})})})})});}
            var Q23;
            Q23=makeQuery(id+"F4.opExtrude","CAP_EDGE",EDGE,{"disambiguationData":[OSD([sQuery(id+"F3.wireOp",EDGE,"E23")])],"isStart":false});
            chamfer(context, id + "F7", {"entities" : qUnion([Q0, Q1, Q2, Q3, Q4, Q5, Q6, Q7, Q8, Q9, Q10, Q11, Q12, Q13, Q14, Q15, Q16, Q17, Q18, Q19, Q20, Q21, Q22, Q23]), "width" : 1 * mm, "tangentPropagation" : true});
        }
    });
